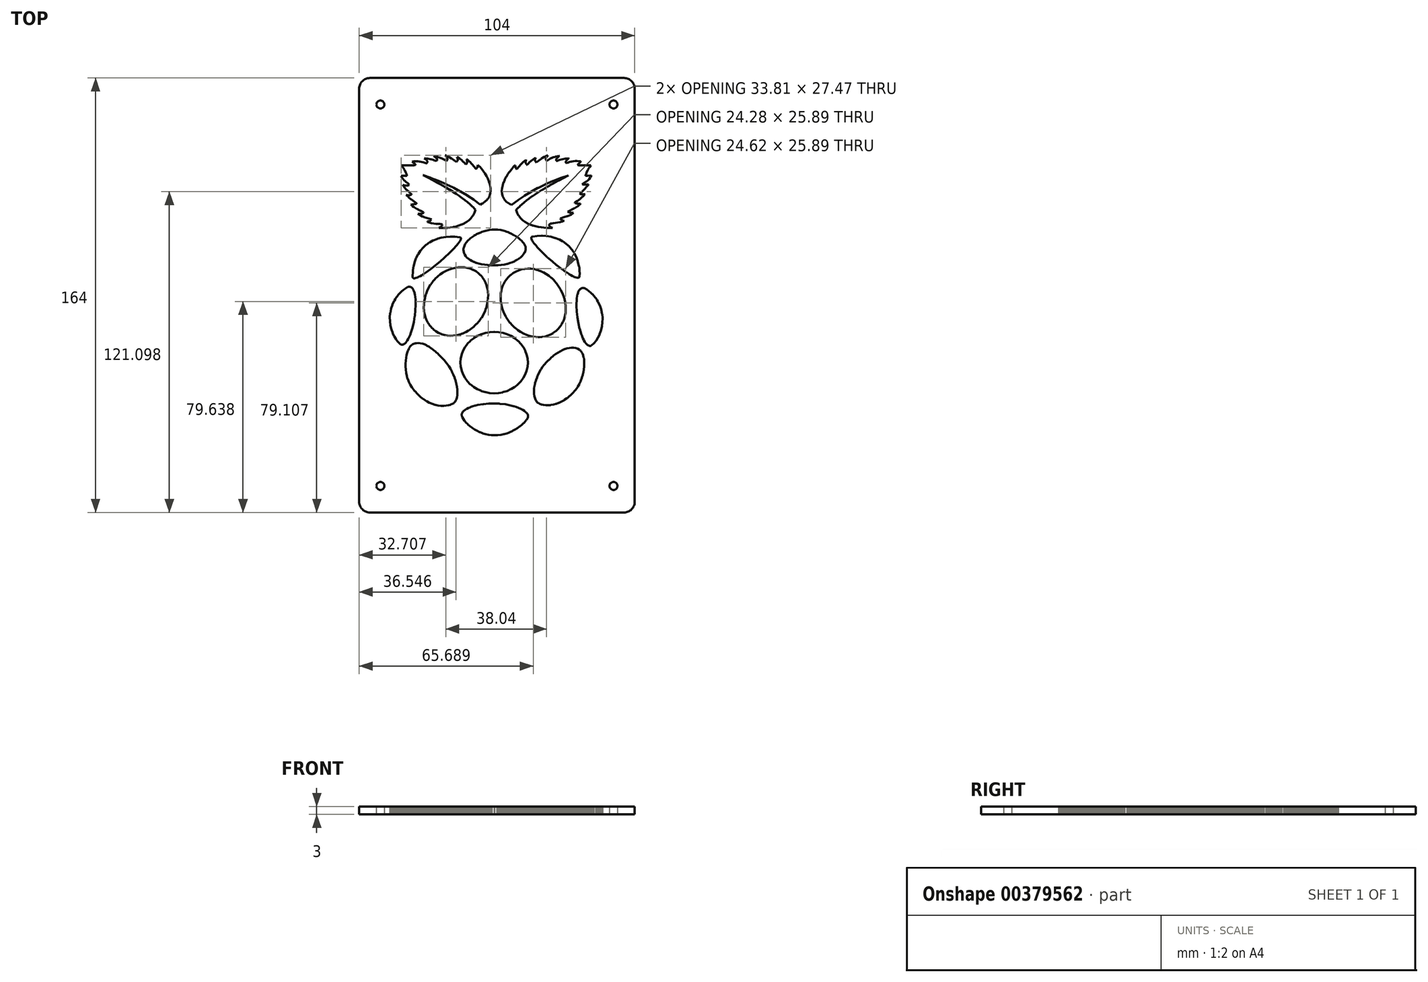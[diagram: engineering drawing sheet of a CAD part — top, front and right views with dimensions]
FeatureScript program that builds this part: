
annotation { "Feature Type Name" : "Feature", "Feature Type Description" : "" }
export const myFeature = defineFeature(function(context is Context, id is Id, definition is map)
    precondition{}
    {
        {
            var Q0;
            Q0=qCreatedBy(makeId("Top.planeOp"),FACE);
            var sketch = newSketch(context, id + "F0", { "sketchPlane" : qUnion([Q0])});
            skLineSegment(sketch, "E0.bottom", {"start": v(48, -82) * mm, "end": v(-48, -82) * mm});
            skLineSegment(sketch, "E0.top", {"start": v(48, 82) * mm, "end": v(-48, 82) * mm});
            skLineSegment(sketch, "E0.left", {"start": v(52, -78) * mm, "end": v(52, 78) * mm});
            skLineSegment(sketch, "E0.right", {"start": v(-52, -78) * mm, "end": v(-52, 78) * mm});
            skLineSegment(sketch, "E1", {"start": v(0, 97.18) * mm, "end": v(0, -103.74) * mm, "construction": true});
            skPoint(sketch, "E1.endSnap0", {"position": v(0, -82) * mm});
            skLineSegment(sketch, "E2", {"start": v(-56.62, 0) * mm, "end": v(57, 0) * mm, "construction": true});
            skPoint(sketch, "E3.visualSharp", {"position": v(-52, 82) * mm});
            skArc(sketch, "E3.filletArc", {"start": v(-48, 82) * mm, "mid": v(-50.83, 80.83) * mm, "end": v(-52, 78) * mm});
            skPoint(sketch, "E4.visualSharp", {"position": v(52, 82) * mm});
            skArc(sketch, "E4.filletArc", {"start": v(52, 78) * mm, "mid": v(50.83, 80.83) * mm, "end": v(48, 82) * mm});
            skPoint(sketch, "E5.visualSharp", {"position": v(52, -82) * mm});
            skArc(sketch, "E5.filletArc", {"start": v(48, -82) * mm, "mid": v(50.83, -80.83) * mm, "end": v(52, -78) * mm});
            skPoint(sketch, "E6.visualSharp", {"position": v(-52, -82) * mm});
            skArc(sketch, "E6.filletArc", {"start": v(-52, -78) * mm, "mid": v(-50.83, -80.83) * mm, "end": v(-48, -82) * mm});
            skLineSegment(sketch, "E7", {"start": v(-44, 86.75) * mm, "end": v(-44, -88.25) * mm, "construction": true});
            skLineSegment(sketch, "E8.MirrorCS", {"start": v(44, 86.75) * mm, "end": v(44, -88.25) * mm, "construction": true});
            skLineSegment(sketch, "E9", {"start": v(-54.83, 72) * mm, "end": v(56.5, 72) * mm, "construction": true});
            skLineSegment(sketch, "E10.MirrorCS", {"start": v(-54.83, -72) * mm, "end": v(56.5, -72) * mm, "construction": true});
            skCircle(sketch, "E11", {"center": v(-44, 72) * mm, "radius": 1.5 * mm});
            skCircle(sketch, "E12.MirrorC", {"center": v(44, 72) * mm, "radius": 1.5 * mm});
            skCircle(sketch, "E13.MirrorC", {"center": v(-44, -72) * mm, "radius": 1.5 * mm});
            skCircle(sketch, "E14.MirrorC", {"center": v(44, -72) * mm, "radius": 1.5 * mm});
            skLineSegment(sketch, "E15", {"start": v(7.16, 48.01) * mm, "end": v(7.15, 48.03) * mm});
            skLineSegment(sketch, "E16", {"start": v(7.15, 48.03) * mm, "end": v(7, 48.43) * mm});
            skLineSegment(sketch, "E17", {"start": v(7, 48.43) * mm, "end": v(6.99, 48.45) * mm});
            skLineSegment(sketch, "E18", {"start": v(6.99, 48.45) * mm, "end": v(6.83, 48.98) * mm});
            skLineSegment(sketch, "E19", {"start": v(6.83, 48.98) * mm, "end": v(6.83, 49) * mm});
            skLineSegment(sketch, "E20", {"start": v(6.83, 49) * mm, "end": v(6.18, 48.33) * mm});
            skLineSegment(sketch, "E21", {"start": v(6.18, 48.33) * mm, "end": v(6.15, 48.3) * mm});
            skLineSegment(sketch, "E22", {"start": v(6.15, 48.3) * mm, "end": v(5.5, 47.55) * mm});
            skLineSegment(sketch, "E23", {"start": v(5.5, 47.55) * mm, "end": v(5.45, 47.49) * mm});
            skLineSegment(sketch, "E24", {"start": v(5.45, 47.49) * mm, "end": v(4.8, 46.66) * mm});
            skLineSegment(sketch, "E25", {"start": v(4.8, 46.66) * mm, "end": v(4.76, 46.59) * mm});
            skLineSegment(sketch, "E26", {"start": v(4.76, 46.59) * mm, "end": v(4.14, 45.7) * mm});
            skLineSegment(sketch, "E27", {"start": v(4.14, 45.7) * mm, "end": v(3.56, 44.75) * mm});
            skLineSegment(sketch, "E28", {"start": v(3.56, 44.75) * mm, "end": v(3.52, 44.67) * mm});
            skLineSegment(sketch, "E29", {"start": v(3.52, 44.67) * mm, "end": v(3, 43.68) * mm});
            skLineSegment(sketch, "E30", {"start": v(3, 43.68) * mm, "end": v(2.96, 43.6) * mm});
            skLineSegment(sketch, "E31", {"start": v(2.96, 43.6) * mm, "end": v(2.53, 42.6) * mm});
            skLineSegment(sketch, "E32", {"start": v(2.53, 42.6) * mm, "end": v(2.5, 42.5) * mm});
            skLineSegment(sketch, "E33", {"start": v(2.5, 42.5) * mm, "end": v(2.16, 41.49) * mm});
            skLineSegment(sketch, "E34", {"start": v(2.16, 41.49) * mm, "end": v(2.15, 41.4) * mm});
            skLineSegment(sketch, "E35", {"start": v(2.15, 41.4) * mm, "end": v(1.93, 40.38) * mm});
            skLineSegment(sketch, "E36", {"start": v(1.93, 40.38) * mm, "end": v(1.92, 40.34) * mm});
            skLineSegment(sketch, "E37", {"start": v(1.92, 40.34) * mm, "end": v(1.84, 39.34) * mm});
            skLineSegment(sketch, "E38", {"start": v(1.84, 39.34) * mm, "end": v(1.84, 39.3) * mm});
            skLineSegment(sketch, "E39", {"start": v(1.84, 39.3) * mm, "end": v(1.92, 38.32) * mm});
            skLineSegment(sketch, "E40", {"start": v(1.92, 38.32) * mm, "end": v(1.92, 38.28) * mm});
            skLineSegment(sketch, "E41", {"start": v(1.92, 38.28) * mm, "end": v(2.03, 37.8) * mm});
            skLineSegment(sketch, "E42", {"start": v(2.03, 37.8) * mm, "end": v(2.04, 37.77) * mm});
            skLineSegment(sketch, "E43", {"start": v(2.04, 37.77) * mm, "end": v(2.18, 37.3) * mm});
            skLineSegment(sketch, "E44", {"start": v(2.18, 37.3) * mm, "end": v(2.2, 37.27) * mm});
            skLineSegment(sketch, "E45", {"start": v(2.2, 37.27) * mm, "end": v(2.4, 36.83) * mm});
            skLineSegment(sketch, "E46", {"start": v(2.4, 36.83) * mm, "end": v(2.65, 36.4) * mm});
            skLineSegment(sketch, "E47", {"start": v(2.65, 36.4) * mm, "end": v(2.67, 36.36) * mm});
            skLineSegment(sketch, "E48", {"start": v(2.67, 36.36) * mm, "end": v(2.97, 35.95) * mm});
            skLineSegment(sketch, "E49", {"start": v(2.97, 35.95) * mm, "end": v(3, 35.91) * mm});
            skLineSegment(sketch, "E50", {"start": v(3, 35.91) * mm, "end": v(3.35, 35.52) * mm});
            skLineSegment(sketch, "E51", {"start": v(3.35, 35.52) * mm, "end": v(3.4, 35.49) * mm});
            skLineSegment(sketch, "E52", {"start": v(3.4, 35.49) * mm, "end": v(3.8, 35.12) * mm});
            skLineSegment(sketch, "E53", {"start": v(3.8, 35.12) * mm, "end": v(4.28, 34.77) * mm});
            skLineSegment(sketch, "E54", {"start": v(4.28, 34.77) * mm, "end": v(4.32, 34.74) * mm});
            skLineSegment(sketch, "E55", {"start": v(4.32, 34.74) * mm, "end": v(4.86, 34.42) * mm});
            skLineSegment(sketch, "E56", {"start": v(4.86, 34.42) * mm, "end": v(5.46, 34.12) * mm});
            skLineSegment(sketch, "E57", {"start": v(5.46, 34.12) * mm, "end": v(5.5, 34.1) * mm});
            skLineSegment(sketch, "E58", {"start": v(5.5, 34.1) * mm, "end": v(5.52, 34.1) * mm});
            skLineSegment(sketch, "E59", {"start": v(5.52, 34.1) * mm, "end": v(5.64, 34.2) * mm});
            skLineSegment(sketch, "E60", {"start": v(5.64, 34.2) * mm, "end": v(7.85, 35.87) * mm});
            skLineSegment(sketch, "E61", {"start": v(7.85, 35.87) * mm, "end": v(7.98, 35.96) * mm});
            skLineSegment(sketch, "E62", {"start": v(7.98, 35.96) * mm, "end": v(10.28, 37.52) * mm});
            skLineSegment(sketch, "E63", {"start": v(10.28, 37.52) * mm, "end": v(10.41, 37.6) * mm});
            skLineSegment(sketch, "E64", {"start": v(10.41, 37.6) * mm, "end": v(12.8, 39.06) * mm});
            skLineSegment(sketch, "E65", {"start": v(12.8, 39.06) * mm, "end": v(12.94, 39.13) * mm});
            skLineSegment(sketch, "E66", {"start": v(12.94, 39.13) * mm, "end": v(15.42, 40.48) * mm});
            skLineSegment(sketch, "E67", {"start": v(15.42, 40.48) * mm, "end": v(15.6, 40.57) * mm});
            skLineSegment(sketch, "E68", {"start": v(15.6, 40.57) * mm, "end": v(18.16, 41.82) * mm});
            skLineSegment(sketch, "E69", {"start": v(18.16, 41.82) * mm, "end": v(18.34, 41.9) * mm});
            skLineSegment(sketch, "E70", {"start": v(18.34, 41.9) * mm, "end": v(21, 43.04) * mm});
            skLineSegment(sketch, "E71", {"start": v(21, 43.04) * mm, "end": v(21.18, 43.11) * mm});
            skLineSegment(sketch, "E72", {"start": v(21.18, 43.11) * mm, "end": v(23.91, 44.16) * mm});
            skLineSegment(sketch, "E73", {"start": v(23.91, 44.16) * mm, "end": v(26.73, 45.1) * mm});
            skLineSegment(sketch, "E74", {"start": v(26.73, 45.1) * mm, "end": v(26.83, 45.14) * mm});
            skLineSegment(sketch, "E75", {"start": v(26.83, 45.14) * mm, "end": v(26.92, 45.17) * mm});
            skLineSegment(sketch, "E76", {"start": v(26.92, 45.17) * mm, "end": v(25.1, 44.25) * mm});
            skLineSegment(sketch, "E77", {"start": v(25.1, 44.25) * mm, "end": v(25.02, 44.22) * mm});
            skLineSegment(sketch, "E78", {"start": v(25.02, 44.22) * mm, "end": v(23.35, 43.34) * mm});
            skLineSegment(sketch, "E79", {"start": v(23.35, 43.34) * mm, "end": v(23.23, 43.28) * mm});
            skLineSegment(sketch, "E80", {"start": v(23.23, 43.28) * mm, "end": v(21.64, 42.42) * mm});
            skLineSegment(sketch, "E81", {"start": v(21.64, 42.42) * mm, "end": v(21.53, 42.36) * mm});
            skLineSegment(sketch, "E82", {"start": v(21.53, 42.36) * mm, "end": v(20.02, 41.52) * mm});
            skLineSegment(sketch, "E83", {"start": v(20.02, 41.52) * mm, "end": v(19.92, 41.46) * mm});
            skLineSegment(sketch, "E84", {"start": v(19.92, 41.46) * mm, "end": v(18.5, 40.64) * mm});
            skLineSegment(sketch, "E85", {"start": v(18.5, 40.64) * mm, "end": v(18.4, 40.58) * mm});
            skLineSegment(sketch, "E86", {"start": v(18.4, 40.58) * mm, "end": v(17.07, 39.78) * mm});
            skLineSegment(sketch, "E87", {"start": v(17.07, 39.78) * mm, "end": v(16.98, 39.72) * mm});
            skLineSegment(sketch, "E88", {"start": v(16.98, 39.72) * mm, "end": v(15.72, 38.94) * mm});
            skLineSegment(sketch, "E89", {"start": v(15.72, 38.94) * mm, "end": v(14.54, 38.17) * mm});
            skLineSegment(sketch, "E90", {"start": v(14.54, 38.17) * mm, "end": v(14.46, 38.11) * mm});
            skLineSegment(sketch, "E91", {"start": v(14.46, 38.11) * mm, "end": v(13.36, 37.36) * mm});
            skLineSegment(sketch, "E92", {"start": v(13.36, 37.36) * mm, "end": v(13.28, 37.3) * mm});
            skLineSegment(sketch, "E93", {"start": v(13.28, 37.3) * mm, "end": v(12.26, 36.57) * mm});
            skLineSegment(sketch, "E94", {"start": v(12.26, 36.57) * mm, "end": v(12.16, 36.5) * mm});
            skLineSegment(sketch, "E95", {"start": v(12.16, 36.5) * mm, "end": v(11.2, 35.77) * mm});
            skLineSegment(sketch, "E96", {"start": v(11.2, 35.77) * mm, "end": v(10.33, 35.06) * mm});
            skLineSegment(sketch, "E97", {"start": v(10.33, 35.06) * mm, "end": v(10.24, 35) * mm});
            skLineSegment(sketch, "E98", {"start": v(10.24, 35) * mm, "end": v(9.43, 34.3) * mm});
            skLineSegment(sketch, "E99", {"start": v(9.43, 34.3) * mm, "end": v(8.69, 33.63) * mm});
            skLineSegment(sketch, "E100", {"start": v(8.69, 33.63) * mm, "end": v(8.61, 33.56) * mm});
            skLineSegment(sketch, "E101", {"start": v(8.61, 33.56) * mm, "end": v(7.94, 32.9) * mm});
            skLineSegment(sketch, "E102", {"start": v(7.94, 32.9) * mm, "end": v(7.33, 32.25) * mm});
            skLineSegment(sketch, "E103", {"start": v(7.33, 32.25) * mm, "end": v(7.28, 32.2) * mm});
            skLineSegment(sketch, "E104", {"start": v(7.28, 32.2) * mm, "end": v(7.26, 32.18) * mm});
            skLineSegment(sketch, "E105", {"start": v(7.26, 32.18) * mm, "end": v(7.28, 32.13) * mm});
            skLineSegment(sketch, "E106", {"start": v(7.28, 32.13) * mm, "end": v(7.66, 31.04) * mm});
            skLineSegment(sketch, "E107", {"start": v(7.66, 31.04) * mm, "end": v(7.68, 31) * mm});
            skLineSegment(sketch, "E108", {"start": v(7.68, 31) * mm, "end": v(8.2, 30.02) * mm});
            skLineSegment(sketch, "E109", {"start": v(8.2, 30.02) * mm, "end": v(8.23, 29.98) * mm});
            skLineSegment(sketch, "E110", {"start": v(8.23, 29.98) * mm, "end": v(8.87, 29.14) * mm});
            skLineSegment(sketch, "E111", {"start": v(8.87, 29.14) * mm, "end": v(8.9, 29.1) * mm});
            skLineSegment(sketch, "E112", {"start": v(8.9, 29.1) * mm, "end": v(8.94, 29.06) * mm});
            skLineSegment(sketch, "E113", {"start": v(8.94, 29.06) * mm, "end": v(9.68, 28.34) * mm});
            skLineSegment(sketch, "E114", {"start": v(9.68, 28.34) * mm, "end": v(9.73, 28.3) * mm});
            skLineSegment(sketch, "E115", {"start": v(9.73, 28.3) * mm, "end": v(10.56, 27.68) * mm});
            skLineSegment(sketch, "E116", {"start": v(10.56, 27.68) * mm, "end": v(10.61, 27.65) * mm});
            skLineSegment(sketch, "E117", {"start": v(10.61, 27.65) * mm, "end": v(11.5, 27.13) * mm});
            skLineSegment(sketch, "E118", {"start": v(11.5, 27.13) * mm, "end": v(11.56, 27.1) * mm});
            skLineSegment(sketch, "E119", {"start": v(11.56, 27.1) * mm, "end": v(12.51, 26.67) * mm});
            skLineSegment(sketch, "E120", {"start": v(12.51, 26.67) * mm, "end": v(12.57, 26.65) * mm});
            skLineSegment(sketch, "E121", {"start": v(12.57, 26.65) * mm, "end": v(13.55, 26.3) * mm});
            skLineSegment(sketch, "E122", {"start": v(13.55, 26.3) * mm, "end": v(13.61, 26.28) * mm});
            skLineSegment(sketch, "E123", {"start": v(13.61, 26.28) * mm, "end": v(14.6, 26) * mm});
            skLineSegment(sketch, "E124", {"start": v(14.6, 26) * mm, "end": v(14.67, 26) * mm});
            skLineSegment(sketch, "E125", {"start": v(14.67, 26) * mm, "end": v(15.67, 25.78) * mm});
            skLineSegment(sketch, "E126", {"start": v(15.67, 25.78) * mm, "end": v(15.73, 25.77) * mm});
            skLineSegment(sketch, "E127", {"start": v(15.73, 25.77) * mm, "end": v(16.7, 25.62) * mm});
            skLineSegment(sketch, "E128", {"start": v(16.7, 25.62) * mm, "end": v(16.8, 25.6) * mm});
            skLineSegment(sketch, "E129", {"start": v(16.8, 25.6) * mm, "end": v(17.74, 25.5) * mm});
            skLineSegment(sketch, "E130", {"start": v(17.74, 25.5) * mm, "end": v(18.63, 25.43) * mm});
            skLineSegment(sketch, "E131", {"start": v(18.63, 25.43) * mm, "end": v(18.69, 25.43) * mm});
            skLineSegment(sketch, "E132", {"start": v(18.69, 25.43) * mm, "end": v(19.5, 25.39) * mm});
            skLineSegment(sketch, "E133", {"start": v(19.5, 25.39) * mm, "end": v(19.56, 25.38) * mm});
            skLineSegment(sketch, "E134", {"start": v(19.56, 25.38) * mm, "end": v(20.3, 25.37) * mm});
            skLineSegment(sketch, "E135", {"start": v(20.3, 25.37) * mm, "end": v(20.34, 25.37) * mm});
            skLineSegment(sketch, "E136", {"start": v(20.34, 25.37) * mm, "end": v(20.98, 25.36) * mm});
            skLineSegment(sketch, "E137", {"start": v(20.98, 25.36) * mm, "end": v(21.02, 25.36) * mm});
            skLineSegment(sketch, "E138", {"start": v(21.02, 25.36) * mm, "end": v(21, 25.37) * mm});
            skLineSegment(sketch, "E139", {"start": v(21, 25.37) * mm, "end": v(20.55, 25.56) * mm});
            skLineSegment(sketch, "E140", {"start": v(20.55, 25.56) * mm, "end": v(20.53, 25.57) * mm});
            skLineSegment(sketch, "E141", {"start": v(20.53, 25.57) * mm, "end": v(20.32, 25.69) * mm});
            skLineSegment(sketch, "E142", {"start": v(20.32, 25.69) * mm, "end": v(20.3, 25.7) * mm});
            skLineSegment(sketch, "E143", {"start": v(20.3, 25.7) * mm, "end": v(20.12, 25.84) * mm});
            skLineSegment(sketch, "E144", {"start": v(20.12, 25.84) * mm, "end": v(20.11, 25.85) * mm});
            skLineSegment(sketch, "E145", {"start": v(20.11, 25.85) * mm, "end": v(19.96, 26) * mm});
            skLineSegment(sketch, "E146", {"start": v(19.96, 26) * mm, "end": v(19.95, 26.01) * mm});
            skLineSegment(sketch, "E147", {"start": v(19.95, 26.01) * mm, "end": v(19.88, 26.1) * mm});
            skLineSegment(sketch, "E148", {"start": v(19.88, 26.1) * mm, "end": v(19.88, 26.1) * mm});
            skLineSegment(sketch, "E149", {"start": v(19.88, 26.1) * mm, "end": v(19.82, 26.2) * mm});
            skLineSegment(sketch, "E150", {"start": v(19.82, 26.2) * mm, "end": v(19.82, 26.2) * mm});
            skLineSegment(sketch, "E151", {"start": v(19.82, 26.2) * mm, "end": v(19.77, 26.3) * mm});
            skLineSegment(sketch, "E152", {"start": v(19.77, 26.3) * mm, "end": v(19.77, 26.3) * mm});
            skLineSegment(sketch, "E153", {"start": v(19.77, 26.3) * mm, "end": v(19.74, 26.4) * mm});
            skLineSegment(sketch, "E154", {"start": v(19.74, 26.4) * mm, "end": v(19.74, 26.41) * mm});
            skLineSegment(sketch, "E155", {"start": v(19.74, 26.41) * mm, "end": v(19.72, 26.52) * mm});
            skLineSegment(sketch, "E156", {"start": v(19.72, 26.52) * mm, "end": v(19.72, 26.52) * mm});
            skLineSegment(sketch, "E157", {"start": v(19.72, 26.52) * mm, "end": v(19.7, 26.63) * mm});
            skLineSegment(sketch, "E158", {"start": v(19.7, 26.63) * mm, "end": v(19.7, 26.64) * mm});
            skLineSegment(sketch, "E159", {"start": v(19.7, 26.64) * mm, "end": v(19.71, 26.64) * mm});
            skLineSegment(sketch, "E160", {"start": v(19.71, 26.64) * mm, "end": v(19.78, 26.71) * mm});
            skLineSegment(sketch, "E161", {"start": v(19.78, 26.71) * mm, "end": v(19.78, 26.72) * mm});
            skLineSegment(sketch, "E162", {"start": v(19.78, 26.72) * mm, "end": v(19.86, 26.78) * mm});
            skLineSegment(sketch, "E163", {"start": v(19.86, 26.78) * mm, "end": v(19.86, 26.79) * mm});
            skLineSegment(sketch, "E164", {"start": v(19.86, 26.79) * mm, "end": v(19.95, 26.85) * mm});
            skLineSegment(sketch, "E165", {"start": v(19.95, 26.85) * mm, "end": v(19.95, 26.85) * mm});
            skLineSegment(sketch, "E166", {"start": v(19.95, 26.85) * mm, "end": v(20.06, 26.9) * mm});
            skLineSegment(sketch, "E167", {"start": v(20.06, 26.9) * mm, "end": v(20.07, 26.9) * mm});
            skLineSegment(sketch, "E168", {"start": v(20.07, 26.9) * mm, "end": v(20.3, 27) * mm});
            skLineSegment(sketch, "E169", {"start": v(20.3, 27) * mm, "end": v(20.31, 27) * mm});
            skLineSegment(sketch, "E170", {"start": v(20.31, 27) * mm, "end": v(20.58, 27.08) * mm});
            skLineSegment(sketch, "E171", {"start": v(20.58, 27.08) * mm, "end": v(20.62, 27.09) * mm});
            skLineSegment(sketch, "E172", {"start": v(20.62, 27.09) * mm, "end": v(21.26, 27.2) * mm});
            skLineSegment(sketch, "E173", {"start": v(21.26, 27.2) * mm, "end": v(21.34, 27.21) * mm});
            skLineSegment(sketch, "E174", {"start": v(21.34, 27.21) * mm, "end": v(22.07, 27.3) * mm});
            skLineSegment(sketch, "E175", {"start": v(22.07, 27.3) * mm, "end": v(23.68, 27.56) * mm});
            skLineSegment(sketch, "E176", {"start": v(23.68, 27.56) * mm, "end": v(23.76, 27.57) * mm});
            skLineSegment(sketch, "E177", {"start": v(23.76, 27.57) * mm, "end": v(23.81, 27.58) * mm});
            skLineSegment(sketch, "E178", {"start": v(23.81, 27.58) * mm, "end": v(24.6, 27.8) * mm});
            skLineSegment(sketch, "E179", {"start": v(24.6, 27.8) * mm, "end": v(24.63, 27.8) * mm});
            skLineSegment(sketch, "E180", {"start": v(24.63, 27.8) * mm, "end": v(25.36, 28.12) * mm});
            skLineSegment(sketch, "E181", {"start": v(25.36, 28.12) * mm, "end": v(25.39, 28.13) * mm});
            skLineSegment(sketch, "E182", {"start": v(25.39, 28.13) * mm, "end": v(25.38, 28.13) * mm});
            skLineSegment(sketch, "E183", {"start": v(25.38, 28.13) * mm, "end": v(25.36, 28.14) * mm});
            skLineSegment(sketch, "E184", {"start": v(25.36, 28.14) * mm, "end": v(24.85, 28.26) * mm});
            skLineSegment(sketch, "E185", {"start": v(24.85, 28.26) * mm, "end": v(24.83, 28.27) * mm});
            skLineSegment(sketch, "E186", {"start": v(24.83, 28.27) * mm, "end": v(24.64, 28.32) * mm});
            skLineSegment(sketch, "E187", {"start": v(24.64, 28.32) * mm, "end": v(24.63, 28.33) * mm});
            skLineSegment(sketch, "E188", {"start": v(24.63, 28.33) * mm, "end": v(24.47, 28.4) * mm});
            skLineSegment(sketch, "E189", {"start": v(24.47, 28.4) * mm, "end": v(24.45, 28.4) * mm});
            skLineSegment(sketch, "E190", {"start": v(24.45, 28.4) * mm, "end": v(24.3, 28.49) * mm});
            skLineSegment(sketch, "E191", {"start": v(24.3, 28.49) * mm, "end": v(24.3, 28.5) * mm});
            skLineSegment(sketch, "E192", {"start": v(24.3, 28.5) * mm, "end": v(24.16, 28.6) * mm});
            skLineSegment(sketch, "E193", {"start": v(24.16, 28.6) * mm, "end": v(24.15, 28.62) * mm});
            skLineSegment(sketch, "E194", {"start": v(24.15, 28.62) * mm, "end": v(24.01, 28.77) * mm});
            skLineSegment(sketch, "E195", {"start": v(24.01, 28.77) * mm, "end": v(23.87, 28.97) * mm});
            skLineSegment(sketch, "E196", {"start": v(23.87, 28.97) * mm, "end": v(23.86, 28.98) * mm});
            skLineSegment(sketch, "E197", {"start": v(23.86, 28.98) * mm, "end": v(23.86, 28.98) * mm});
            skLineSegment(sketch, "E198", {"start": v(23.86, 28.98) * mm, "end": v(23.93, 29) * mm});
            skLineSegment(sketch, "E199", {"start": v(23.93, 29) * mm, "end": v(25.3, 29.43) * mm});
            skLineSegment(sketch, "E200", {"start": v(25.3, 29.43) * mm, "end": v(25.35, 29.44) * mm});
            skLineSegment(sketch, "E201", {"start": v(25.35, 29.44) * mm, "end": v(26.65, 29.87) * mm});
            skLineSegment(sketch, "E202", {"start": v(26.65, 29.87) * mm, "end": v(26.71, 29.9) * mm});
            skLineSegment(sketch, "E203", {"start": v(26.71, 29.9) * mm, "end": v(27.3, 30.13) * mm});
            skLineSegment(sketch, "E204", {"start": v(27.3, 30.13) * mm, "end": v(27.37, 30.16) * mm});
            skLineSegment(sketch, "E205", {"start": v(27.37, 30.16) * mm, "end": v(27.91, 30.42) * mm});
            skLineSegment(sketch, "E206", {"start": v(27.91, 30.42) * mm, "end": v(28.4, 30.72) * mm});
            skLineSegment(sketch, "E207", {"start": v(28.4, 30.72) * mm, "end": v(28.43, 30.74) * mm});
            skLineSegment(sketch, "E208", {"start": v(28.43, 30.74) * mm, "end": v(28.86, 31.1) * mm});
            skLineSegment(sketch, "E209", {"start": v(28.86, 31.1) * mm, "end": v(28.88, 31.11) * mm});
            skLineSegment(sketch, "E210", {"start": v(28.88, 31.11) * mm, "end": v(28.86, 31.11) * mm});
            skLineSegment(sketch, "E211", {"start": v(28.86, 31.11) * mm, "end": v(27.9, 31.09) * mm});
            skLineSegment(sketch, "E212", {"start": v(27.9, 31.09) * mm, "end": v(27.9, 31.08) * mm});
            skLineSegment(sketch, "E213", {"start": v(27.9, 31.08) * mm, "end": v(27.87, 31.09) * mm});
            skLineSegment(sketch, "E214", {"start": v(27.87, 31.09) * mm, "end": v(27.86, 31.09) * mm});
            skLineSegment(sketch, "E215", {"start": v(27.86, 31.09) * mm, "end": v(27.6, 31.12) * mm});
            skLineSegment(sketch, "E216", {"start": v(27.6, 31.12) * mm, "end": v(27.6, 31.12) * mm});
            skLineSegment(sketch, "E217", {"start": v(27.6, 31.12) * mm, "end": v(27.32, 31.2) * mm});
            skLineSegment(sketch, "E218", {"start": v(27.32, 31.2) * mm, "end": v(27.3, 31.2) * mm});
            skLineSegment(sketch, "E219", {"start": v(27.3, 31.2) * mm, "end": v(27.02, 31.33) * mm});
            skLineSegment(sketch, "E220", {"start": v(27.02, 31.33) * mm, "end": v(27, 31.34) * mm});
            skLineSegment(sketch, "E221", {"start": v(27, 31.34) * mm, "end": v(26.7, 31.53) * mm});
            skLineSegment(sketch, "E222", {"start": v(26.7, 31.53) * mm, "end": v(26.7, 31.53) * mm});
            skLineSegment(sketch, "E223", {"start": v(26.7, 31.53) * mm, "end": v(26.76, 31.57) * mm});
            skLineSegment(sketch, "E224", {"start": v(26.76, 31.57) * mm, "end": v(29.18, 32.74) * mm});
            skLineSegment(sketch, "E225", {"start": v(29.18, 32.74) * mm, "end": v(29.21, 32.76) * mm});
            skLineSegment(sketch, "E226", {"start": v(29.21, 32.76) * mm, "end": v(29.27, 32.8) * mm});
            skLineSegment(sketch, "E227", {"start": v(29.27, 32.8) * mm, "end": v(30.39, 33.5) * mm});
            skLineSegment(sketch, "E228", {"start": v(30.39, 33.5) * mm, "end": v(30.44, 33.54) * mm});
            skLineSegment(sketch, "E229", {"start": v(30.44, 33.54) * mm, "end": v(30.47, 33.57) * mm});
            skLineSegment(sketch, "E230", {"start": v(30.47, 33.57) * mm, "end": v(30.99, 34) * mm});
            skLineSegment(sketch, "E231", {"start": v(30.99, 34) * mm, "end": v(31.47, 34.49) * mm});
            skLineSegment(sketch, "E232", {"start": v(31.47, 34.49) * mm, "end": v(31.5, 34.52) * mm});
            skLineSegment(sketch, "E233", {"start": v(31.5, 34.52) * mm, "end": v(30.87, 34.53) * mm});
            skLineSegment(sketch, "E234", {"start": v(30.87, 34.53) * mm, "end": v(30.85, 34.53) * mm});
            skLineSegment(sketch, "E235", {"start": v(30.85, 34.53) * mm, "end": v(30.84, 34.53) * mm});
            skLineSegment(sketch, "E236", {"start": v(30.84, 34.53) * mm, "end": v(30.27, 34.57) * mm});
            skLineSegment(sketch, "E237", {"start": v(30.27, 34.57) * mm, "end": v(30.24, 34.57) * mm});
            skLineSegment(sketch, "E238", {"start": v(30.24, 34.57) * mm, "end": v(29.99, 34.62) * mm});
            skLineSegment(sketch, "E239", {"start": v(29.99, 34.62) * mm, "end": v(29.96, 34.62) * mm});
            skLineSegment(sketch, "E240", {"start": v(29.96, 34.62) * mm, "end": v(29.73, 34.7) * mm});
            skLineSegment(sketch, "E241", {"start": v(29.73, 34.7) * mm, "end": v(29.72, 34.7) * mm});
            skLineSegment(sketch, "E242", {"start": v(29.72, 34.7) * mm, "end": v(29.61, 34.74) * mm});
            skLineSegment(sketch, "E243", {"start": v(29.61, 34.74) * mm, "end": v(29.6, 34.75) * mm});
            skLineSegment(sketch, "E244", {"start": v(29.6, 34.75) * mm, "end": v(29.5, 34.8) * mm});
            skLineSegment(sketch, "E245", {"start": v(29.5, 34.8) * mm, "end": v(29.4, 34.87) * mm});
            skLineSegment(sketch, "E246", {"start": v(29.4, 34.87) * mm, "end": v(29.32, 34.94) * mm});
            skLineSegment(sketch, "E247", {"start": v(29.32, 34.94) * mm, "end": v(29.32, 34.94) * mm});
            skLineSegment(sketch, "E248", {"start": v(29.32, 34.94) * mm, "end": v(29.38, 34.98) * mm});
            skLineSegment(sketch, "E249", {"start": v(29.38, 34.98) * mm, "end": v(30.42, 35.62) * mm});
            skLineSegment(sketch, "E250", {"start": v(30.42, 35.62) * mm, "end": v(31.39, 36.34) * mm});
            skLineSegment(sketch, "E251", {"start": v(31.39, 36.34) * mm, "end": v(31.45, 36.38) * mm});
            skLineSegment(sketch, "E252", {"start": v(31.45, 36.38) * mm, "end": v(32.33, 37.17) * mm});
            skLineSegment(sketch, "E253", {"start": v(32.33, 37.17) * mm, "end": v(32.39, 37.22) * mm});
            skLineSegment(sketch, "E254", {"start": v(32.39, 37.22) * mm, "end": v(33.2, 38.08) * mm});
            skLineSegment(sketch, "E255", {"start": v(33.2, 38.08) * mm, "end": v(33.25, 38.14) * mm});
            skLineSegment(sketch, "E256", {"start": v(33.25, 38.14) * mm, "end": v(32.8, 38.08) * mm});
            skLineSegment(sketch, "E257", {"start": v(32.8, 38.08) * mm, "end": v(32.8, 38.08) * mm});
            skLineSegment(sketch, "E258", {"start": v(32.8, 38.08) * mm, "end": v(32.78, 38.08) * mm});
            skLineSegment(sketch, "E259", {"start": v(32.78, 38.08) * mm, "end": v(32.42, 38.05) * mm});
            skLineSegment(sketch, "E260", {"start": v(32.42, 38.05) * mm, "end": v(32.4, 38.05) * mm});
            skLineSegment(sketch, "E261", {"start": v(32.4, 38.05) * mm, "end": v(32.1, 38.06) * mm});
            skLineSegment(sketch, "E262", {"start": v(32.1, 38.06) * mm, "end": v(31.87, 38.08) * mm});
            skLineSegment(sketch, "E263", {"start": v(31.87, 38.08) * mm, "end": v(31.85, 38.09) * mm});
            skLineSegment(sketch, "E264", {"start": v(31.85, 38.09) * mm, "end": v(31.66, 38.13) * mm});
            skLineSegment(sketch, "E265", {"start": v(31.66, 38.13) * mm, "end": v(31.65, 38.13) * mm});
            skLineSegment(sketch, "E266", {"start": v(31.65, 38.13) * mm, "end": v(31.65, 38.14) * mm});
            skLineSegment(sketch, "E267", {"start": v(31.65, 38.14) * mm, "end": v(31.5, 38.2) * mm});
            skLineSegment(sketch, "E268", {"start": v(31.5, 38.2) * mm, "end": v(31.5, 38.2) * mm});
            skLineSegment(sketch, "E269", {"start": v(31.5, 38.2) * mm, "end": v(31.37, 38.27) * mm});
            skLineSegment(sketch, "E270", {"start": v(31.37, 38.27) * mm, "end": v(31.29, 38.35) * mm});
            skLineSegment(sketch, "E271", {"start": v(31.29, 38.35) * mm, "end": v(31.28, 38.35) * mm});
            skLineSegment(sketch, "E272", {"start": v(31.28, 38.35) * mm, "end": v(31.28, 38.35) * mm});
            skLineSegment(sketch, "E273", {"start": v(31.28, 38.35) * mm, "end": v(31.32, 38.4) * mm});
            skLineSegment(sketch, "E274", {"start": v(31.32, 38.4) * mm, "end": v(32.15, 39.15) * mm});
            skLineSegment(sketch, "E275", {"start": v(32.15, 39.15) * mm, "end": v(32.18, 39.17) * mm});
            skLineSegment(sketch, "E276", {"start": v(32.18, 39.17) * mm, "end": v(33.05, 39.97) * mm});
            skLineSegment(sketch, "E277", {"start": v(33.05, 39.97) * mm, "end": v(33.1, 40.01) * mm});
            skLineSegment(sketch, "E278", {"start": v(33.1, 40.01) * mm, "end": v(33.88, 40.88) * mm});
            skLineSegment(sketch, "E279", {"start": v(33.88, 40.88) * mm, "end": v(33.93, 40.93) * mm});
            skLineSegment(sketch, "E280", {"start": v(33.93, 40.93) * mm, "end": v(34.25, 41.4) * mm});
            skLineSegment(sketch, "E281", {"start": v(34.25, 41.4) * mm, "end": v(34.28, 41.43) * mm});
            skLineSegment(sketch, "E282", {"start": v(34.28, 41.43) * mm, "end": v(34.54, 41.94) * mm});
            skLineSegment(sketch, "E283", {"start": v(34.54, 41.94) * mm, "end": v(34.56, 41.97) * mm});
            skLineSegment(sketch, "E284", {"start": v(34.56, 41.97) * mm, "end": v(33.93, 41.83) * mm});
            skLineSegment(sketch, "E285", {"start": v(33.93, 41.83) * mm, "end": v(33.9, 41.82) * mm});
            skLineSegment(sketch, "E286", {"start": v(33.9, 41.82) * mm, "end": v(33.9, 41.82) * mm});
            skLineSegment(sketch, "E287", {"start": v(33.9, 41.82) * mm, "end": v(33.3, 41.74) * mm});
            skLineSegment(sketch, "E288", {"start": v(33.3, 41.74) * mm, "end": v(33.28, 41.73) * mm});
            skLineSegment(sketch, "E289", {"start": v(33.28, 41.73) * mm, "end": v(33, 41.73) * mm});
            skLineSegment(sketch, "E290", {"start": v(33, 41.73) * mm, "end": v(32.97, 41.73) * mm});
            skLineSegment(sketch, "E291", {"start": v(32.97, 41.73) * mm, "end": v(32.7, 41.76) * mm});
            skLineSegment(sketch, "E292", {"start": v(32.7, 41.76) * mm, "end": v(32.69, 41.76) * mm});
            skLineSegment(sketch, "E293", {"start": v(32.69, 41.76) * mm, "end": v(32.56, 41.8) * mm});
            skLineSegment(sketch, "E294", {"start": v(32.56, 41.8) * mm, "end": v(32.54, 41.8) * mm});
            skLineSegment(sketch, "E295", {"start": v(32.54, 41.8) * mm, "end": v(32.42, 41.84) * mm});
            skLineSegment(sketch, "E296", {"start": v(32.42, 41.84) * mm, "end": v(32.4, 41.84) * mm});
            skLineSegment(sketch, "E297", {"start": v(32.4, 41.84) * mm, "end": v(32.29, 41.9) * mm});
            skLineSegment(sketch, "E298", {"start": v(32.29, 41.9) * mm, "end": v(32.17, 41.97) * mm});
            skLineSegment(sketch, "E299", {"start": v(32.17, 41.97) * mm, "end": v(32.16, 41.97) * mm});
            skLineSegment(sketch, "E300", {"start": v(32.16, 41.97) * mm, "end": v(32.16, 41.97) * mm});
            skLineSegment(sketch, "E301", {"start": v(32.16, 41.97) * mm, "end": v(32.51, 42.2) * mm});
            skLineSegment(sketch, "E302", {"start": v(32.51, 42.2) * mm, "end": v(32.52, 42.2) * mm});
            skLineSegment(sketch, "E303", {"start": v(32.52, 42.2) * mm, "end": v(32.53, 42.21) * mm});
            skLineSegment(sketch, "E304", {"start": v(32.53, 42.21) * mm, "end": v(32.94, 42.44) * mm});
            skLineSegment(sketch, "E305", {"start": v(32.94, 42.44) * mm, "end": v(32.97, 42.45) * mm});
            skLineSegment(sketch, "E306", {"start": v(32.97, 42.45) * mm, "end": v(33.86, 42.99) * mm});
            skLineSegment(sketch, "E307", {"start": v(33.86, 42.99) * mm, "end": v(33.9, 43.02) * mm});
            skLineSegment(sketch, "E308", {"start": v(33.9, 43.02) * mm, "end": v(34.37, 43.37) * mm});
            skLineSegment(sketch, "E309", {"start": v(34.37, 43.37) * mm, "end": v(34.39, 43.4) * mm});
            skLineSegment(sketch, "E310", {"start": v(34.39, 43.4) * mm, "end": v(34.41, 43.41) * mm});
            skLineSegment(sketch, "E311", {"start": v(34.41, 43.41) * mm, "end": v(34.85, 43.85) * mm});
            skLineSegment(sketch, "E312", {"start": v(34.85, 43.85) * mm, "end": v(34.87, 43.87) * mm});
            skLineSegment(sketch, "E313", {"start": v(34.87, 43.87) * mm, "end": v(35.27, 44.42) * mm});
            skLineSegment(sketch, "E314", {"start": v(35.27, 44.42) * mm, "end": v(35.28, 44.44) * mm});
            skLineSegment(sketch, "E315", {"start": v(35.28, 44.44) * mm, "end": v(35.3, 44.46) * mm});
            skLineSegment(sketch, "E316", {"start": v(35.3, 44.46) * mm, "end": v(35.64, 45.14) * mm});
            skLineSegment(sketch, "E317", {"start": v(35.64, 45.14) * mm, "end": v(35.65, 45.17) * mm});
            skLineSegment(sketch, "E318", {"start": v(35.65, 45.17) * mm, "end": v(35.61, 45.17) * mm});
            skLineSegment(sketch, "E319", {"start": v(35.61, 45.17) * mm, "end": v(34.36, 45.1) * mm});
            skLineSegment(sketch, "E320", {"start": v(34.36, 45.1) * mm, "end": v(34.34, 45.1) * mm});
            skLineSegment(sketch, "E321", {"start": v(34.34, 45.1) * mm, "end": v(34.3, 45.09) * mm});
            skLineSegment(sketch, "E322", {"start": v(34.3, 45.09) * mm, "end": v(33.8, 45.08) * mm});
            skLineSegment(sketch, "E323", {"start": v(33.8, 45.08) * mm, "end": v(33.78, 45.08) * mm});
            skLineSegment(sketch, "E324", {"start": v(33.78, 45.08) * mm, "end": v(33.68, 45.09) * mm});
            skLineSegment(sketch, "E325", {"start": v(33.68, 45.09) * mm, "end": v(33.67, 45.1) * mm});
            skLineSegment(sketch, "E326", {"start": v(33.67, 45.1) * mm, "end": v(33.6, 45.1) * mm});
            skLineSegment(sketch, "E327", {"start": v(33.6, 45.1) * mm, "end": v(33.59, 45.1) * mm});
            skLineSegment(sketch, "E328", {"start": v(33.59, 45.1) * mm, "end": v(33.55, 45.12) * mm});
            skLineSegment(sketch, "E329", {"start": v(33.55, 45.12) * mm, "end": v(33.52, 45.13) * mm});
            skLineSegment(sketch, "E330", {"start": v(33.52, 45.13) * mm, "end": v(33.5, 45.15) * mm});
            skLineSegment(sketch, "E331", {"start": v(33.5, 45.15) * mm, "end": v(33.47, 45.17) * mm});
            skLineSegment(sketch, "E332", {"start": v(33.47, 45.17) * mm, "end": v(33.47, 45.17) * mm});
            skLineSegment(sketch, "E333", {"start": v(33.47, 45.17) * mm, "end": v(33.48, 45.2) * mm});
            skLineSegment(sketch, "E334", {"start": v(33.48, 45.2) * mm, "end": v(33.65, 45.77) * mm});
            skLineSegment(sketch, "E335", {"start": v(33.65, 45.77) * mm, "end": v(33.85, 46.3) * mm});
            skLineSegment(sketch, "E336", {"start": v(33.85, 46.3) * mm, "end": v(33.88, 46.36) * mm});
            skLineSegment(sketch, "E337", {"start": v(33.88, 46.36) * mm, "end": v(34.35, 47.29) * mm});
            skLineSegment(sketch, "E338", {"start": v(34.35, 47.29) * mm, "end": v(34.37, 47.34) * mm});
            skLineSegment(sketch, "E339", {"start": v(34.37, 47.34) * mm, "end": v(34.88, 48.15) * mm});
            skLineSegment(sketch, "E340", {"start": v(34.88, 48.15) * mm, "end": v(34.91, 48.2) * mm});
            skLineSegment(sketch, "E341", {"start": v(34.91, 48.2) * mm, "end": v(35.42, 48.98) * mm});
            skLineSegment(sketch, "E342", {"start": v(35.42, 48.98) * mm, "end": v(35.43, 49) * mm});
            skLineSegment(sketch, "E343", {"start": v(35.43, 49) * mm, "end": v(34.63, 49) * mm});
            skLineSegment(sketch, "E344", {"start": v(34.63, 49) * mm, "end": v(33.82, 49) * mm});
            skLineSegment(sketch, "E345", {"start": v(33.82, 49) * mm, "end": v(33.75, 49) * mm});
            skLineSegment(sketch, "E346", {"start": v(33.75, 49) * mm, "end": v(32.17, 49.03) * mm});
            skLineSegment(sketch, "E347", {"start": v(32.17, 49.03) * mm, "end": v(32.1, 49.03) * mm});
            skLineSegment(sketch, "E348", {"start": v(32.1, 49.03) * mm, "end": v(32.07, 49.03) * mm});
            skLineSegment(sketch, "E349", {"start": v(32.07, 49.03) * mm, "end": v(31.4, 49.05) * mm});
            skLineSegment(sketch, "E350", {"start": v(31.4, 49.05) * mm, "end": v(31.37, 49.05) * mm});
            skLineSegment(sketch, "E351", {"start": v(31.37, 49.05) * mm, "end": v(30.85, 49.09) * mm});
            skLineSegment(sketch, "E352", {"start": v(30.85, 49.09) * mm, "end": v(30.83, 49.1) * mm});
            skLineSegment(sketch, "E353", {"start": v(30.83, 49.1) * mm, "end": v(30.64, 49.11) * mm});
            skLineSegment(sketch, "E354", {"start": v(30.64, 49.11) * mm, "end": v(30.62, 49.12) * mm});
            skLineSegment(sketch, "E355", {"start": v(30.62, 49.12) * mm, "end": v(30.49, 49.14) * mm});
            skLineSegment(sketch, "E356", {"start": v(30.49, 49.14) * mm, "end": v(30.44, 49.16) * mm});
            skLineSegment(sketch, "E357", {"start": v(30.44, 49.16) * mm, "end": v(30.43, 49.17) * mm});
            skLineSegment(sketch, "E358", {"start": v(30.43, 49.17) * mm, "end": v(30.42, 49.17) * mm});
            skLineSegment(sketch, "E359", {"start": v(30.42, 49.17) * mm, "end": v(30.42, 49.17) * mm});
            skLineSegment(sketch, "E360", {"start": v(30.42, 49.17) * mm, "end": v(30.41, 49.18) * mm});
            skLineSegment(sketch, "E361", {"start": v(30.41, 49.18) * mm, "end": v(30.41, 49.18) * mm});
            skLineSegment(sketch, "E362", {"start": v(30.41, 49.18) * mm, "end": v(30.4, 49.18) * mm});
            skLineSegment(sketch, "E363", {"start": v(30.4, 49.18) * mm, "end": v(30.4, 49.19) * mm});
            skLineSegment(sketch, "E364", {"start": v(30.4, 49.19) * mm, "end": v(30.4, 49.19) * mm});
            skLineSegment(sketch, "E365", {"start": v(30.4, 49.19) * mm, "end": v(30.4, 49.2) * mm});
            skLineSegment(sketch, "E366", {"start": v(30.4, 49.2) * mm, "end": v(30.4, 49.2) * mm});
            skLineSegment(sketch, "E367", {"start": v(30.4, 49.2) * mm, "end": v(30.4, 49.21) * mm});
            skLineSegment(sketch, "E368", {"start": v(30.4, 49.21) * mm, "end": v(31.68, 50.46) * mm});
            skLineSegment(sketch, "E369", {"start": v(31.68, 50.46) * mm, "end": v(31.72, 50.5) * mm});
            skLineSegment(sketch, "E370", {"start": v(31.72, 50.5) * mm, "end": v(31, 50.6) * mm});
            skLineSegment(sketch, "E371", {"start": v(31, 50.6) * mm, "end": v(30.97, 50.61) * mm});
            skLineSegment(sketch, "E372", {"start": v(30.97, 50.61) * mm, "end": v(30.26, 50.66) * mm});
            skLineSegment(sketch, "E373", {"start": v(30.26, 50.66) * mm, "end": v(30.21, 50.66) * mm});
            skLineSegment(sketch, "E374", {"start": v(30.21, 50.66) * mm, "end": v(29.5, 50.65) * mm});
            skLineSegment(sketch, "E375", {"start": v(29.5, 50.65) * mm, "end": v(29.46, 50.64) * mm});
            skLineSegment(sketch, "E376", {"start": v(29.46, 50.64) * mm, "end": v(28.77, 50.58) * mm});
            skLineSegment(sketch, "E377", {"start": v(28.77, 50.58) * mm, "end": v(28.73, 50.57) * mm});
            skLineSegment(sketch, "E378", {"start": v(28.73, 50.57) * mm, "end": v(28.07, 50.45) * mm});
            skLineSegment(sketch, "E379", {"start": v(28.07, 50.45) * mm, "end": v(28, 50.44) * mm});
            skLineSegment(sketch, "E380", {"start": v(28, 50.44) * mm, "end": v(27.38, 50.28) * mm});
            skLineSegment(sketch, "E381", {"start": v(27.38, 50.28) * mm, "end": v(26.82, 50.1) * mm});
            skLineSegment(sketch, "E382", {"start": v(26.82, 50.1) * mm, "end": v(26.79, 50.08) * mm});
            skLineSegment(sketch, "E383", {"start": v(26.79, 50.08) * mm, "end": v(26.29, 49.87) * mm});
            skLineSegment(sketch, "E384", {"start": v(26.29, 49.87) * mm, "end": v(26.26, 49.85) * mm});
            skLineSegment(sketch, "E385", {"start": v(26.26, 49.85) * mm, "end": v(26.26, 49.86) * mm});
            skLineSegment(sketch, "E386", {"start": v(26.26, 49.86) * mm, "end": v(26.16, 49.93) * mm});
            skLineSegment(sketch, "E387", {"start": v(26.16, 49.93) * mm, "end": v(26.11, 49.98) * mm});
            skLineSegment(sketch, "E388", {"start": v(26.11, 49.98) * mm, "end": v(26.1, 49.98) * mm});
            skLineSegment(sketch, "E389", {"start": v(26.1, 49.98) * mm, "end": v(26.07, 50.02) * mm});
            skLineSegment(sketch, "E390", {"start": v(26.07, 50.02) * mm, "end": v(26.05, 50.07) * mm});
            skLineSegment(sketch, "E391", {"start": v(26.05, 50.07) * mm, "end": v(26.05, 50.07) * mm});
            skLineSegment(sketch, "E392", {"start": v(26.05, 50.07) * mm, "end": v(26.03, 50.12) * mm});
            skLineSegment(sketch, "E393", {"start": v(26.03, 50.12) * mm, "end": v(26.02, 50.12) * mm});
            skLineSegment(sketch, "E394", {"start": v(26.02, 50.12) * mm, "end": v(26, 50.16) * mm});
            skLineSegment(sketch, "E395", {"start": v(26, 50.16) * mm, "end": v(26, 50.17) * mm});
            skLineSegment(sketch, "E396", {"start": v(26, 50.17) * mm, "end": v(26, 50.21) * mm});
            skLineSegment(sketch, "E397", {"start": v(26, 50.21) * mm, "end": v(26, 50.26) * mm});
            skLineSegment(sketch, "E398", {"start": v(26, 50.26) * mm, "end": v(26, 50.27) * mm});
            skLineSegment(sketch, "E399", {"start": v(26, 50.27) * mm, "end": v(26, 50.31) * mm});
            skLineSegment(sketch, "E400", {"start": v(26, 50.31) * mm, "end": v(26, 50.32) * mm});
            skLineSegment(sketch, "E401", {"start": v(26, 50.32) * mm, "end": v(26, 50.37) * mm});
            skLineSegment(sketch, "E402", {"start": v(26, 50.37) * mm, "end": v(26, 50.37) * mm});
            skLineSegment(sketch, "E403", {"start": v(26, 50.37) * mm, "end": v(26.02, 50.42) * mm});
            skLineSegment(sketch, "E404", {"start": v(26.02, 50.42) * mm, "end": v(26.02, 50.43) * mm});
            skLineSegment(sketch, "E405", {"start": v(26.02, 50.43) * mm, "end": v(26.06, 50.53) * mm});
            skLineSegment(sketch, "E406", {"start": v(26.06, 50.53) * mm, "end": v(26.07, 50.54) * mm});
            skLineSegment(sketch, "E407", {"start": v(26.07, 50.54) * mm, "end": v(26.13, 50.65) * mm});
            skLineSegment(sketch, "E408", {"start": v(26.13, 50.65) * mm, "end": v(26.3, 50.89) * mm});
            skLineSegment(sketch, "E409", {"start": v(26.3, 50.89) * mm, "end": v(26.3, 50.9) * mm});
            skLineSegment(sketch, "E410", {"start": v(26.3, 50.9) * mm, "end": v(26.53, 51.16) * mm});
            skLineSegment(sketch, "E411", {"start": v(26.53, 51.16) * mm, "end": v(26.54, 51.17) * mm});
            skLineSegment(sketch, "E412", {"start": v(26.54, 51.17) * mm, "end": v(26.55, 51.18) * mm});
            skLineSegment(sketch, "E413", {"start": v(26.55, 51.18) * mm, "end": v(27.11, 51.75) * mm});
            skLineSegment(sketch, "E414", {"start": v(27.11, 51.75) * mm, "end": v(27.14, 51.77) * mm});
            skLineSegment(sketch, "E415", {"start": v(27.14, 51.77) * mm, "end": v(27.07, 51.76) * mm});
            skLineSegment(sketch, "E416", {"start": v(27.07, 51.76) * mm, "end": v(25.88, 51.58) * mm});
            skLineSegment(sketch, "E417", {"start": v(25.88, 51.58) * mm, "end": v(25.81, 51.56) * mm});
            skLineSegment(sketch, "E418", {"start": v(25.81, 51.56) * mm, "end": v(24.7, 51.32) * mm});
            skLineSegment(sketch, "E419", {"start": v(24.7, 51.32) * mm, "end": v(24.64, 51.3) * mm});
            skLineSegment(sketch, "E420", {"start": v(24.64, 51.3) * mm, "end": v(23.6, 51.03) * mm});
            skLineSegment(sketch, "E421", {"start": v(23.6, 51.03) * mm, "end": v(23.57, 51.02) * mm});
            skLineSegment(sketch, "E422", {"start": v(23.57, 51.02) * mm, "end": v(22.6, 50.72) * mm});
            skLineSegment(sketch, "E423", {"start": v(22.6, 50.72) * mm, "end": v(22.55, 50.7) * mm});
            skLineSegment(sketch, "E424", {"start": v(22.55, 50.7) * mm, "end": v(22.5, 50.76) * mm});
            skLineSegment(sketch, "E425", {"start": v(22.5, 50.76) * mm, "end": v(22.5, 50.77) * mm});
            skLineSegment(sketch, "E426", {"start": v(22.5, 50.77) * mm, "end": v(22.45, 50.82) * mm});
            skLineSegment(sketch, "E427", {"start": v(22.45, 50.82) * mm, "end": v(22.44, 50.83) * mm});
            skLineSegment(sketch, "E428", {"start": v(22.44, 50.83) * mm, "end": v(22.41, 50.88) * mm});
            skLineSegment(sketch, "E429", {"start": v(22.41, 50.88) * mm, "end": v(22.4, 50.89) * mm});
            skLineSegment(sketch, "E430", {"start": v(22.4, 50.89) * mm, "end": v(22.38, 50.94) * mm});
            skLineSegment(sketch, "E431", {"start": v(22.38, 50.94) * mm, "end": v(22.38, 50.95) * mm});
            skLineSegment(sketch, "E432", {"start": v(22.38, 50.95) * mm, "end": v(22.36, 51) * mm});
            skLineSegment(sketch, "E433", {"start": v(22.36, 51) * mm, "end": v(22.36, 51) * mm});
            skLineSegment(sketch, "E434", {"start": v(22.36, 51) * mm, "end": v(22.35, 51.07) * mm});
            skLineSegment(sketch, "E435", {"start": v(22.35, 51.07) * mm, "end": v(22.35, 51.12) * mm});
            skLineSegment(sketch, "E436", {"start": v(22.35, 51.12) * mm, "end": v(22.35, 51.13) * mm});
            skLineSegment(sketch, "E437", {"start": v(22.35, 51.13) * mm, "end": v(22.35, 51.18) * mm});
            skLineSegment(sketch, "E438", {"start": v(22.35, 51.18) * mm, "end": v(22.35, 51.19) * mm});
            skLineSegment(sketch, "E439", {"start": v(22.35, 51.19) * mm, "end": v(22.36, 51.25) * mm});
            skLineSegment(sketch, "E440", {"start": v(22.36, 51.25) * mm, "end": v(22.38, 51.3) * mm});
            skLineSegment(sketch, "E441", {"start": v(22.38, 51.3) * mm, "end": v(22.38, 51.3) * mm});
            skLineSegment(sketch, "E442", {"start": v(22.38, 51.3) * mm, "end": v(22.43, 51.42) * mm});
            skLineSegment(sketch, "E443", {"start": v(22.43, 51.42) * mm, "end": v(22.44, 51.43) * mm});
            skLineSegment(sketch, "E444", {"start": v(22.44, 51.43) * mm, "end": v(22.5, 51.54) * mm});
            skLineSegment(sketch, "E445", {"start": v(22.5, 51.54) * mm, "end": v(22.51, 51.55) * mm});
            skLineSegment(sketch, "E446", {"start": v(22.51, 51.55) * mm, "end": v(22.6, 51.66) * mm});
            skLineSegment(sketch, "E447", {"start": v(22.6, 51.66) * mm, "end": v(22.62, 51.68) * mm});
            skLineSegment(sketch, "E448", {"start": v(22.62, 51.68) * mm, "end": v(23.6, 52.58) * mm});
            skLineSegment(sketch, "E449", {"start": v(23.6, 52.58) * mm, "end": v(23.64, 52.62) * mm});
            skLineSegment(sketch, "E450", {"start": v(23.64, 52.62) * mm, "end": v(22.75, 52.46) * mm});
            skLineSegment(sketch, "E451", {"start": v(22.75, 52.46) * mm, "end": v(22.72, 52.45) * mm});
            skLineSegment(sketch, "E452", {"start": v(22.72, 52.45) * mm, "end": v(21.98, 52.27) * mm});
            skLineSegment(sketch, "E453", {"start": v(21.98, 52.27) * mm, "end": v(21.93, 52.26) * mm});
            skLineSegment(sketch, "E454", {"start": v(21.93, 52.26) * mm, "end": v(21.3, 52.06) * mm});
            skLineSegment(sketch, "E455", {"start": v(21.3, 52.06) * mm, "end": v(21.25, 52.05) * mm});
            skLineSegment(sketch, "E456", {"start": v(21.25, 52.05) * mm, "end": v(20.7, 51.83) * mm});
            skLineSegment(sketch, "E457", {"start": v(20.7, 51.83) * mm, "end": v(20.66, 51.82) * mm});
            skLineSegment(sketch, "E458", {"start": v(20.66, 51.82) * mm, "end": v(20.17, 51.59) * mm});
            skLineSegment(sketch, "E459", {"start": v(20.17, 51.59) * mm, "end": v(20.14, 51.57) * mm});
            skLineSegment(sketch, "E460", {"start": v(20.14, 51.57) * mm, "end": v(19.7, 51.32) * mm});
            skLineSegment(sketch, "E461", {"start": v(19.7, 51.32) * mm, "end": v(19.68, 51.3) * mm});
            skLineSegment(sketch, "E462", {"start": v(19.68, 51.3) * mm, "end": v(18.89, 50.74) * mm});
            skLineSegment(sketch, "E463", {"start": v(18.89, 50.74) * mm, "end": v(18.86, 50.72) * mm});
            skLineSegment(sketch, "E464", {"start": v(18.86, 50.72) * mm, "end": v(18.84, 50.7) * mm});
            skLineSegment(sketch, "E465", {"start": v(18.84, 50.7) * mm, "end": v(18.7, 50.86) * mm});
            skLineSegment(sketch, "E466", {"start": v(18.7, 50.86) * mm, "end": v(18.7, 50.86) * mm});
            skLineSegment(sketch, "E467", {"start": v(18.7, 50.86) * mm, "end": v(18.6, 51) * mm});
            skLineSegment(sketch, "E468", {"start": v(18.6, 51) * mm, "end": v(18.59, 51.02) * mm});
            skLineSegment(sketch, "E469", {"start": v(18.59, 51.02) * mm, "end": v(18.52, 51.16) * mm});
            skLineSegment(sketch, "E470", {"start": v(18.52, 51.16) * mm, "end": v(18.52, 51.17) * mm});
            skLineSegment(sketch, "E471", {"start": v(18.52, 51.17) * mm, "end": v(18.5, 51.23) * mm});
            skLineSegment(sketch, "E472", {"start": v(18.5, 51.23) * mm, "end": v(18.5, 51.24) * mm});
            skLineSegment(sketch, "E473", {"start": v(18.5, 51.24) * mm, "end": v(18.48, 51.3) * mm});
            skLineSegment(sketch, "E474", {"start": v(18.48, 51.3) * mm, "end": v(18.48, 51.31) * mm});
            skLineSegment(sketch, "E475", {"start": v(18.48, 51.31) * mm, "end": v(18.47, 51.38) * mm});
            skLineSegment(sketch, "E476", {"start": v(18.47, 51.38) * mm, "end": v(18.46, 51.45) * mm});
            skLineSegment(sketch, "E477", {"start": v(18.46, 51.45) * mm, "end": v(18.46, 51.45) * mm});
            skLineSegment(sketch, "E478", {"start": v(18.46, 51.45) * mm, "end": v(18.48, 51.58) * mm});
            skLineSegment(sketch, "E479", {"start": v(18.48, 51.58) * mm, "end": v(18.48, 51.59) * mm});
            skLineSegment(sketch, "E480", {"start": v(18.48, 51.59) * mm, "end": v(18.48, 51.59) * mm});
            skLineSegment(sketch, "E481", {"start": v(18.48, 51.59) * mm, "end": v(18.51, 51.72) * mm});
            skLineSegment(sketch, "E482", {"start": v(18.51, 51.72) * mm, "end": v(18.51, 51.72) * mm});
            skLineSegment(sketch, "E483", {"start": v(18.51, 51.72) * mm, "end": v(18.56, 51.85) * mm});
            skLineSegment(sketch, "E484", {"start": v(18.56, 51.85) * mm, "end": v(18.57, 51.86) * mm});
            skLineSegment(sketch, "E485", {"start": v(18.57, 51.86) * mm, "end": v(18.7, 52.1) * mm});
            skLineSegment(sketch, "E486", {"start": v(18.7, 52.1) * mm, "end": v(18.71, 52.1) * mm});
            skLineSegment(sketch, "E487", {"start": v(18.71, 52.1) * mm, "end": v(18.89, 52.34) * mm});
            skLineSegment(sketch, "E488", {"start": v(18.89, 52.34) * mm, "end": v(18.9, 52.35) * mm});
            skLineSegment(sketch, "E489", {"start": v(18.9, 52.35) * mm, "end": v(18.9, 52.35) * mm});
            skLineSegment(sketch, "E490", {"start": v(18.9, 52.35) * mm, "end": v(19.26, 52.82) * mm});
            skLineSegment(sketch, "E491", {"start": v(19.26, 52.82) * mm, "end": v(19.28, 52.84) * mm});
            skLineSegment(sketch, "E492", {"start": v(19.28, 52.84) * mm, "end": v(18.53, 52.53) * mm});
            skLineSegment(sketch, "E493", {"start": v(18.53, 52.53) * mm, "end": v(18.5, 52.51) * mm});
            skLineSegment(sketch, "E494", {"start": v(18.5, 52.51) * mm, "end": v(17.85, 52.2) * mm});
            skLineSegment(sketch, "E495", {"start": v(17.85, 52.2) * mm, "end": v(17.81, 52.19) * mm});
            skLineSegment(sketch, "E496", {"start": v(17.81, 52.19) * mm, "end": v(17.25, 51.88) * mm});
            skLineSegment(sketch, "E497", {"start": v(17.25, 51.88) * mm, "end": v(17.21, 51.86) * mm});
            skLineSegment(sketch, "E498", {"start": v(17.21, 51.86) * mm, "end": v(16.7, 51.55) * mm});
            skLineSegment(sketch, "E499", {"start": v(16.7, 51.55) * mm, "end": v(16.64, 51.5) * mm});
            skLineSegment(sketch, "E500", {"start": v(16.64, 51.5) * mm, "end": v(15.76, 50.84) * mm});
            skLineSegment(sketch, "E501", {"start": v(15.76, 50.84) * mm, "end": v(15.74, 50.83) * mm});
            skLineSegment(sketch, "E502", {"start": v(15.74, 50.83) * mm, "end": v(14.96, 50.11) * mm});
            skLineSegment(sketch, "E503", {"start": v(14.96, 50.11) * mm, "end": v(14.93, 50.1) * mm});
            skLineSegment(sketch, "E504", {"start": v(14.93, 50.1) * mm, "end": v(14.9, 50.07) * mm});
            skLineSegment(sketch, "E505", {"start": v(14.9, 50.07) * mm, "end": v(14.9, 50.08) * mm});
            skLineSegment(sketch, "E506", {"start": v(14.9, 50.08) * mm, "end": v(14.6, 50.4) * mm});
            skLineSegment(sketch, "E507", {"start": v(14.6, 50.4) * mm, "end": v(14.6, 50.4) * mm});
            skLineSegment(sketch, "E508", {"start": v(14.6, 50.4) * mm, "end": v(14.48, 50.58) * mm});
            skLineSegment(sketch, "E509", {"start": v(14.48, 50.58) * mm, "end": v(14.47, 50.58) * mm});
            skLineSegment(sketch, "E510", {"start": v(14.47, 50.58) * mm, "end": v(14.43, 50.68) * mm});
            skLineSegment(sketch, "E511", {"start": v(14.43, 50.68) * mm, "end": v(14.42, 50.69) * mm});
            skLineSegment(sketch, "E512", {"start": v(14.42, 50.69) * mm, "end": v(14.39, 50.79) * mm});
            skLineSegment(sketch, "E513", {"start": v(14.39, 50.79) * mm, "end": v(14.37, 50.9) * mm});
            skLineSegment(sketch, "E514", {"start": v(14.37, 50.9) * mm, "end": v(14.36, 50.9) * mm});
            skLineSegment(sketch, "E515", {"start": v(14.36, 50.9) * mm, "end": v(14.36, 51.02) * mm});
            skLineSegment(sketch, "E516", {"start": v(14.36, 51.02) * mm, "end": v(14.36, 51.03) * mm});
            skLineSegment(sketch, "E517", {"start": v(14.36, 51.03) * mm, "end": v(14.36, 51.15) * mm});
            skLineSegment(sketch, "E518", {"start": v(14.36, 51.15) * mm, "end": v(14.36, 51.16) * mm});
            skLineSegment(sketch, "E519", {"start": v(14.36, 51.16) * mm, "end": v(14.39, 51.3) * mm});
            skLineSegment(sketch, "E520", {"start": v(14.39, 51.3) * mm, "end": v(14.43, 51.44) * mm});
            skLineSegment(sketch, "E521", {"start": v(14.43, 51.44) * mm, "end": v(14.43, 51.45) * mm});
            skLineSegment(sketch, "E522", {"start": v(14.43, 51.45) * mm, "end": v(14.49, 51.6) * mm});
            skLineSegment(sketch, "E523", {"start": v(14.49, 51.6) * mm, "end": v(14.5, 51.62) * mm});
            skLineSegment(sketch, "E524", {"start": v(14.5, 51.62) * mm, "end": v(14.68, 51.97) * mm});
            skLineSegment(sketch, "E525", {"start": v(14.68, 51.97) * mm, "end": v(14.69, 51.98) * mm});
            skLineSegment(sketch, "E526", {"start": v(14.69, 51.98) * mm, "end": v(13.78, 51.36) * mm});
            skLineSegment(sketch, "E527", {"start": v(13.78, 51.36) * mm, "end": v(13.74, 51.34) * mm});
            skLineSegment(sketch, "E528", {"start": v(13.74, 51.34) * mm, "end": v(12.93, 50.71) * mm});
            skLineSegment(sketch, "E529", {"start": v(12.93, 50.71) * mm, "end": v(12.87, 50.67) * mm});
            skLineSegment(sketch, "E530", {"start": v(12.87, 50.67) * mm, "end": v(12.14, 50) * mm});
            skLineSegment(sketch, "E531", {"start": v(12.14, 50) * mm, "end": v(12.1, 49.97) * mm});
            skLineSegment(sketch, "E532", {"start": v(12.1, 49.97) * mm, "end": v(11.45, 49.25) * mm});
            skLineSegment(sketch, "E533", {"start": v(11.45, 49.25) * mm, "end": v(11.41, 49.22) * mm});
            skLineSegment(sketch, "E534", {"start": v(11.41, 49.22) * mm, "end": v(11.27, 49.33) * mm});
            skLineSegment(sketch, "E535", {"start": v(11.27, 49.33) * mm, "end": v(11.26, 49.34) * mm});
            skLineSegment(sketch, "E536", {"start": v(11.26, 49.34) * mm, "end": v(11.15, 49.45) * mm});
            skLineSegment(sketch, "E537", {"start": v(11.15, 49.45) * mm, "end": v(11.14, 49.46) * mm});
            skLineSegment(sketch, "E538", {"start": v(11.14, 49.46) * mm, "end": v(11.05, 49.57) * mm});
            skLineSegment(sketch, "E539", {"start": v(11.05, 49.57) * mm, "end": v(11.05, 49.57) * mm});
            skLineSegment(sketch, "E540", {"start": v(11.05, 49.57) * mm, "end": v(11.05, 49.58) * mm});
            skLineSegment(sketch, "E541", {"start": v(11.05, 49.58) * mm, "end": v(10.98, 49.7) * mm});
            skLineSegment(sketch, "E542", {"start": v(10.98, 49.7) * mm, "end": v(10.98, 49.7) * mm});
            skLineSegment(sketch, "E543", {"start": v(10.98, 49.7) * mm, "end": v(10.93, 49.81) * mm});
            skLineSegment(sketch, "E544", {"start": v(10.93, 49.81) * mm, "end": v(10.92, 49.82) * mm});
            skLineSegment(sketch, "E545", {"start": v(10.92, 49.82) * mm, "end": v(10.9, 49.93) * mm});
            skLineSegment(sketch, "E546", {"start": v(10.9, 49.93) * mm, "end": v(10.9, 49.94) * mm});
            skLineSegment(sketch, "E547", {"start": v(10.9, 49.94) * mm, "end": v(10.87, 50.05) * mm});
            skLineSegment(sketch, "E548", {"start": v(10.87, 50.05) * mm, "end": v(10.87, 50.06) * mm});
            skLineSegment(sketch, "E549", {"start": v(10.87, 50.06) * mm, "end": v(10.87, 50.17) * mm});
            skLineSegment(sketch, "E550", {"start": v(10.87, 50.17) * mm, "end": v(10.87, 50.19) * mm});
            skLineSegment(sketch, "E551", {"start": v(10.87, 50.19) * mm, "end": v(10.97, 51.09) * mm});
            skLineSegment(sketch, "E552", {"start": v(10.97, 51.09) * mm, "end": v(10.98, 51.13) * mm});
            skLineSegment(sketch, "E553", {"start": v(10.98, 51.13) * mm, "end": v(10.95, 51.12) * mm});
            skLineSegment(sketch, "E554", {"start": v(10.95, 51.12) * mm, "end": v(9.98, 50.33) * mm});
            skLineSegment(sketch, "E555", {"start": v(9.98, 50.33) * mm, "end": v(9.92, 50.28) * mm});
            skLineSegment(sketch, "E556", {"start": v(9.92, 50.28) * mm, "end": v(9.1, 49.44) * mm});
            skLineSegment(sketch, "E557", {"start": v(9.1, 49.44) * mm, "end": v(9.06, 49.4) * mm});
            skLineSegment(sketch, "E558", {"start": v(9.06, 49.4) * mm, "end": v(7.57, 47.62) * mm});
            skLineSegment(sketch, "E559", {"start": v(7.57, 47.62) * mm, "end": v(7.48, 47.51) * mm});
            skLineSegment(sketch, "E560", {"start": v(7.48, 47.51) * mm, "end": v(7.48, 47.52) * mm});
            skLineSegment(sketch, "E561", {"start": v(7.48, 47.52) * mm, "end": v(7.4, 47.6) * mm});
            skLineSegment(sketch, "E562", {"start": v(7.4, 47.6) * mm, "end": v(7.4, 47.6) * mm});
            skLineSegment(sketch, "E563", {"start": v(7.4, 47.6) * mm, "end": v(7.32, 47.71) * mm});
            skLineSegment(sketch, "E564", {"start": v(7.32, 47.71) * mm, "end": v(7.31, 47.73) * mm});
            skLineSegment(sketch, "E565", {"start": v(7.31, 47.73) * mm, "end": v(7.16, 48.01) * mm});
            skLineSegment(sketch, "E566", {"start": v(8, -17.24) * mm, "end": v(7.96, -17.2) * mm});
            skLineSegment(sketch, "E567", {"start": v(7.96, -17.2) * mm, "end": v(6.75, -16.24) * mm});
            skLineSegment(sketch, "E568", {"start": v(6.75, -16.24) * mm, "end": v(6.7, -16.2) * mm});
            skLineSegment(sketch, "E569", {"start": v(6.7, -16.2) * mm, "end": v(5.36, -15.39) * mm});
            skLineSegment(sketch, "E570", {"start": v(5.36, -15.39) * mm, "end": v(5.32, -15.36) * mm});
            skLineSegment(sketch, "E571", {"start": v(5.32, -15.36) * mm, "end": v(3.87, -14.71) * mm});
            skLineSegment(sketch, "E572", {"start": v(3.87, -14.71) * mm, "end": v(3.83, -14.7) * mm});
            skLineSegment(sketch, "E573", {"start": v(3.83, -14.7) * mm, "end": v(2.3, -14.22) * mm});
            skLineSegment(sketch, "E574", {"start": v(2.3, -14.22) * mm, "end": v(2.25, -14.2) * mm});
            skLineSegment(sketch, "E575", {"start": v(2.25, -14.2) * mm, "end": v(0.67, -13.92) * mm});
            skLineSegment(sketch, "E576", {"start": v(0.67, -13.92) * mm, "end": v(0.62, -13.9) * mm});
            skLineSegment(sketch, "E577", {"start": v(0.62, -13.9) * mm, "end": v(-1, -13.81) * mm});
            skLineSegment(sketch, "E578", {"start": v(-1, -13.81) * mm, "end": v(-1.04, -13.8) * mm});
            skLineSegment(sketch, "E579", {"start": v(-1.04, -13.8) * mm, "end": v(-2.65, -13.9) * mm});
            skLineSegment(sketch, "E580", {"start": v(-2.65, -13.9) * mm, "end": v(-2.7, -13.9) * mm});
            skLineSegment(sketch, "E581", {"start": v(-2.7, -13.9) * mm, "end": v(-4.29, -14.2) * mm});
            skLineSegment(sketch, "E582", {"start": v(-4.29, -14.2) * mm, "end": v(-4.33, -14.2) * mm});
            skLineSegment(sketch, "E583", {"start": v(-4.33, -14.2) * mm, "end": v(-5.87, -14.68) * mm});
            skLineSegment(sketch, "E584", {"start": v(-5.87, -14.68) * mm, "end": v(-5.91, -14.7) * mm});
            skLineSegment(sketch, "E585", {"start": v(-5.91, -14.7) * mm, "end": v(-7.36, -15.34) * mm});
            skLineSegment(sketch, "E586", {"start": v(-7.36, -15.34) * mm, "end": v(-7.4, -15.36) * mm});
            skLineSegment(sketch, "E587", {"start": v(-7.4, -15.36) * mm, "end": v(-8.75, -16.18) * mm});
            skLineSegment(sketch, "E588", {"start": v(-8.75, -16.18) * mm, "end": v(-8.79, -16.2) * mm});
            skLineSegment(sketch, "E589", {"start": v(-8.79, -16.2) * mm, "end": v(-10, -17.18) * mm});
            skLineSegment(sketch, "E590", {"start": v(-10, -17.18) * mm, "end": v(-10.04, -17.2) * mm});
            skLineSegment(sketch, "E591", {"start": v(-10.04, -17.2) * mm, "end": v(-11.1, -18.32) * mm});
            skLineSegment(sketch, "E592", {"start": v(-11.1, -18.32) * mm, "end": v(-11.14, -18.35) * mm});
            skLineSegment(sketch, "E593", {"start": v(-11.14, -18.35) * mm, "end": v(-12.04, -19.58) * mm});
            skLineSegment(sketch, "E594", {"start": v(-12.04, -19.58) * mm, "end": v(-12.06, -19.61) * mm});
            skLineSegment(sketch, "E595", {"start": v(-12.06, -19.61) * mm, "end": v(-12.78, -20.93) * mm});
            skLineSegment(sketch, "E596", {"start": v(-12.78, -20.93) * mm, "end": v(-12.8, -20.97) * mm});
            skLineSegment(sketch, "E597", {"start": v(-12.8, -20.97) * mm, "end": v(-13.32, -22.37) * mm});
            skLineSegment(sketch, "E598", {"start": v(-13.32, -22.37) * mm, "end": v(-13.34, -22.4) * mm});
            skLineSegment(sketch, "E599", {"start": v(-13.34, -22.4) * mm, "end": v(-13.65, -23.86) * mm});
            skLineSegment(sketch, "E600", {"start": v(-13.65, -23.86) * mm, "end": v(-13.66, -23.9) * mm});
            skLineSegment(sketch, "E601", {"start": v(-13.66, -23.9) * mm, "end": v(-13.77, -25.37) * mm});
            skLineSegment(sketch, "E602", {"start": v(-13.77, -25.37) * mm, "end": v(-13.77, -25.41) * mm});
            skLineSegment(sketch, "E603", {"start": v(-13.77, -25.41) * mm, "end": v(-13.66, -26.88) * mm});
            skLineSegment(sketch, "E604", {"start": v(-13.66, -26.88) * mm, "end": v(-13.66, -26.93) * mm});
            skLineSegment(sketch, "E605", {"start": v(-13.66, -26.93) * mm, "end": v(-13.35, -28.38) * mm});
            skLineSegment(sketch, "E606", {"start": v(-13.35, -28.38) * mm, "end": v(-13.34, -28.42) * mm});
            skLineSegment(sketch, "E607", {"start": v(-13.34, -28.42) * mm, "end": v(-12.82, -29.81) * mm});
            skLineSegment(sketch, "E608", {"start": v(-12.82, -29.81) * mm, "end": v(-12.8, -29.86) * mm});
            skLineSegment(sketch, "E609", {"start": v(-12.8, -29.86) * mm, "end": v(-12.09, -31.18) * mm});
            skLineSegment(sketch, "E610", {"start": v(-12.09, -31.18) * mm, "end": v(-12.06, -31.22) * mm});
            skLineSegment(sketch, "E611", {"start": v(-12.06, -31.22) * mm, "end": v(-11.17, -32.44) * mm});
            skLineSegment(sketch, "E612", {"start": v(-11.17, -32.44) * mm, "end": v(-11.14, -32.48) * mm});
            skLineSegment(sketch, "E613", {"start": v(-11.14, -32.48) * mm, "end": v(-10.07, -33.59) * mm});
            skLineSegment(sketch, "E614", {"start": v(-10.07, -33.59) * mm, "end": v(-10.04, -33.62) * mm});
            skLineSegment(sketch, "E615", {"start": v(-10.04, -33.62) * mm, "end": v(-8.83, -34.6) * mm});
            skLineSegment(sketch, "E616", {"start": v(-8.83, -34.6) * mm, "end": v(-8.79, -34.62) * mm});
            skLineSegment(sketch, "E617", {"start": v(-8.79, -34.62) * mm, "end": v(-7.44, -35.44) * mm});
            skLineSegment(sketch, "E618", {"start": v(-7.44, -35.44) * mm, "end": v(-7.4, -35.47) * mm});
            skLineSegment(sketch, "E619", {"start": v(-7.4, -35.47) * mm, "end": v(-5.95, -36.12) * mm});
            skLineSegment(sketch, "E620", {"start": v(-5.95, -36.12) * mm, "end": v(-5.91, -36.14) * mm});
            skLineSegment(sketch, "E621", {"start": v(-5.91, -36.14) * mm, "end": v(-4.38, -36.61) * mm});
            skLineSegment(sketch, "E622", {"start": v(-4.38, -36.61) * mm, "end": v(-4.33, -36.62) * mm});
            skLineSegment(sketch, "E623", {"start": v(-4.33, -36.62) * mm, "end": v(-2.75, -36.91) * mm});
            skLineSegment(sketch, "E624", {"start": v(-2.75, -36.91) * mm, "end": v(-2.7, -36.92) * mm});
            skLineSegment(sketch, "E625", {"start": v(-2.7, -36.92) * mm, "end": v(-1.09, -37.02) * mm});
            skLineSegment(sketch, "E626", {"start": v(-1.09, -37.02) * mm, "end": v(-1.04, -37.02) * mm});
            skLineSegment(sketch, "E627", {"start": v(-1.04, -37.02) * mm, "end": v(0.57, -36.92) * mm});
            skLineSegment(sketch, "E628", {"start": v(0.57, -36.92) * mm, "end": v(0.62, -36.92) * mm});
            skLineSegment(sketch, "E629", {"start": v(0.62, -36.92) * mm, "end": v(2.2, -36.63) * mm});
            skLineSegment(sketch, "E630", {"start": v(2.2, -36.63) * mm, "end": v(2.25, -36.62) * mm});
            skLineSegment(sketch, "E631", {"start": v(2.25, -36.62) * mm, "end": v(3.78, -36.15) * mm});
            skLineSegment(sketch, "E632", {"start": v(3.78, -36.15) * mm, "end": v(3.83, -36.14) * mm});
            skLineSegment(sketch, "E633", {"start": v(3.83, -36.14) * mm, "end": v(5.28, -35.48) * mm});
            skLineSegment(sketch, "E634", {"start": v(5.28, -35.48) * mm, "end": v(5.32, -35.47) * mm});
            skLineSegment(sketch, "E635", {"start": v(5.32, -35.47) * mm, "end": v(6.67, -34.65) * mm});
            skLineSegment(sketch, "E636", {"start": v(6.67, -34.65) * mm, "end": v(6.7, -34.62) * mm});
            skLineSegment(sketch, "E637", {"start": v(6.7, -34.62) * mm, "end": v(7.92, -33.65) * mm});
            skLineSegment(sketch, "E638", {"start": v(7.92, -33.65) * mm, "end": v(7.96, -33.62) * mm});
            skLineSegment(sketch, "E639", {"start": v(7.96, -33.62) * mm, "end": v(9.03, -32.51) * mm});
            skLineSegment(sketch, "E640", {"start": v(9.03, -32.51) * mm, "end": v(9.06, -32.48) * mm});
            skLineSegment(sketch, "E641", {"start": v(9.06, -32.48) * mm, "end": v(9.96, -31.25) * mm});
            skLineSegment(sketch, "E642", {"start": v(9.96, -31.25) * mm, "end": v(9.98, -31.22) * mm});
            skLineSegment(sketch, "E643", {"start": v(9.98, -31.22) * mm, "end": v(10.7, -29.9) * mm});
            skLineSegment(sketch, "E644", {"start": v(10.7, -29.9) * mm, "end": v(10.72, -29.86) * mm});
            skLineSegment(sketch, "E645", {"start": v(10.72, -29.86) * mm, "end": v(11.24, -28.46) * mm});
            skLineSegment(sketch, "E646", {"start": v(11.24, -28.46) * mm, "end": v(11.26, -28.42) * mm});
            skLineSegment(sketch, "E647", {"start": v(11.26, -28.42) * mm, "end": v(11.57, -26.97) * mm});
            skLineSegment(sketch, "E648", {"start": v(11.57, -26.97) * mm, "end": v(11.58, -26.93) * mm});
            skLineSegment(sketch, "E649", {"start": v(11.58, -26.93) * mm, "end": v(11.69, -25.46) * mm});
            skLineSegment(sketch, "E650", {"start": v(11.69, -25.46) * mm, "end": v(11.69, -25.41) * mm});
            skLineSegment(sketch, "E651", {"start": v(11.69, -25.41) * mm, "end": v(11.58, -23.94) * mm});
            skLineSegment(sketch, "E652", {"start": v(11.58, -23.94) * mm, "end": v(11.58, -23.9) * mm});
            skLineSegment(sketch, "E653", {"start": v(11.58, -23.9) * mm, "end": v(11.26, -22.45) * mm});
            skLineSegment(sketch, "E654", {"start": v(11.26, -22.45) * mm, "end": v(11.26, -22.4) * mm});
            skLineSegment(sketch, "E655", {"start": v(11.26, -22.4) * mm, "end": v(10.74, -21.02) * mm});
            skLineSegment(sketch, "E656", {"start": v(10.74, -21.02) * mm, "end": v(10.72, -20.97) * mm});
            skLineSegment(sketch, "E657", {"start": v(10.72, -20.97) * mm, "end": v(10, -19.65) * mm});
            skLineSegment(sketch, "E658", {"start": v(10, -19.65) * mm, "end": v(9.98, -19.61) * mm});
            skLineSegment(sketch, "E659", {"start": v(9.98, -19.61) * mm, "end": v(9.08, -18.39) * mm});
            skLineSegment(sketch, "E660", {"start": v(9.08, -18.39) * mm, "end": v(9.06, -18.35) * mm});
            skLineSegment(sketch, "E661", {"start": v(9.06, -18.35) * mm, "end": v(8, -17.24) * mm});
            skLineSegment(sketch, "E662", {"start": v(25.81, -2.84) * mm, "end": v(25.56, -1.65) * mm});
            skLineSegment(sketch, "E663", {"start": v(25.56, -1.65) * mm, "end": v(25.54, -1.58) * mm});
            skLineSegment(sketch, "E664", {"start": v(25.54, -1.58) * mm, "end": v(25.18, -0.39) * mm});
            skLineSegment(sketch, "E665", {"start": v(25.18, -0.39) * mm, "end": v(25.16, -0.32) * mm});
            skLineSegment(sketch, "E666", {"start": v(25.16, -0.32) * mm, "end": v(24.69, 0.86) * mm});
            skLineSegment(sketch, "E667", {"start": v(24.69, 0.86) * mm, "end": v(24.66, 0.93) * mm});
            skLineSegment(sketch, "E668", {"start": v(24.66, 0.93) * mm, "end": v(24.07, 2.09) * mm});
            skLineSegment(sketch, "E669", {"start": v(24.07, 2.09) * mm, "end": v(24.03, 2.16) * mm});
            skLineSegment(sketch, "E670", {"start": v(24.03, 2.16) * mm, "end": v(23.33, 3.29) * mm});
            skLineSegment(sketch, "E671", {"start": v(23.33, 3.29) * mm, "end": v(23.29, 3.36) * mm});
            skLineSegment(sketch, "E672", {"start": v(23.29, 3.36) * mm, "end": v(22.5, 4.46) * mm});
            skLineSegment(sketch, "E673", {"start": v(22.5, 4.46) * mm, "end": v(22.48, 4.5) * mm});
            skLineSegment(sketch, "E674", {"start": v(22.48, 4.5) * mm, "end": v(21.65, 5.48) * mm});
            skLineSegment(sketch, "E675", {"start": v(21.65, 5.48) * mm, "end": v(21.6, 5.55) * mm});
            skLineSegment(sketch, "E676", {"start": v(21.6, 5.55) * mm, "end": v(20.7, 6.44) * mm});
            skLineSegment(sketch, "E677", {"start": v(20.7, 6.44) * mm, "end": v(20.64, 6.5) * mm});
            skLineSegment(sketch, "E678", {"start": v(20.64, 6.5) * mm, "end": v(19.7, 7.28) * mm});
            skLineSegment(sketch, "E679", {"start": v(19.7, 7.28) * mm, "end": v(19.62, 7.34) * mm});
            skLineSegment(sketch, "E680", {"start": v(19.62, 7.34) * mm, "end": v(18.63, 8.02) * mm});
            skLineSegment(sketch, "E681", {"start": v(18.63, 8.02) * mm, "end": v(18.56, 8.07) * mm});
            skLineSegment(sketch, "E682", {"start": v(18.56, 8.07) * mm, "end": v(17.52, 8.65) * mm});
            skLineSegment(sketch, "E683", {"start": v(17.52, 8.65) * mm, "end": v(17.45, 8.69) * mm});
            skLineSegment(sketch, "E684", {"start": v(17.45, 8.69) * mm, "end": v(16.38, 9.17) * mm});
            skLineSegment(sketch, "E685", {"start": v(16.38, 9.17) * mm, "end": v(16.3, 9.2) * mm});
            skLineSegment(sketch, "E686", {"start": v(16.3, 9.2) * mm, "end": v(15.22, 9.57) * mm});
            skLineSegment(sketch, "E687", {"start": v(15.22, 9.57) * mm, "end": v(15.14, 9.59) * mm});
            skLineSegment(sketch, "E688", {"start": v(15.14, 9.59) * mm, "end": v(14.04, 9.85) * mm});
            skLineSegment(sketch, "E689", {"start": v(14.04, 9.85) * mm, "end": v(13.98, 9.86) * mm});
            skLineSegment(sketch, "E690", {"start": v(13.98, 9.86) * mm, "end": v(12.87, 10.01) * mm});
            skLineSegment(sketch, "E691", {"start": v(12.87, 10.01) * mm, "end": v(12.8, 10.01) * mm});
            skLineSegment(sketch, "E692", {"start": v(12.8, 10.01) * mm, "end": v(11.7, 10.05) * mm});
            skLineSegment(sketch, "E693", {"start": v(11.7, 10.05) * mm, "end": v(11.64, 10.05) * mm});
            skLineSegment(sketch, "E694", {"start": v(11.64, 10.05) * mm, "end": v(10.54, 9.97) * mm});
            skLineSegment(sketch, "E695", {"start": v(10.54, 9.97) * mm, "end": v(10.48, 9.96) * mm});
            skLineSegment(sketch, "E696", {"start": v(10.48, 9.96) * mm, "end": v(9.4, 9.76) * mm});
            skLineSegment(sketch, "E697", {"start": v(9.4, 9.76) * mm, "end": v(9.34, 9.75) * mm});
            skLineSegment(sketch, "E698", {"start": v(9.34, 9.75) * mm, "end": v(8.29, 9.42) * mm});
            skLineSegment(sketch, "E699", {"start": v(8.29, 9.42) * mm, "end": v(8.23, 9.4) * mm});
            skLineSegment(sketch, "E700", {"start": v(8.23, 9.4) * mm, "end": v(7.2, 8.96) * mm});
            skLineSegment(sketch, "E701", {"start": v(7.2, 8.96) * mm, "end": v(7.15, 8.93) * mm});
            skLineSegment(sketch, "E702", {"start": v(7.15, 8.93) * mm, "end": v(6.17, 8.36) * mm});
            skLineSegment(sketch, "E703", {"start": v(6.17, 8.36) * mm, "end": v(6.12, 8.33) * mm});
            skLineSegment(sketch, "E704", {"start": v(6.12, 8.33) * mm, "end": v(5.18, 7.66) * mm});
            skLineSegment(sketch, "E705", {"start": v(5.18, 7.66) * mm, "end": v(5.16, 7.64) * mm});
            skLineSegment(sketch, "E706", {"start": v(5.16, 7.64) * mm, "end": v(4.35, 6.9) * mm});
            skLineSegment(sketch, "E707", {"start": v(4.35, 6.9) * mm, "end": v(4.3, 6.85) * mm});
            skLineSegment(sketch, "E708", {"start": v(4.3, 6.85) * mm, "end": v(3.6, 6.03) * mm});
            skLineSegment(sketch, "E709", {"start": v(3.6, 6.03) * mm, "end": v(3.55, 5.98) * mm});
            skLineSegment(sketch, "E710", {"start": v(3.55, 5.98) * mm, "end": v(2.95, 5.09) * mm});
            skLineSegment(sketch, "E711", {"start": v(2.95, 5.09) * mm, "end": v(2.9, 5.03) * mm});
            skLineSegment(sketch, "E712", {"start": v(2.9, 5.03) * mm, "end": v(2.4, 4.07) * mm});
            skLineSegment(sketch, "E713", {"start": v(2.4, 4.07) * mm, "end": v(2.38, 4) * mm});
            skLineSegment(sketch, "E714", {"start": v(2.38, 4) * mm, "end": v(1.98, 2.99) * mm});
            skLineSegment(sketch, "E715", {"start": v(1.98, 2.99) * mm, "end": v(1.96, 2.92) * mm});
            skLineSegment(sketch, "E716", {"start": v(1.96, 2.92) * mm, "end": v(1.67, 1.85) * mm});
            skLineSegment(sketch, "E717", {"start": v(1.67, 1.85) * mm, "end": v(1.65, 1.78) * mm});
            skLineSegment(sketch, "E718", {"start": v(1.65, 1.78) * mm, "end": v(1.47, 0.68) * mm});
            skLineSegment(sketch, "E719", {"start": v(1.47, 0.68) * mm, "end": v(1.46, 0.6) * mm});
            skLineSegment(sketch, "E720", {"start": v(1.46, 0.6) * mm, "end": v(1.38, -0.54) * mm});
            skLineSegment(sketch, "E721", {"start": v(1.38, -0.54) * mm, "end": v(1.38, -0.6) * mm});
            skLineSegment(sketch, "E722", {"start": v(1.38, -0.6) * mm, "end": v(1.41, -1.77) * mm});
            skLineSegment(sketch, "E723", {"start": v(1.41, -1.77) * mm, "end": v(1.42, -1.84) * mm});
            skLineSegment(sketch, "E724", {"start": v(1.42, -1.84) * mm, "end": v(1.56, -3.02) * mm});
            skLineSegment(sketch, "E725", {"start": v(1.56, -3.02) * mm, "end": v(1.57, -3.1) * mm});
            skLineSegment(sketch, "E726", {"start": v(1.57, -3.1) * mm, "end": v(1.82, -4.28) * mm});
            skLineSegment(sketch, "E727", {"start": v(1.82, -4.28) * mm, "end": v(1.83, -4.35) * mm});
            skLineSegment(sketch, "E728", {"start": v(1.83, -4.35) * mm, "end": v(2.2, -5.54) * mm});
            skLineSegment(sketch, "E729", {"start": v(2.2, -5.54) * mm, "end": v(2.22, -5.61) * mm});
            skLineSegment(sketch, "E730", {"start": v(2.22, -5.61) * mm, "end": v(2.7, -6.79) * mm});
            skLineSegment(sketch, "E731", {"start": v(2.7, -6.79) * mm, "end": v(2.72, -6.86) * mm});
            skLineSegment(sketch, "E732", {"start": v(2.72, -6.86) * mm, "end": v(3.3, -8.02) * mm});
            skLineSegment(sketch, "E733", {"start": v(3.3, -8.02) * mm, "end": v(3.34, -8.09) * mm});
            skLineSegment(sketch, "E734", {"start": v(3.34, -8.09) * mm, "end": v(4.05, -9.22) * mm});
            skLineSegment(sketch, "E735", {"start": v(4.05, -9.22) * mm, "end": v(4.09, -9.29) * mm});
            skLineSegment(sketch, "E736", {"start": v(4.09, -9.29) * mm, "end": v(4.9, -10.35) * mm});
            skLineSegment(sketch, "E737", {"start": v(4.9, -10.35) * mm, "end": v(4.94, -10.4) * mm});
            skLineSegment(sketch, "E738", {"start": v(4.94, -10.4) * mm, "end": v(5.8, -11.34) * mm});
            skLineSegment(sketch, "E739", {"start": v(5.8, -11.34) * mm, "end": v(5.86, -11.4) * mm});
            skLineSegment(sketch, "E740", {"start": v(5.86, -11.4) * mm, "end": v(6.78, -12.27) * mm});
            skLineSegment(sketch, "E741", {"start": v(6.78, -12.27) * mm, "end": v(6.85, -12.33) * mm});
            skLineSegment(sketch, "E742", {"start": v(6.85, -12.33) * mm, "end": v(7.82, -13.1) * mm});
            skLineSegment(sketch, "E743", {"start": v(7.82, -13.1) * mm, "end": v(7.9, -13.14) * mm});
            skLineSegment(sketch, "E744", {"start": v(7.9, -13.14) * mm, "end": v(8.9, -13.81) * mm});
            skLineSegment(sketch, "E745", {"start": v(8.9, -13.81) * mm, "end": v(8.98, -13.86) * mm});
            skLineSegment(sketch, "E746", {"start": v(8.98, -13.86) * mm, "end": v(10.02, -14.43) * mm});
            skLineSegment(sketch, "E747", {"start": v(10.02, -14.43) * mm, "end": v(10.1, -14.46) * mm});
            skLineSegment(sketch, "E748", {"start": v(10.1, -14.46) * mm, "end": v(11.17, -14.94) * mm});
            skLineSegment(sketch, "E749", {"start": v(11.17, -14.94) * mm, "end": v(12.26, -15.3) * mm});
            skLineSegment(sketch, "E750", {"start": v(12.26, -15.3) * mm, "end": v(12.34, -15.34) * mm});
            skLineSegment(sketch, "E751", {"start": v(12.34, -15.34) * mm, "end": v(13.44, -15.6) * mm});
            skLineSegment(sketch, "E752", {"start": v(13.44, -15.6) * mm, "end": v(13.52, -15.62) * mm});
            skLineSegment(sketch, "E753", {"start": v(13.52, -15.62) * mm, "end": v(14.62, -15.78) * mm});
            skLineSegment(sketch, "E754", {"start": v(14.62, -15.78) * mm, "end": v(14.68, -15.79) * mm});
            skLineSegment(sketch, "E755", {"start": v(14.68, -15.79) * mm, "end": v(15.78, -15.84) * mm});
            skLineSegment(sketch, "E756", {"start": v(15.78, -15.84) * mm, "end": v(15.83, -15.84) * mm});
            skLineSegment(sketch, "E757", {"start": v(15.83, -15.84) * mm, "end": v(15.89, -15.84) * mm});
            skLineSegment(sketch, "E758", {"start": v(15.89, -15.84) * mm, "end": v(16.97, -15.77) * mm});
            skLineSegment(sketch, "E759", {"start": v(16.97, -15.77) * mm, "end": v(17.03, -15.76) * mm});
            skLineSegment(sketch, "E760", {"start": v(17.03, -15.76) * mm, "end": v(18.09, -15.59) * mm});
            skLineSegment(sketch, "E761", {"start": v(18.09, -15.59) * mm, "end": v(18.14, -15.57) * mm});
            skLineSegment(sketch, "E762", {"start": v(18.14, -15.57) * mm, "end": v(19.17, -15.28) * mm});
            skLineSegment(sketch, "E763", {"start": v(19.17, -15.28) * mm, "end": v(19.22, -15.26) * mm});
            skLineSegment(sketch, "E764", {"start": v(19.22, -15.26) * mm, "end": v(20.21, -14.85) * mm});
            skLineSegment(sketch, "E765", {"start": v(20.21, -14.85) * mm, "end": v(20.26, -14.82) * mm});
            skLineSegment(sketch, "E766", {"start": v(20.26, -14.82) * mm, "end": v(21.2, -14.29) * mm});
            skLineSegment(sketch, "E767", {"start": v(21.2, -14.29) * mm, "end": v(21.26, -14.26) * mm});
            skLineSegment(sketch, "E768", {"start": v(21.26, -14.26) * mm, "end": v(22.2, -13.6) * mm});
            skLineSegment(sketch, "E769", {"start": v(22.2, -13.6) * mm, "end": v(22.22, -13.57) * mm});
            skLineSegment(sketch, "E770", {"start": v(22.22, -13.57) * mm, "end": v(23.03, -12.83) * mm});
            skLineSegment(sketch, "E771", {"start": v(23.03, -12.83) * mm, "end": v(23.08, -12.79) * mm});
            skLineSegment(sketch, "E772", {"start": v(23.08, -12.79) * mm, "end": v(23.79, -11.97) * mm});
            skLineSegment(sketch, "E773", {"start": v(23.79, -11.97) * mm, "end": v(23.83, -11.91) * mm});
            skLineSegment(sketch, "E774", {"start": v(23.83, -11.91) * mm, "end": v(24.43, -11.02) * mm});
            skLineSegment(sketch, "E775", {"start": v(24.43, -11.02) * mm, "end": v(24.47, -10.96) * mm});
            skLineSegment(sketch, "E776", {"start": v(24.47, -10.96) * mm, "end": v(24.97, -10) * mm});
            skLineSegment(sketch, "E777", {"start": v(24.97, -10) * mm, "end": v(25, -9.94) * mm});
            skLineSegment(sketch, "E778", {"start": v(25, -9.94) * mm, "end": v(25.4, -8.92) * mm});
            skLineSegment(sketch, "E779", {"start": v(25.4, -8.92) * mm, "end": v(25.42, -8.85) * mm});
            skLineSegment(sketch, "E780", {"start": v(25.42, -8.85) * mm, "end": v(25.7, -7.78) * mm});
            skLineSegment(sketch, "E781", {"start": v(25.7, -7.78) * mm, "end": v(25.73, -7.71) * mm});
            skLineSegment(sketch, "E782", {"start": v(25.73, -7.71) * mm, "end": v(25.9, -6.6) * mm});
            skLineSegment(sketch, "E783", {"start": v(25.9, -6.6) * mm, "end": v(25.92, -6.53) * mm});
            skLineSegment(sketch, "E784", {"start": v(25.92, -6.53) * mm, "end": v(26, -5.4) * mm});
            skLineSegment(sketch, "E785", {"start": v(26, -5.4) * mm, "end": v(26, -5.32) * mm});
            skLineSegment(sketch, "E786", {"start": v(26, -5.32) * mm, "end": v(25.97, -4.16) * mm});
            skLineSegment(sketch, "E787", {"start": v(25.97, -4.16) * mm, "end": v(25.96, -4.09) * mm});
            skLineSegment(sketch, "E788", {"start": v(25.96, -4.09) * mm, "end": v(25.82, -2.9) * mm});
            skLineSegment(sketch, "E789", {"start": v(25.82, -2.9) * mm, "end": v(25.81, -2.84) * mm});
            skLineSegment(sketch, "E790", {"start": v(-22.89, 51.69) * mm, "end": v(-23.87, 52.6) * mm});
            skLineSegment(sketch, "E791", {"start": v(-23.87, 52.6) * mm, "end": v(-23.9, 52.62) * mm});
            skLineSegment(sketch, "E792", {"start": v(-23.9, 52.62) * mm, "end": v(-23.86, 52.61) * mm});
            skLineSegment(sketch, "E793", {"start": v(-23.86, 52.61) * mm, "end": v(-23, 52.38) * mm});
            skLineSegment(sketch, "E794", {"start": v(-23, 52.38) * mm, "end": v(-22.96, 52.37) * mm});
            skLineSegment(sketch, "E795", {"start": v(-22.96, 52.37) * mm, "end": v(-22.21, 52.15) * mm});
            skLineSegment(sketch, "E796", {"start": v(-22.21, 52.15) * mm, "end": v(-22.15, 52.13) * mm});
            skLineSegment(sketch, "E797", {"start": v(-22.15, 52.13) * mm, "end": v(-21.5, 51.9) * mm});
            skLineSegment(sketch, "E798", {"start": v(-21.5, 51.9) * mm, "end": v(-21.46, 51.88) * mm});
            skLineSegment(sketch, "E799", {"start": v(-21.46, 51.88) * mm, "end": v(-20.9, 51.65) * mm});
            skLineSegment(sketch, "E800", {"start": v(-20.9, 51.65) * mm, "end": v(-20.86, 51.64) * mm});
            skLineSegment(sketch, "E801", {"start": v(-20.86, 51.64) * mm, "end": v(-19.93, 51.18) * mm});
            skLineSegment(sketch, "E802", {"start": v(-19.93, 51.18) * mm, "end": v(-19.89, 51.16) * mm});
            skLineSegment(sketch, "E803", {"start": v(-19.89, 51.16) * mm, "end": v(-19.06, 50.69) * mm});
            skLineSegment(sketch, "E804", {"start": v(-19.06, 50.69) * mm, "end": v(-19.05, 50.7) * mm});
            skLineSegment(sketch, "E805", {"start": v(-19.05, 50.7) * mm, "end": v(-18.92, 50.85) * mm});
            skLineSegment(sketch, "E806", {"start": v(-18.92, 50.85) * mm, "end": v(-18.82, 51) * mm});
            skLineSegment(sketch, "E807", {"start": v(-18.82, 51) * mm, "end": v(-18.81, 51) * mm});
            skLineSegment(sketch, "E808", {"start": v(-18.81, 51) * mm, "end": v(-18.8, 51) * mm});
            skLineSegment(sketch, "E809", {"start": v(-18.8, 51) * mm, "end": v(-18.74, 51.15) * mm});
            skLineSegment(sketch, "E810", {"start": v(-18.74, 51.15) * mm, "end": v(-18.74, 51.15) * mm});
            skLineSegment(sketch, "E811", {"start": v(-18.74, 51.15) * mm, "end": v(-18.72, 51.22) * mm});
            skLineSegment(sketch, "E812", {"start": v(-18.72, 51.22) * mm, "end": v(-18.72, 51.23) * mm});
            skLineSegment(sketch, "E813", {"start": v(-18.72, 51.23) * mm, "end": v(-18.7, 51.3) * mm});
            skLineSegment(sketch, "E814", {"start": v(-18.7, 51.3) * mm, "end": v(-18.7, 51.3) * mm});
            skLineSegment(sketch, "E815", {"start": v(-18.7, 51.3) * mm, "end": v(-18.7, 51.37) * mm});
            skLineSegment(sketch, "E816", {"start": v(-18.7, 51.37) * mm, "end": v(-18.7, 51.37) * mm});
            skLineSegment(sketch, "E817", {"start": v(-18.7, 51.37) * mm, "end": v(-18.69, 51.44) * mm});
            skLineSegment(sketch, "E818", {"start": v(-18.69, 51.44) * mm, "end": v(-18.69, 51.44) * mm});
            skLineSegment(sketch, "E819", {"start": v(-18.69, 51.44) * mm, "end": v(-18.7, 51.57) * mm});
            skLineSegment(sketch, "E820", {"start": v(-18.7, 51.57) * mm, "end": v(-18.7, 51.58) * mm});
            skLineSegment(sketch, "E821", {"start": v(-18.7, 51.58) * mm, "end": v(-18.73, 51.7) * mm});
            skLineSegment(sketch, "E822", {"start": v(-18.73, 51.7) * mm, "end": v(-18.79, 51.84) * mm});
            skLineSegment(sketch, "E823", {"start": v(-18.79, 51.84) * mm, "end": v(-18.8, 51.85) * mm});
            skLineSegment(sketch, "E824", {"start": v(-18.8, 51.85) * mm, "end": v(-18.93, 52.1) * mm});
            skLineSegment(sketch, "E825", {"start": v(-18.93, 52.1) * mm, "end": v(-18.94, 52.1) * mm});
            skLineSegment(sketch, "E826", {"start": v(-18.94, 52.1) * mm, "end": v(-19.12, 52.34) * mm});
            skLineSegment(sketch, "E827", {"start": v(-19.12, 52.34) * mm, "end": v(-19.13, 52.35) * mm});
            skLineSegment(sketch, "E828", {"start": v(-19.13, 52.35) * mm, "end": v(-19.49, 52.81) * mm});
            skLineSegment(sketch, "E829", {"start": v(-19.49, 52.81) * mm, "end": v(-19.5, 52.83) * mm});
            skLineSegment(sketch, "E830", {"start": v(-19.5, 52.83) * mm, "end": v(-19.48, 52.83) * mm});
            skLineSegment(sketch, "E831", {"start": v(-19.48, 52.83) * mm, "end": v(-19.46, 52.82) * mm});
            skLineSegment(sketch, "E832", {"start": v(-19.46, 52.82) * mm, "end": v(-18.8, 52.57) * mm});
            skLineSegment(sketch, "E833", {"start": v(-18.8, 52.57) * mm, "end": v(-18.2, 52.3) * mm});
            skLineSegment(sketch, "E834", {"start": v(-18.2, 52.3) * mm, "end": v(-18.16, 52.28) * mm});
            skLineSegment(sketch, "E835", {"start": v(-18.16, 52.28) * mm, "end": v(-18.11, 52.25) * mm});
            skLineSegment(sketch, "E836", {"start": v(-18.11, 52.25) * mm, "end": v(-17.1, 51.63) * mm});
            skLineSegment(sketch, "E837", {"start": v(-17.1, 51.63) * mm, "end": v(-17.05, 51.6) * mm});
            skLineSegment(sketch, "E838", {"start": v(-17.05, 51.6) * mm, "end": v(-16.18, 50.95) * mm});
            skLineSegment(sketch, "E839", {"start": v(-16.18, 50.95) * mm, "end": v(-16.15, 50.93) * mm});
            skLineSegment(sketch, "E840", {"start": v(-16.15, 50.93) * mm, "end": v(-15.37, 50.3) * mm});
            skLineSegment(sketch, "E841", {"start": v(-15.37, 50.3) * mm, "end": v(-15.33, 50.26) * mm});
            skLineSegment(sketch, "E842", {"start": v(-15.33, 50.26) * mm, "end": v(-15.32, 50.27) * mm});
            skLineSegment(sketch, "E843", {"start": v(-15.32, 50.27) * mm, "end": v(-15.02, 50.59) * mm});
            skLineSegment(sketch, "E844", {"start": v(-15.02, 50.59) * mm, "end": v(-15.01, 50.6) * mm});
            skLineSegment(sketch, "E845", {"start": v(-15.01, 50.6) * mm, "end": v(-14.9, 50.77) * mm});
            skLineSegment(sketch, "E846", {"start": v(-14.9, 50.77) * mm, "end": v(-14.89, 50.78) * mm});
            skLineSegment(sketch, "E847", {"start": v(-14.89, 50.78) * mm, "end": v(-14.84, 50.88) * mm});
            skLineSegment(sketch, "E848", {"start": v(-14.84, 50.88) * mm, "end": v(-14.84, 50.88) * mm});
            skLineSegment(sketch, "E849", {"start": v(-14.84, 50.88) * mm, "end": v(-14.8, 50.98) * mm});
            skLineSegment(sketch, "E850", {"start": v(-14.8, 50.98) * mm, "end": v(-14.78, 51.1) * mm});
            skLineSegment(sketch, "E851", {"start": v(-14.78, 51.1) * mm, "end": v(-14.78, 51.1) * mm});
            skLineSegment(sketch, "E852", {"start": v(-14.78, 51.1) * mm, "end": v(-14.77, 51.22) * mm});
            skLineSegment(sketch, "E853", {"start": v(-14.77, 51.22) * mm, "end": v(-14.77, 51.23) * mm});
            skLineSegment(sketch, "E854", {"start": v(-14.77, 51.23) * mm, "end": v(-14.78, 51.35) * mm});
            skLineSegment(sketch, "E855", {"start": v(-14.78, 51.35) * mm, "end": v(-14.78, 51.36) * mm});
            skLineSegment(sketch, "E856", {"start": v(-14.78, 51.36) * mm, "end": v(-14.8, 51.5) * mm});
            skLineSegment(sketch, "E857", {"start": v(-14.8, 51.5) * mm, "end": v(-14.84, 51.64) * mm});
            skLineSegment(sketch, "E858", {"start": v(-14.84, 51.64) * mm, "end": v(-14.85, 51.65) * mm});
            skLineSegment(sketch, "E859", {"start": v(-14.85, 51.65) * mm, "end": v(-14.9, 51.81) * mm});
            skLineSegment(sketch, "E860", {"start": v(-14.9, 51.81) * mm, "end": v(-14.91, 51.83) * mm});
            skLineSegment(sketch, "E861", {"start": v(-14.91, 51.83) * mm, "end": v(-15.1, 52.18) * mm});
            skLineSegment(sketch, "E862", {"start": v(-15.1, 52.18) * mm, "end": v(-15.1, 52.2) * mm});
            skLineSegment(sketch, "E863", {"start": v(-15.1, 52.2) * mm, "end": v(-15.05, 52.15) * mm});
            skLineSegment(sketch, "E864", {"start": v(-15.05, 52.15) * mm, "end": v(-14.07, 51.55) * mm});
            skLineSegment(sketch, "E865", {"start": v(-14.07, 51.55) * mm, "end": v(-14.02, 51.5) * mm});
            skLineSegment(sketch, "E866", {"start": v(-14.02, 51.5) * mm, "end": v(-13.21, 50.88) * mm});
            skLineSegment(sketch, "E867", {"start": v(-13.21, 50.88) * mm, "end": v(-13.17, 50.84) * mm});
            skLineSegment(sketch, "E868", {"start": v(-13.17, 50.84) * mm, "end": v(-12.48, 50.17) * mm});
            skLineSegment(sketch, "E869", {"start": v(-12.48, 50.17) * mm, "end": v(-12.46, 50.15) * mm});
            skLineSegment(sketch, "E870", {"start": v(-12.46, 50.15) * mm, "end": v(-11.81, 49.4) * mm});
            skLineSegment(sketch, "E871", {"start": v(-11.81, 49.4) * mm, "end": v(-11.8, 49.4) * mm});
            skLineSegment(sketch, "E872", {"start": v(-11.8, 49.4) * mm, "end": v(-11.8, 49.41) * mm});
            skLineSegment(sketch, "E873", {"start": v(-11.8, 49.41) * mm, "end": v(-11.66, 49.5) * mm});
            skLineSegment(sketch, "E874", {"start": v(-11.66, 49.5) * mm, "end": v(-11.55, 49.58) * mm});
            skLineSegment(sketch, "E875", {"start": v(-11.55, 49.58) * mm, "end": v(-11.54, 49.59) * mm});
            skLineSegment(sketch, "E876", {"start": v(-11.54, 49.59) * mm, "end": v(-11.54, 49.59) * mm});
            skLineSegment(sketch, "E877", {"start": v(-11.54, 49.59) * mm, "end": v(-11.45, 49.69) * mm});
            skLineSegment(sketch, "E878", {"start": v(-11.45, 49.69) * mm, "end": v(-11.45, 49.69) * mm});
            skLineSegment(sketch, "E879", {"start": v(-11.45, 49.69) * mm, "end": v(-11.44, 49.7) * mm});
            skLineSegment(sketch, "E880", {"start": v(-11.44, 49.7) * mm, "end": v(-11.38, 49.8) * mm});
            skLineSegment(sketch, "E881", {"start": v(-11.38, 49.8) * mm, "end": v(-11.37, 49.8) * mm});
            skLineSegment(sketch, "E882", {"start": v(-11.37, 49.8) * mm, "end": v(-11.32, 49.9) * mm});
            skLineSegment(sketch, "E883", {"start": v(-11.32, 49.9) * mm, "end": v(-11.32, 49.91) * mm});
            skLineSegment(sketch, "E884", {"start": v(-11.32, 49.91) * mm, "end": v(-11.32, 49.92) * mm});
            skLineSegment(sketch, "E885", {"start": v(-11.32, 49.92) * mm, "end": v(-11.29, 50.03) * mm});
            skLineSegment(sketch, "E886", {"start": v(-11.29, 50.03) * mm, "end": v(-11.29, 50.04) * mm});
            skLineSegment(sketch, "E887", {"start": v(-11.29, 50.04) * mm, "end": v(-11.27, 50.16) * mm});
            skLineSegment(sketch, "E888", {"start": v(-11.27, 50.16) * mm, "end": v(-11.27, 50.16) * mm});
            skLineSegment(sketch, "E889", {"start": v(-11.27, 50.16) * mm, "end": v(-11.26, 50.28) * mm});
            skLineSegment(sketch, "E890", {"start": v(-11.26, 50.28) * mm, "end": v(-11.26, 50.3) * mm});
            skLineSegment(sketch, "E891", {"start": v(-11.26, 50.3) * mm, "end": v(-11.26, 50.3) * mm});
            skLineSegment(sketch, "E892", {"start": v(-11.26, 50.3) * mm, "end": v(-11.27, 50.33) * mm});
            skLineSegment(sketch, "E893", {"start": v(-11.27, 50.33) * mm, "end": v(-11.37, 51.3) * mm});
            skLineSegment(sketch, "E894", {"start": v(-11.37, 51.3) * mm, "end": v(-11.37, 51.33) * mm});
            skLineSegment(sketch, "E895", {"start": v(-11.37, 51.33) * mm, "end": v(-11.33, 51.3) * mm});
            skLineSegment(sketch, "E896", {"start": v(-11.33, 51.3) * mm, "end": v(-10.34, 50.42) * mm});
            skLineSegment(sketch, "E897", {"start": v(-10.34, 50.42) * mm, "end": v(-10.3, 50.38) * mm});
            skLineSegment(sketch, "E898", {"start": v(-10.3, 50.38) * mm, "end": v(-9.47, 49.54) * mm});
            skLineSegment(sketch, "E899", {"start": v(-9.47, 49.54) * mm, "end": v(-9.41, 49.47) * mm});
            skLineSegment(sketch, "E900", {"start": v(-9.41, 49.47) * mm, "end": v(-7.92, 47.76) * mm});
            skLineSegment(sketch, "E901", {"start": v(-7.92, 47.76) * mm, "end": v(-7.86, 47.7) * mm});
            skLineSegment(sketch, "E902", {"start": v(-7.86, 47.7) * mm, "end": v(-7.86, 47.7) * mm});
            skLineSegment(sketch, "E903", {"start": v(-7.86, 47.7) * mm, "end": v(-7.85, 47.7) * mm});
            skLineSegment(sketch, "E904", {"start": v(-7.85, 47.7) * mm, "end": v(-7.84, 47.7) * mm});
            skLineSegment(sketch, "E905", {"start": v(-7.84, 47.7) * mm, "end": v(-7.82, 47.7) * mm});
            skLineSegment(sketch, "E906", {"start": v(-7.82, 47.7) * mm, "end": v(-7.8, 47.7) * mm});
            skLineSegment(sketch, "E907", {"start": v(-7.8, 47.7) * mm, "end": v(-7.78, 47.72) * mm});
            skLineSegment(sketch, "E908", {"start": v(-7.78, 47.72) * mm, "end": v(-7.78, 47.72) * mm});
            skLineSegment(sketch, "E909", {"start": v(-7.78, 47.72) * mm, "end": v(-7.76, 47.74) * mm});
            skLineSegment(sketch, "E910", {"start": v(-7.76, 47.74) * mm, "end": v(-7.74, 47.75) * mm});
            skLineSegment(sketch, "E911", {"start": v(-7.74, 47.75) * mm, "end": v(-7.73, 47.76) * mm});
            skLineSegment(sketch, "E912", {"start": v(-7.73, 47.76) * mm, "end": v(-7.7, 47.8) * mm});
            skLineSegment(sketch, "E913", {"start": v(-7.7, 47.8) * mm, "end": v(-7.7, 47.8) * mm});
            skLineSegment(sketch, "E914", {"start": v(-7.7, 47.8) * mm, "end": v(-7.61, 47.94) * mm});
            skLineSegment(sketch, "E915", {"start": v(-7.61, 47.94) * mm, "end": v(-7.6, 47.95) * mm});
            skLineSegment(sketch, "E916", {"start": v(-7.6, 47.95) * mm, "end": v(-7.53, 48.12) * mm});
            skLineSegment(sketch, "E917", {"start": v(-7.53, 48.12) * mm, "end": v(-7.52, 48.14) * mm});
            skLineSegment(sketch, "E918", {"start": v(-7.52, 48.14) * mm, "end": v(-7.37, 48.58) * mm});
            skLineSegment(sketch, "E919", {"start": v(-7.37, 48.58) * mm, "end": v(-7.37, 48.6) * mm});
            skLineSegment(sketch, "E920", {"start": v(-7.37, 48.6) * mm, "end": v(-7.36, 48.61) * mm});
            skLineSegment(sketch, "E921", {"start": v(-7.36, 48.61) * mm, "end": v(-7.2, 49.2) * mm});
            skLineSegment(sketch, "E922", {"start": v(-7.2, 49.2) * mm, "end": v(-7.17, 49.16) * mm});
            skLineSegment(sketch, "E923", {"start": v(-7.17, 49.16) * mm, "end": v(-6.53, 48.53) * mm});
            skLineSegment(sketch, "E924", {"start": v(-6.53, 48.53) * mm, "end": v(-6.5, 48.5) * mm});
            skLineSegment(sketch, "E925", {"start": v(-6.5, 48.5) * mm, "end": v(-5.85, 47.77) * mm});
            skLineSegment(sketch, "E926", {"start": v(-5.85, 47.77) * mm, "end": v(-5.82, 47.73) * mm});
            skLineSegment(sketch, "E927", {"start": v(-5.82, 47.73) * mm, "end": v(-5.18, 46.92) * mm});
            skLineSegment(sketch, "E928", {"start": v(-5.18, 46.92) * mm, "end": v(-5.15, 46.87) * mm});
            skLineSegment(sketch, "E929", {"start": v(-5.15, 46.87) * mm, "end": v(-4.54, 46) * mm});
            skLineSegment(sketch, "E930", {"start": v(-4.54, 46) * mm, "end": v(-4.5, 45.94) * mm});
            skLineSegment(sketch, "E931", {"start": v(-4.5, 45.94) * mm, "end": v(-3.95, 45) * mm});
            skLineSegment(sketch, "E932", {"start": v(-3.95, 45) * mm, "end": v(-3.92, 44.95) * mm});
            skLineSegment(sketch, "E933", {"start": v(-3.92, 44.95) * mm, "end": v(-3.42, 43.97) * mm});
            skLineSegment(sketch, "E934", {"start": v(-3.42, 43.97) * mm, "end": v(-3.4, 43.9) * mm});
            skLineSegment(sketch, "E935", {"start": v(-3.4, 43.9) * mm, "end": v(-2.98, 42.9) * mm});
            skLineSegment(sketch, "E936", {"start": v(-2.98, 42.9) * mm, "end": v(-2.96, 42.84) * mm});
            skLineSegment(sketch, "E937", {"start": v(-2.96, 42.84) * mm, "end": v(-2.65, 41.81) * mm});
            skLineSegment(sketch, "E938", {"start": v(-2.65, 41.81) * mm, "end": v(-2.64, 41.74) * mm});
            skLineSegment(sketch, "E939", {"start": v(-2.64, 41.74) * mm, "end": v(-2.45, 40.71) * mm});
            skLineSegment(sketch, "E940", {"start": v(-2.45, 40.71) * mm, "end": v(-2.44, 40.65) * mm});
            skLineSegment(sketch, "E941", {"start": v(-2.44, 40.65) * mm, "end": v(-2.4, 39.63) * mm});
            skLineSegment(sketch, "E942", {"start": v(-2.4, 39.63) * mm, "end": v(-2.4, 39.56) * mm});
            skLineSegment(sketch, "E943", {"start": v(-2.4, 39.56) * mm, "end": v(-2.5, 38.57) * mm});
            skLineSegment(sketch, "E944", {"start": v(-2.5, 38.57) * mm, "end": v(-2.5, 38.53) * mm});
            skLineSegment(sketch, "E945", {"start": v(-2.5, 38.53) * mm, "end": v(-2.63, 38.05) * mm});
            skLineSegment(sketch, "E946", {"start": v(-2.63, 38.05) * mm, "end": v(-2.64, 38.02) * mm});
            skLineSegment(sketch, "E947", {"start": v(-2.64, 38.02) * mm, "end": v(-2.8, 37.55) * mm});
            skLineSegment(sketch, "E948", {"start": v(-2.8, 37.55) * mm, "end": v(-2.82, 37.52) * mm});
            skLineSegment(sketch, "E949", {"start": v(-2.82, 37.52) * mm, "end": v(-3.03, 37.06) * mm});
            skLineSegment(sketch, "E950", {"start": v(-3.03, 37.06) * mm, "end": v(-3.05, 37.03) * mm});
            skLineSegment(sketch, "E951", {"start": v(-3.05, 37.03) * mm, "end": v(-3.32, 36.59) * mm});
            skLineSegment(sketch, "E952", {"start": v(-3.32, 36.59) * mm, "end": v(-3.34, 36.56) * mm});
            skLineSegment(sketch, "E953", {"start": v(-3.34, 36.56) * mm, "end": v(-3.66, 36.13) * mm});
            skLineSegment(sketch, "E954", {"start": v(-3.66, 36.13) * mm, "end": v(-3.68, 36.1) * mm});
            skLineSegment(sketch, "E955", {"start": v(-3.68, 36.1) * mm, "end": v(-4.06, 35.7) * mm});
            skLineSegment(sketch, "E956", {"start": v(-4.06, 35.7) * mm, "end": v(-4.09, 35.67) * mm});
            skLineSegment(sketch, "E957", {"start": v(-4.09, 35.67) * mm, "end": v(-4.52, 35.28) * mm});
            skLineSegment(sketch, "E958", {"start": v(-4.52, 35.28) * mm, "end": v(-4.56, 35.26) * mm});
            skLineSegment(sketch, "E959", {"start": v(-4.56, 35.26) * mm, "end": v(-5.05, 34.9) * mm});
            skLineSegment(sketch, "E960", {"start": v(-5.05, 34.9) * mm, "end": v(-5.1, 34.87) * mm});
            skLineSegment(sketch, "E961", {"start": v(-5.1, 34.87) * mm, "end": v(-5.65, 34.53) * mm});
            skLineSegment(sketch, "E962", {"start": v(-5.65, 34.53) * mm, "end": v(-5.67, 34.52) * mm});
            skLineSegment(sketch, "E963", {"start": v(-5.67, 34.52) * mm, "end": v(-6.32, 34.19) * mm});
            skLineSegment(sketch, "E964", {"start": v(-6.32, 34.19) * mm, "end": v(-6.43, 34.28) * mm});
            skLineSegment(sketch, "E965", {"start": v(-6.43, 34.28) * mm, "end": v(-8.66, 35.95) * mm});
            skLineSegment(sketch, "E966", {"start": v(-8.66, 35.95) * mm, "end": v(-8.78, 36.04) * mm});
            skLineSegment(sketch, "E967", {"start": v(-8.78, 36.04) * mm, "end": v(-11.1, 37.6) * mm});
            skLineSegment(sketch, "E968", {"start": v(-11.1, 37.6) * mm, "end": v(-11.22, 37.67) * mm});
            skLineSegment(sketch, "E969", {"start": v(-11.22, 37.67) * mm, "end": v(-13.63, 39.1) * mm});
            skLineSegment(sketch, "E970", {"start": v(-13.63, 39.1) * mm, "end": v(-13.75, 39.18) * mm});
            skLineSegment(sketch, "E971", {"start": v(-13.75, 39.18) * mm, "end": v(-16.25, 40.52) * mm});
            skLineSegment(sketch, "E972", {"start": v(-16.25, 40.52) * mm, "end": v(-16.43, 40.6) * mm});
            skLineSegment(sketch, "E973", {"start": v(-16.43, 40.6) * mm, "end": v(-19.01, 41.85) * mm});
            skLineSegment(sketch, "E974", {"start": v(-19.01, 41.85) * mm, "end": v(-19.2, 41.93) * mm});
            skLineSegment(sketch, "E975", {"start": v(-19.2, 41.93) * mm, "end": v(-21.87, 43.09) * mm});
            skLineSegment(sketch, "E976", {"start": v(-21.87, 43.09) * mm, "end": v(-22.06, 43.16) * mm});
            skLineSegment(sketch, "E977", {"start": v(-22.06, 43.16) * mm, "end": v(-24.82, 44.24) * mm});
            skLineSegment(sketch, "E978", {"start": v(-24.82, 44.24) * mm, "end": v(-24.93, 44.28) * mm});
            skLineSegment(sketch, "E979", {"start": v(-24.93, 44.28) * mm, "end": v(-27.85, 45.33) * mm});
            skLineSegment(sketch, "E980", {"start": v(-27.85, 45.33) * mm, "end": v(-27.8, 45.3) * mm});
            skLineSegment(sketch, "E981", {"start": v(-27.8, 45.3) * mm, "end": v(-27.7, 45.26) * mm});
            skLineSegment(sketch, "E982", {"start": v(-27.7, 45.26) * mm, "end": v(-25.93, 44.36) * mm});
            skLineSegment(sketch, "E983", {"start": v(-25.93, 44.36) * mm, "end": v(-24.25, 43.48) * mm});
            skLineSegment(sketch, "E984", {"start": v(-24.25, 43.48) * mm, "end": v(-24.12, 43.41) * mm});
            skLineSegment(sketch, "E985", {"start": v(-24.12, 43.41) * mm, "end": v(-22.52, 42.55) * mm});
            skLineSegment(sketch, "E986", {"start": v(-22.52, 42.55) * mm, "end": v(-22.4, 42.49) * mm});
            skLineSegment(sketch, "E987", {"start": v(-22.4, 42.49) * mm, "end": v(-20.89, 41.64) * mm});
            skLineSegment(sketch, "E988", {"start": v(-20.89, 41.64) * mm, "end": v(-20.77, 41.58) * mm});
            skLineSegment(sketch, "E989", {"start": v(-20.77, 41.58) * mm, "end": v(-19.35, 40.75) * mm});
            skLineSegment(sketch, "E990", {"start": v(-19.35, 40.75) * mm, "end": v(-18, 39.94) * mm});
            skLineSegment(sketch, "E991", {"start": v(-18, 39.94) * mm, "end": v(-17.9, 39.88) * mm});
            skLineSegment(sketch, "E992", {"start": v(-17.9, 39.88) * mm, "end": v(-16.64, 39.1) * mm});
            skLineSegment(sketch, "E993", {"start": v(-16.64, 39.1) * mm, "end": v(-16.54, 39.03) * mm});
            skLineSegment(sketch, "E994", {"start": v(-16.54, 39.03) * mm, "end": v(-15.36, 38.25) * mm});
            skLineSegment(sketch, "E995", {"start": v(-15.36, 38.25) * mm, "end": v(-15.27, 38.2) * mm});
            skLineSegment(sketch, "E996", {"start": v(-15.27, 38.2) * mm, "end": v(-14.17, 37.44) * mm});
            skLineSegment(sketch, "E997", {"start": v(-14.17, 37.44) * mm, "end": v(-14.08, 37.38) * mm});
            skLineSegment(sketch, "E998", {"start": v(-14.08, 37.38) * mm, "end": v(-13.05, 36.64) * mm});
            skLineSegment(sketch, "E999", {"start": v(-13.05, 36.64) * mm, "end": v(-12.1, 35.91) * mm});
            skLineSegment(sketch, "E1000", {"start": v(-12.1, 35.91) * mm, "end": v(-12.01, 35.85) * mm});
            skLineSegment(sketch, "E1001", {"start": v(-12.01, 35.85) * mm, "end": v(-11.13, 35.14) * mm});
            skLineSegment(sketch, "E1002", {"start": v(-11.13, 35.14) * mm, "end": v(-11.05, 35.07) * mm});
            skLineSegment(sketch, "E1003", {"start": v(-11.05, 35.07) * mm, "end": v(-10.24, 34.38) * mm});
            skLineSegment(sketch, "E1004", {"start": v(-10.24, 34.38) * mm, "end": v(-9.5, 33.7) * mm});
            skLineSegment(sketch, "E1005", {"start": v(-9.5, 33.7) * mm, "end": v(-9.42, 33.64) * mm});
            skLineSegment(sketch, "E1006", {"start": v(-9.42, 33.64) * mm, "end": v(-8.75, 32.97) * mm});
            skLineSegment(sketch, "E1007", {"start": v(-8.75, 32.97) * mm, "end": v(-8.7, 32.93) * mm});
            skLineSegment(sketch, "E1008", {"start": v(-8.7, 32.93) * mm, "end": v(-8.07, 32.26) * mm});
            skLineSegment(sketch, "E1009", {"start": v(-8.07, 32.26) * mm, "end": v(-8.09, 32.21) * mm});
            skLineSegment(sketch, "E1010", {"start": v(-8.09, 32.21) * mm, "end": v(-8.47, 31.1) * mm});
            skLineSegment(sketch, "E1011", {"start": v(-8.47, 31.1) * mm, "end": v(-8.5, 31.06) * mm});
            skLineSegment(sketch, "E1012", {"start": v(-8.5, 31.06) * mm, "end": v(-9.02, 30.09) * mm});
            skLineSegment(sketch, "E1013", {"start": v(-9.02, 30.09) * mm, "end": v(-9.04, 30.05) * mm});
            skLineSegment(sketch, "E1014", {"start": v(-9.04, 30.05) * mm, "end": v(-9.07, 30.01) * mm});
            skLineSegment(sketch, "E1015", {"start": v(-9.07, 30.01) * mm, "end": v(-9.71, 29.16) * mm});
            skLineSegment(sketch, "E1016", {"start": v(-9.71, 29.16) * mm, "end": v(-9.74, 29.12) * mm});
            skLineSegment(sketch, "E1017", {"start": v(-9.74, 29.12) * mm, "end": v(-10.49, 28.38) * mm});
            skLineSegment(sketch, "E1018", {"start": v(-10.49, 28.38) * mm, "end": v(-10.52, 28.35) * mm});
            skLineSegment(sketch, "E1019", {"start": v(-10.52, 28.35) * mm, "end": v(-10.55, 28.33) * mm});
            skLineSegment(sketch, "E1020", {"start": v(-10.55, 28.33) * mm, "end": v(-11.39, 27.7) * mm});
            skLineSegment(sketch, "E1021", {"start": v(-11.39, 27.7) * mm, "end": v(-11.42, 27.67) * mm});
            skLineSegment(sketch, "E1022", {"start": v(-11.42, 27.67) * mm, "end": v(-12.33, 27.13) * mm});
            skLineSegment(sketch, "E1023", {"start": v(-12.33, 27.13) * mm, "end": v(-12.4, 27.1) * mm});
            skLineSegment(sketch, "E1024", {"start": v(-12.4, 27.1) * mm, "end": v(-13.36, 26.65) * mm});
            skLineSegment(sketch, "E1025", {"start": v(-13.36, 26.65) * mm, "end": v(-13.44, 26.62) * mm});
            skLineSegment(sketch, "E1026", {"start": v(-13.44, 26.62) * mm, "end": v(-14.42, 26.26) * mm});
            skLineSegment(sketch, "E1027", {"start": v(-14.42, 26.26) * mm, "end": v(-15.43, 25.97) * mm});
            skLineSegment(sketch, "E1028", {"start": v(-15.43, 25.97) * mm, "end": v(-15.51, 25.95) * mm});
            skLineSegment(sketch, "E1029", {"start": v(-15.51, 25.95) * mm, "end": v(-16.51, 25.73) * mm});
            skLineSegment(sketch, "E1030", {"start": v(-16.51, 25.73) * mm, "end": v(-16.6, 25.72) * mm});
            skLineSegment(sketch, "E1031", {"start": v(-16.6, 25.72) * mm, "end": v(-17.58, 25.56) * mm});
            skLineSegment(sketch, "E1032", {"start": v(-17.58, 25.56) * mm, "end": v(-17.66, 25.55) * mm});
            skLineSegment(sketch, "E1033", {"start": v(-17.66, 25.55) * mm, "end": v(-18.61, 25.45) * mm});
            skLineSegment(sketch, "E1034", {"start": v(-18.61, 25.45) * mm, "end": v(-19.51, 25.39) * mm});
            skLineSegment(sketch, "E1035", {"start": v(-19.51, 25.39) * mm, "end": v(-19.59, 25.38) * mm});
            skLineSegment(sketch, "E1036", {"start": v(-19.59, 25.38) * mm, "end": v(-20.42, 25.36) * mm});
            skLineSegment(sketch, "E1037", {"start": v(-20.42, 25.36) * mm, "end": v(-20.48, 25.36) * mm});
            skLineSegment(sketch, "E1038", {"start": v(-20.48, 25.36) * mm, "end": v(-21.22, 25.37) * mm});
            skLineSegment(sketch, "E1039", {"start": v(-21.22, 25.37) * mm, "end": v(-21.26, 25.37) * mm});
            skLineSegment(sketch, "E1040", {"start": v(-21.26, 25.37) * mm, "end": v(-21.92, 25.4) * mm});
            skLineSegment(sketch, "E1041", {"start": v(-21.92, 25.4) * mm, "end": v(-21.9, 25.4) * mm});
            skLineSegment(sketch, "E1042", {"start": v(-21.9, 25.4) * mm, "end": v(-21.89, 25.42) * mm});
            skLineSegment(sketch, "E1043", {"start": v(-21.89, 25.42) * mm, "end": v(-21.46, 25.7) * mm});
            skLineSegment(sketch, "E1044", {"start": v(-21.46, 25.7) * mm, "end": v(-21.45, 25.7) * mm});
            skLineSegment(sketch, "E1045", {"start": v(-21.45, 25.7) * mm, "end": v(-21.1, 25.96) * mm});
            skLineSegment(sketch, "E1046", {"start": v(-21.1, 25.96) * mm, "end": v(-21.08, 25.97) * mm});
            skLineSegment(sketch, "E1047", {"start": v(-21.08, 25.97) * mm, "end": v(-20.94, 26.1) * mm});
            skLineSegment(sketch, "E1048", {"start": v(-20.94, 26.1) * mm, "end": v(-20.93, 26.11) * mm});
            skLineSegment(sketch, "E1049", {"start": v(-20.93, 26.11) * mm, "end": v(-20.8, 26.27) * mm});
            skLineSegment(sketch, "E1050", {"start": v(-20.8, 26.27) * mm, "end": v(-20.8, 26.28) * mm});
            skLineSegment(sketch, "E1051", {"start": v(-20.8, 26.28) * mm, "end": v(-20.8, 26.28) * mm});
            skLineSegment(sketch, "E1052", {"start": v(-20.8, 26.28) * mm, "end": v(-20.7, 26.46) * mm});
            skLineSegment(sketch, "E1053", {"start": v(-20.7, 26.46) * mm, "end": v(-20.69, 26.47) * mm});
            skLineSegment(sketch, "E1054", {"start": v(-20.69, 26.47) * mm, "end": v(-20.6, 26.68) * mm});
            skLineSegment(sketch, "E1055", {"start": v(-20.6, 26.68) * mm, "end": v(-20.6, 26.69) * mm});
            skLineSegment(sketch, "E1056", {"start": v(-20.6, 26.69) * mm, "end": v(-20.6, 26.7) * mm});
            skLineSegment(sketch, "E1057", {"start": v(-20.6, 26.7) * mm, "end": v(-20.78, 26.76) * mm});
            skLineSegment(sketch, "E1058", {"start": v(-20.78, 26.76) * mm, "end": v(-20.8, 26.76) * mm});
            skLineSegment(sketch, "E1059", {"start": v(-20.8, 26.76) * mm, "end": v(-21.01, 26.81) * mm});
            skLineSegment(sketch, "E1060", {"start": v(-21.01, 26.81) * mm, "end": v(-21.04, 26.82) * mm});
            skLineSegment(sketch, "E1061", {"start": v(-21.04, 26.82) * mm, "end": v(-21.58, 26.88) * mm});
            skLineSegment(sketch, "E1062", {"start": v(-21.58, 26.88) * mm, "end": v(-21.61, 26.89) * mm});
            skLineSegment(sketch, "E1063", {"start": v(-21.61, 26.89) * mm, "end": v(-22.26, 26.93) * mm});
            skLineSegment(sketch, "E1064", {"start": v(-22.26, 26.93) * mm, "end": v(-22.3, 26.93) * mm});
            skLineSegment(sketch, "E1065", {"start": v(-22.3, 26.93) * mm, "end": v(-23.02, 26.98) * mm});
            skLineSegment(sketch, "E1066", {"start": v(-23.02, 26.98) * mm, "end": v(-23.1, 26.99) * mm});
            skLineSegment(sketch, "E1067", {"start": v(-23.1, 26.99) * mm, "end": v(-23.88, 27.06) * mm});
            skLineSegment(sketch, "E1068", {"start": v(-23.88, 27.06) * mm, "end": v(-24.67, 27.2) * mm});
            skLineSegment(sketch, "E1069", {"start": v(-24.67, 27.2) * mm, "end": v(-24.72, 27.2) * mm});
            skLineSegment(sketch, "E1070", {"start": v(-24.72, 27.2) * mm, "end": v(-25.5, 27.41) * mm});
            skLineSegment(sketch, "E1071", {"start": v(-25.5, 27.41) * mm, "end": v(-25.54, 27.43) * mm});
            skLineSegment(sketch, "E1072", {"start": v(-25.54, 27.43) * mm, "end": v(-26.27, 27.74) * mm});
            skLineSegment(sketch, "E1073", {"start": v(-26.27, 27.74) * mm, "end": v(-26.3, 27.76) * mm});
            skLineSegment(sketch, "E1074", {"start": v(-26.3, 27.76) * mm, "end": v(-26.29, 27.76) * mm});
            skLineSegment(sketch, "E1075", {"start": v(-26.29, 27.76) * mm, "end": v(-25.77, 27.89) * mm});
            skLineSegment(sketch, "E1076", {"start": v(-25.77, 27.89) * mm, "end": v(-25.75, 27.9) * mm});
            skLineSegment(sketch, "E1077", {"start": v(-25.75, 27.9) * mm, "end": v(-25.56, 27.95) * mm});
            skLineSegment(sketch, "E1078", {"start": v(-25.56, 27.95) * mm, "end": v(-25.54, 27.96) * mm});
            skLineSegment(sketch, "E1079", {"start": v(-25.54, 27.96) * mm, "end": v(-25.38, 28.03) * mm});
            skLineSegment(sketch, "E1080", {"start": v(-25.38, 28.03) * mm, "end": v(-25.37, 28.03) * mm});
            skLineSegment(sketch, "E1081", {"start": v(-25.37, 28.03) * mm, "end": v(-25.22, 28.12) * mm});
            skLineSegment(sketch, "E1082", {"start": v(-25.22, 28.12) * mm, "end": v(-25.22, 28.12) * mm});
            skLineSegment(sketch, "E1083", {"start": v(-25.22, 28.12) * mm, "end": v(-25.08, 28.23) * mm});
            skLineSegment(sketch, "E1084", {"start": v(-25.08, 28.23) * mm, "end": v(-25.07, 28.25) * mm});
            skLineSegment(sketch, "E1085", {"start": v(-25.07, 28.25) * mm, "end": v(-24.93, 28.4) * mm});
            skLineSegment(sketch, "E1086", {"start": v(-24.93, 28.4) * mm, "end": v(-24.92, 28.4) * mm});
            skLineSegment(sketch, "E1087", {"start": v(-24.92, 28.4) * mm, "end": v(-24.77, 28.61) * mm});
            skLineSegment(sketch, "E1088", {"start": v(-24.77, 28.61) * mm, "end": v(-24.9, 28.65) * mm});
            skLineSegment(sketch, "E1089", {"start": v(-24.9, 28.65) * mm, "end": v(-27.5, 29.51) * mm});
            skLineSegment(sketch, "E1090", {"start": v(-27.5, 29.51) * mm, "end": v(-27.6, 29.55) * mm});
            skLineSegment(sketch, "E1091", {"start": v(-27.6, 29.55) * mm, "end": v(-28.22, 29.78) * mm});
            skLineSegment(sketch, "E1092", {"start": v(-28.22, 29.78) * mm, "end": v(-28.8, 30.05) * mm});
            skLineSegment(sketch, "E1093", {"start": v(-28.8, 30.05) * mm, "end": v(-28.85, 30.08) * mm});
            skLineSegment(sketch, "E1094", {"start": v(-28.85, 30.08) * mm, "end": v(-29.36, 30.38) * mm});
            skLineSegment(sketch, "E1095", {"start": v(-29.36, 30.38) * mm, "end": v(-29.38, 30.4) * mm});
            skLineSegment(sketch, "E1096", {"start": v(-29.38, 30.4) * mm, "end": v(-29.81, 30.75) * mm});
            skLineSegment(sketch, "E1097", {"start": v(-29.81, 30.75) * mm, "end": v(-29.82, 30.76) * mm});
            skLineSegment(sketch, "E1098", {"start": v(-29.82, 30.76) * mm, "end": v(-29.77, 30.76) * mm});
            skLineSegment(sketch, "E1099", {"start": v(-29.77, 30.76) * mm, "end": v(-28.81, 30.73) * mm});
            skLineSegment(sketch, "E1100", {"start": v(-28.81, 30.73) * mm, "end": v(-28.8, 30.73) * mm});
            skLineSegment(sketch, "E1101", {"start": v(-28.8, 30.73) * mm, "end": v(-28.54, 30.77) * mm});
            skLineSegment(sketch, "E1102", {"start": v(-28.54, 30.77) * mm, "end": v(-28.53, 30.77) * mm});
            skLineSegment(sketch, "E1103", {"start": v(-28.53, 30.77) * mm, "end": v(-28.26, 30.85) * mm});
            skLineSegment(sketch, "E1104", {"start": v(-28.26, 30.85) * mm, "end": v(-28.24, 30.85) * mm});
            skLineSegment(sketch, "E1105", {"start": v(-28.24, 30.85) * mm, "end": v(-27.96, 30.98) * mm});
            skLineSegment(sketch, "E1106", {"start": v(-27.96, 30.98) * mm, "end": v(-27.94, 30.99) * mm});
            skLineSegment(sketch, "E1107", {"start": v(-27.94, 30.99) * mm, "end": v(-27.64, 31.18) * mm});
            skLineSegment(sketch, "E1108", {"start": v(-27.64, 31.18) * mm, "end": v(-27.63, 31.2) * mm});
            skLineSegment(sketch, "E1109", {"start": v(-27.63, 31.2) * mm, "end": v(-27.69, 31.22) * mm});
            skLineSegment(sketch, "E1110", {"start": v(-27.69, 31.22) * mm, "end": v(-28.83, 31.83) * mm});
            skLineSegment(sketch, "E1111", {"start": v(-28.83, 31.83) * mm, "end": v(-28.9, 31.86) * mm});
            skLineSegment(sketch, "E1112", {"start": v(-28.9, 31.86) * mm, "end": v(-30.1, 32.51) * mm});
            skLineSegment(sketch, "E1113", {"start": v(-30.1, 32.51) * mm, "end": v(-30.18, 32.56) * mm});
            skLineSegment(sketch, "E1114", {"start": v(-30.18, 32.56) * mm, "end": v(-31.34, 33.28) * mm});
            skLineSegment(sketch, "E1115", {"start": v(-31.34, 33.28) * mm, "end": v(-31.4, 33.32) * mm});
            skLineSegment(sketch, "E1116", {"start": v(-31.4, 33.32) * mm, "end": v(-31.94, 33.72) * mm});
            skLineSegment(sketch, "E1117", {"start": v(-31.94, 33.72) * mm, "end": v(-31.95, 33.74) * mm});
            skLineSegment(sketch, "E1118", {"start": v(-31.95, 33.74) * mm, "end": v(-32.46, 34.19) * mm});
            skLineSegment(sketch, "E1119", {"start": v(-32.46, 34.19) * mm, "end": v(-32.42, 34.2) * mm});
            skLineSegment(sketch, "E1120", {"start": v(-32.42, 34.2) * mm, "end": v(-31.15, 34.4) * mm});
            skLineSegment(sketch, "E1121", {"start": v(-31.15, 34.4) * mm, "end": v(-31.12, 34.4) * mm});
            skLineSegment(sketch, "E1122", {"start": v(-31.12, 34.4) * mm, "end": v(-31.1, 34.4) * mm});
            skLineSegment(sketch, "E1123", {"start": v(-31.1, 34.4) * mm, "end": v(-30.59, 34.49) * mm});
            skLineSegment(sketch, "E1124", {"start": v(-30.59, 34.49) * mm, "end": v(-30.57, 34.5) * mm});
            skLineSegment(sketch, "E1125", {"start": v(-30.57, 34.5) * mm, "end": v(-30.4, 34.54) * mm});
            skLineSegment(sketch, "E1126", {"start": v(-30.4, 34.54) * mm, "end": v(-30.39, 34.55) * mm});
            skLineSegment(sketch, "E1127", {"start": v(-30.39, 34.55) * mm, "end": v(-30.32, 34.58) * mm});
            skLineSegment(sketch, "E1128", {"start": v(-30.32, 34.58) * mm, "end": v(-30.3, 34.6) * mm});
            skLineSegment(sketch, "E1129", {"start": v(-30.3, 34.6) * mm, "end": v(-30.29, 34.6) * mm});
            skLineSegment(sketch, "E1130", {"start": v(-30.29, 34.6) * mm, "end": v(-30.27, 34.62) * mm});
            skLineSegment(sketch, "E1131", {"start": v(-30.27, 34.62) * mm, "end": v(-30.3, 34.64) * mm});
            skLineSegment(sketch, "E1132", {"start": v(-30.3, 34.64) * mm, "end": v(-30.34, 34.67) * mm});
            skLineSegment(sketch, "E1133", {"start": v(-30.34, 34.67) * mm, "end": v(-31.38, 35.42) * mm});
            skLineSegment(sketch, "E1134", {"start": v(-31.38, 35.42) * mm, "end": v(-32.35, 36.18) * mm});
            skLineSegment(sketch, "E1135", {"start": v(-32.35, 36.18) * mm, "end": v(-32.42, 36.23) * mm});
            skLineSegment(sketch, "E1136", {"start": v(-32.42, 36.23) * mm, "end": v(-33.3, 36.99) * mm});
            skLineSegment(sketch, "E1137", {"start": v(-33.3, 36.99) * mm, "end": v(-33.36, 37.03) * mm});
            skLineSegment(sketch, "E1138", {"start": v(-33.36, 37.03) * mm, "end": v(-34.17, 37.79) * mm});
            skLineSegment(sketch, "E1139", {"start": v(-34.17, 37.79) * mm, "end": v(-34.22, 37.83) * mm});
            skLineSegment(sketch, "E1140", {"start": v(-34.22, 37.83) * mm, "end": v(-34.2, 37.83) * mm});
            skLineSegment(sketch, "E1141", {"start": v(-34.2, 37.83) * mm, "end": v(-34.18, 37.83) * mm});
            skLineSegment(sketch, "E1142", {"start": v(-34.18, 37.83) * mm, "end": v(-33.48, 37.74) * mm});
            skLineSegment(sketch, "E1143", {"start": v(-33.48, 37.74) * mm, "end": v(-33.19, 37.75) * mm});
            skLineSegment(sketch, "E1144", {"start": v(-33.19, 37.75) * mm, "end": v(-33.17, 37.75) * mm});
            skLineSegment(sketch, "E1145", {"start": v(-33.17, 37.75) * mm, "end": v(-32.92, 37.77) * mm});
            skLineSegment(sketch, "E1146", {"start": v(-32.92, 37.77) * mm, "end": v(-32.9, 37.78) * mm});
            skLineSegment(sketch, "E1147", {"start": v(-32.9, 37.78) * mm, "end": v(-32.69, 37.82) * mm});
            skLineSegment(sketch, "E1148", {"start": v(-32.69, 37.82) * mm, "end": v(-32.68, 37.83) * mm});
            skLineSegment(sketch, "E1149", {"start": v(-32.68, 37.83) * mm, "end": v(-32.5, 37.89) * mm});
            skLineSegment(sketch, "E1150", {"start": v(-32.5, 37.89) * mm, "end": v(-32.49, 37.9) * mm});
            skLineSegment(sketch, "E1151", {"start": v(-32.49, 37.9) * mm, "end": v(-32.35, 37.96) * mm});
            skLineSegment(sketch, "E1152", {"start": v(-32.35, 37.96) * mm, "end": v(-32.34, 37.96) * mm});
            skLineSegment(sketch, "E1153", {"start": v(-32.34, 37.96) * mm, "end": v(-32.3, 38) * mm});
            skLineSegment(sketch, "E1154", {"start": v(-32.3, 38) * mm, "end": v(-32.29, 38) * mm});
            skLineSegment(sketch, "E1155", {"start": v(-32.29, 38) * mm, "end": v(-32.25, 38.04) * mm});
            skLineSegment(sketch, "E1156", {"start": v(-32.25, 38.04) * mm, "end": v(-32.24, 38.04) * mm});
            skLineSegment(sketch, "E1157", {"start": v(-32.24, 38.04) * mm, "end": v(-32.28, 38.08) * mm});
            skLineSegment(sketch, "E1158", {"start": v(-32.28, 38.08) * mm, "end": v(-33.11, 38.93) * mm});
            skLineSegment(sketch, "E1159", {"start": v(-33.11, 38.93) * mm, "end": v(-33.15, 38.97) * mm});
            skLineSegment(sketch, "E1160", {"start": v(-33.15, 38.97) * mm, "end": v(-34.03, 39.76) * mm});
            skLineSegment(sketch, "E1161", {"start": v(-34.03, 39.76) * mm, "end": v(-34.09, 39.82) * mm});
            skLineSegment(sketch, "E1162", {"start": v(-34.09, 39.82) * mm, "end": v(-34.88, 40.65) * mm});
            skLineSegment(sketch, "E1163", {"start": v(-34.88, 40.65) * mm, "end": v(-34.91, 40.7) * mm});
            skLineSegment(sketch, "E1164", {"start": v(-34.91, 40.7) * mm, "end": v(-35.25, 41.15) * mm});
            skLineSegment(sketch, "E1165", {"start": v(-35.25, 41.15) * mm, "end": v(-35.26, 41.17) * mm});
            skLineSegment(sketch, "E1166", {"start": v(-35.26, 41.17) * mm, "end": v(-35.54, 41.69) * mm});
            skLineSegment(sketch, "E1167", {"start": v(-35.54, 41.69) * mm, "end": v(-35.53, 41.68) * mm});
            skLineSegment(sketch, "E1168", {"start": v(-35.53, 41.68) * mm, "end": v(-35.52, 41.68) * mm});
            skLineSegment(sketch, "E1169", {"start": v(-35.52, 41.68) * mm, "end": v(-35.2, 41.55) * mm});
            skLineSegment(sketch, "E1170", {"start": v(-35.2, 41.55) * mm, "end": v(-34.9, 41.45) * mm});
            skLineSegment(sketch, "E1171", {"start": v(-34.9, 41.45) * mm, "end": v(-34.88, 41.45) * mm});
            skLineSegment(sketch, "E1172", {"start": v(-34.88, 41.45) * mm, "end": v(-34.57, 41.39) * mm});
            skLineSegment(sketch, "E1173", {"start": v(-34.57, 41.39) * mm, "end": v(-34.56, 41.39) * mm});
            skLineSegment(sketch, "E1174", {"start": v(-34.56, 41.39) * mm, "end": v(-34.26, 41.37) * mm});
            skLineSegment(sketch, "E1175", {"start": v(-34.26, 41.37) * mm, "end": v(-34.24, 41.37) * mm});
            skLineSegment(sketch, "E1176", {"start": v(-34.24, 41.37) * mm, "end": v(-33.95, 41.39) * mm});
            skLineSegment(sketch, "E1177", {"start": v(-33.95, 41.39) * mm, "end": v(-33.94, 41.39) * mm});
            skLineSegment(sketch, "E1178", {"start": v(-33.94, 41.39) * mm, "end": v(-33.66, 41.44) * mm});
            skLineSegment(sketch, "E1179", {"start": v(-33.66, 41.44) * mm, "end": v(-33.65, 41.45) * mm});
            skLineSegment(sketch, "E1180", {"start": v(-33.65, 41.45) * mm, "end": v(-33.4, 41.54) * mm});
            skLineSegment(sketch, "E1181", {"start": v(-33.4, 41.54) * mm, "end": v(-33.38, 41.55) * mm});
            skLineSegment(sketch, "E1182", {"start": v(-33.38, 41.55) * mm, "end": v(-33.14, 41.68) * mm});
            skLineSegment(sketch, "E1183", {"start": v(-33.14, 41.68) * mm, "end": v(-33.12, 41.69) * mm});
            skLineSegment(sketch, "E1184", {"start": v(-33.12, 41.69) * mm, "end": v(-33.13, 41.7) * mm});
            skLineSegment(sketch, "E1185", {"start": v(-33.13, 41.7) * mm, "end": v(-33.22, 41.85) * mm});
            skLineSegment(sketch, "E1186", {"start": v(-33.22, 41.85) * mm, "end": v(-33.34, 41.99) * mm});
            skLineSegment(sketch, "E1187", {"start": v(-33.34, 41.99) * mm, "end": v(-33.35, 42) * mm});
            skLineSegment(sketch, "E1188", {"start": v(-33.35, 42) * mm, "end": v(-33.65, 42.27) * mm});
            skLineSegment(sketch, "E1189", {"start": v(-33.65, 42.27) * mm, "end": v(-33.67, 42.29) * mm});
            skLineSegment(sketch, "E1190", {"start": v(-33.67, 42.29) * mm, "end": v(-34.04, 42.57) * mm});
            skLineSegment(sketch, "E1191", {"start": v(-34.04, 42.57) * mm, "end": v(-34.07, 42.6) * mm});
            skLineSegment(sketch, "E1192", {"start": v(-34.07, 42.6) * mm, "end": v(-34.49, 42.92) * mm});
            skLineSegment(sketch, "E1193", {"start": v(-34.49, 42.92) * mm, "end": v(-34.92, 43.29) * mm});
            skLineSegment(sketch, "E1194", {"start": v(-34.92, 43.29) * mm, "end": v(-34.96, 43.33) * mm});
            skLineSegment(sketch, "E1195", {"start": v(-34.96, 43.33) * mm, "end": v(-35.39, 43.78) * mm});
            skLineSegment(sketch, "E1196", {"start": v(-35.39, 43.78) * mm, "end": v(-35.42, 43.81) * mm});
            skLineSegment(sketch, "E1197", {"start": v(-35.42, 43.81) * mm, "end": v(-35.82, 44.37) * mm});
            skLineSegment(sketch, "E1198", {"start": v(-35.82, 44.37) * mm, "end": v(-35.83, 44.4) * mm});
            skLineSegment(sketch, "E1199", {"start": v(-35.83, 44.4) * mm, "end": v(-36.18, 45.08) * mm});
            skLineSegment(sketch, "E1200", {"start": v(-36.18, 45.08) * mm, "end": v(-36.2, 45.12) * mm});
            skLineSegment(sketch, "E1201", {"start": v(-36.2, 45.12) * mm, "end": v(-36.15, 45.12) * mm});
            skLineSegment(sketch, "E1202", {"start": v(-36.15, 45.12) * mm, "end": v(-34.88, 45.04) * mm});
            skLineSegment(sketch, "E1203", {"start": v(-34.88, 45.04) * mm, "end": v(-34.85, 45.04) * mm});
            skLineSegment(sketch, "E1204", {"start": v(-34.85, 45.04) * mm, "end": v(-34.83, 45.04) * mm});
            skLineSegment(sketch, "E1205", {"start": v(-34.83, 45.04) * mm, "end": v(-34.32, 45.03) * mm});
            skLineSegment(sketch, "E1206", {"start": v(-34.32, 45.03) * mm, "end": v(-34.3, 45.03) * mm});
            skLineSegment(sketch, "E1207", {"start": v(-34.3, 45.03) * mm, "end": v(-34.2, 45.04) * mm});
            skLineSegment(sketch, "E1208", {"start": v(-34.2, 45.04) * mm, "end": v(-34.2, 45.04) * mm});
            skLineSegment(sketch, "E1209", {"start": v(-34.2, 45.04) * mm, "end": v(-34.12, 45.06) * mm});
            skLineSegment(sketch, "E1210", {"start": v(-34.12, 45.06) * mm, "end": v(-34.12, 45.06) * mm});
            skLineSegment(sketch, "E1211", {"start": v(-34.12, 45.06) * mm, "end": v(-34.08, 45.07) * mm});
            skLineSegment(sketch, "E1212", {"start": v(-34.08, 45.07) * mm, "end": v(-34.05, 45.08) * mm});
            skLineSegment(sketch, "E1213", {"start": v(-34.05, 45.08) * mm, "end": v(-34.02, 45.1) * mm});
            skLineSegment(sketch, "E1214", {"start": v(-34.02, 45.1) * mm, "end": v(-34.02, 45.1) * mm});
            skLineSegment(sketch, "E1215", {"start": v(-34.02, 45.1) * mm, "end": v(-34, 45.12) * mm});
            skLineSegment(sketch, "E1216", {"start": v(-34, 45.12) * mm, "end": v(-34, 45.14) * mm});
            skLineSegment(sketch, "E1217", {"start": v(-34, 45.14) * mm, "end": v(-34, 45.16) * mm});
            skLineSegment(sketch, "E1218", {"start": v(-34, 45.16) * mm, "end": v(-34.18, 45.74) * mm});
            skLineSegment(sketch, "E1219", {"start": v(-34.18, 45.74) * mm, "end": v(-34.39, 46.26) * mm});
            skLineSegment(sketch, "E1220", {"start": v(-34.39, 46.26) * mm, "end": v(-34.4, 46.3) * mm});
            skLineSegment(sketch, "E1221", {"start": v(-34.4, 46.3) * mm, "end": v(-34.88, 47.24) * mm});
            skLineSegment(sketch, "E1222", {"start": v(-34.88, 47.24) * mm, "end": v(-34.9, 47.28) * mm});
            skLineSegment(sketch, "E1223", {"start": v(-34.9, 47.28) * mm, "end": v(-34.93, 47.32) * mm});
            skLineSegment(sketch, "E1224", {"start": v(-34.93, 47.32) * mm, "end": v(-35.44, 48.15) * mm});
            skLineSegment(sketch, "E1225", {"start": v(-35.44, 48.15) * mm, "end": v(-35.46, 48.17) * mm});
            skLineSegment(sketch, "E1226", {"start": v(-35.46, 48.17) * mm, "end": v(-35.95, 48.94) * mm});
            skLineSegment(sketch, "E1227", {"start": v(-35.95, 48.94) * mm, "end": v(-35.98, 48.98) * mm});
            skLineSegment(sketch, "E1228", {"start": v(-35.98, 48.98) * mm, "end": v(-35.92, 48.98) * mm});
            skLineSegment(sketch, "E1229", {"start": v(-35.92, 48.98) * mm, "end": v(-35.18, 48.98) * mm});
            skLineSegment(sketch, "E1230", {"start": v(-35.18, 48.98) * mm, "end": v(-34.38, 48.98) * mm});
            skLineSegment(sketch, "E1231", {"start": v(-34.38, 48.98) * mm, "end": v(-34.32, 48.98) * mm});
            skLineSegment(sketch, "E1232", {"start": v(-34.32, 48.98) * mm, "end": v(-32.75, 49) * mm});
            skLineSegment(sketch, "E1233", {"start": v(-32.75, 49) * mm, "end": v(-32.68, 49) * mm});
            skLineSegment(sketch, "E1234", {"start": v(-32.68, 49) * mm, "end": v(-32, 49.03) * mm});
            skLineSegment(sketch, "E1235", {"start": v(-32, 49.03) * mm, "end": v(-31.93, 49.03) * mm});
            skLineSegment(sketch, "E1236", {"start": v(-31.93, 49.03) * mm, "end": v(-31.36, 49.07) * mm});
            skLineSegment(sketch, "E1237", {"start": v(-31.36, 49.07) * mm, "end": v(-31.34, 49.07) * mm});
            skLineSegment(sketch, "E1238", {"start": v(-31.34, 49.07) * mm, "end": v(-31.32, 49.07) * mm});
            skLineSegment(sketch, "E1239", {"start": v(-31.32, 49.07) * mm, "end": v(-30.92, 49.12) * mm});
            skLineSegment(sketch, "E1240", {"start": v(-30.92, 49.12) * mm, "end": v(-30.9, 49.12) * mm});
            skLineSegment(sketch, "E1241", {"start": v(-30.9, 49.12) * mm, "end": v(-30.78, 49.15) * mm});
            skLineSegment(sketch, "E1242", {"start": v(-30.78, 49.15) * mm, "end": v(-30.74, 49.17) * mm});
            skLineSegment(sketch, "E1243", {"start": v(-30.74, 49.17) * mm, "end": v(-30.72, 49.18) * mm});
            skLineSegment(sketch, "E1244", {"start": v(-30.72, 49.18) * mm, "end": v(-30.7, 49.19) * mm});
            skLineSegment(sketch, "E1245", {"start": v(-30.7, 49.19) * mm, "end": v(-30.7, 49.2) * mm});
            skLineSegment(sketch, "E1246", {"start": v(-30.7, 49.2) * mm, "end": v(-30.74, 49.23) * mm});
            skLineSegment(sketch, "E1247", {"start": v(-30.74, 49.23) * mm, "end": v(-32.02, 50.48) * mm});
            skLineSegment(sketch, "E1248", {"start": v(-32.02, 50.48) * mm, "end": v(-31.98, 50.48) * mm});
            skLineSegment(sketch, "E1249", {"start": v(-31.98, 50.48) * mm, "end": v(-31.28, 50.59) * mm});
            skLineSegment(sketch, "E1250", {"start": v(-31.28, 50.59) * mm, "end": v(-31.24, 50.6) * mm});
            skLineSegment(sketch, "E1251", {"start": v(-31.24, 50.6) * mm, "end": v(-30.55, 50.62) * mm});
            skLineSegment(sketch, "E1252", {"start": v(-30.55, 50.62) * mm, "end": v(-29.87, 50.58) * mm});
            skLineSegment(sketch, "E1253", {"start": v(-29.87, 50.58) * mm, "end": v(-29.8, 50.57) * mm});
            skLineSegment(sketch, "E1254", {"start": v(-29.8, 50.57) * mm, "end": v(-29.13, 50.48) * mm});
            skLineSegment(sketch, "E1255", {"start": v(-29.13, 50.48) * mm, "end": v(-29.06, 50.47) * mm});
            skLineSegment(sketch, "E1256", {"start": v(-29.06, 50.47) * mm, "end": v(-27.79, 50.18) * mm});
            skLineSegment(sketch, "E1257", {"start": v(-27.79, 50.18) * mm, "end": v(-27.75, 50.17) * mm});
            skLineSegment(sketch, "E1258", {"start": v(-27.75, 50.17) * mm, "end": v(-26.6, 49.85) * mm});
            skLineSegment(sketch, "E1259", {"start": v(-26.6, 49.85) * mm, "end": v(-26.53, 49.83) * mm});
            skLineSegment(sketch, "E1260", {"start": v(-26.53, 49.83) * mm, "end": v(-26.53, 49.84) * mm});
            skLineSegment(sketch, "E1261", {"start": v(-26.53, 49.84) * mm, "end": v(-26.43, 49.95) * mm});
            skLineSegment(sketch, "E1262", {"start": v(-26.43, 49.95) * mm, "end": v(-26.42, 49.96) * mm});
            skLineSegment(sketch, "E1263", {"start": v(-26.42, 49.96) * mm, "end": v(-26.35, 50.07) * mm});
            skLineSegment(sketch, "E1264", {"start": v(-26.35, 50.07) * mm, "end": v(-26.34, 50.08) * mm});
            skLineSegment(sketch, "E1265", {"start": v(-26.34, 50.08) * mm, "end": v(-26.32, 50.13) * mm});
            skLineSegment(sketch, "E1266", {"start": v(-26.32, 50.13) * mm, "end": v(-26.32, 50.14) * mm});
            skLineSegment(sketch, "E1267", {"start": v(-26.32, 50.14) * mm, "end": v(-26.3, 50.2) * mm});
            skLineSegment(sketch, "E1268", {"start": v(-26.3, 50.2) * mm, "end": v(-26.28, 50.25) * mm});
            skLineSegment(sketch, "E1269", {"start": v(-26.28, 50.25) * mm, "end": v(-26.28, 50.26) * mm});
            skLineSegment(sketch, "E1270", {"start": v(-26.28, 50.26) * mm, "end": v(-26.27, 50.31) * mm});
            skLineSegment(sketch, "E1271", {"start": v(-26.27, 50.31) * mm, "end": v(-26.27, 50.32) * mm});
            skLineSegment(sketch, "E1272", {"start": v(-26.27, 50.32) * mm, "end": v(-26.27, 50.38) * mm});
            skLineSegment(sketch, "E1273", {"start": v(-26.27, 50.38) * mm, "end": v(-26.27, 50.43) * mm});
            skLineSegment(sketch, "E1274", {"start": v(-26.27, 50.43) * mm, "end": v(-26.27, 50.44) * mm});
            skLineSegment(sketch, "E1275", {"start": v(-26.27, 50.44) * mm, "end": v(-26.28, 50.5) * mm});
            skLineSegment(sketch, "E1276", {"start": v(-26.28, 50.5) * mm, "end": v(-26.28, 50.5) * mm});
            skLineSegment(sketch, "E1277", {"start": v(-26.28, 50.5) * mm, "end": v(-26.29, 50.55) * mm});
            skLineSegment(sketch, "E1278", {"start": v(-26.29, 50.55) * mm, "end": v(-26.3, 50.56) * mm});
            skLineSegment(sketch, "E1279", {"start": v(-26.3, 50.56) * mm, "end": v(-26.33, 50.67) * mm});
            skLineSegment(sketch, "E1280", {"start": v(-26.33, 50.67) * mm, "end": v(-26.33, 50.68) * mm});
            skLineSegment(sketch, "E1281", {"start": v(-26.33, 50.68) * mm, "end": v(-26.4, 50.8) * mm});
            skLineSegment(sketch, "E1282", {"start": v(-26.4, 50.8) * mm, "end": v(-26.4, 50.8) * mm});
            skLineSegment(sketch, "E1283", {"start": v(-26.4, 50.8) * mm, "end": v(-26.47, 50.91) * mm});
            skLineSegment(sketch, "E1284", {"start": v(-26.47, 50.91) * mm, "end": v(-26.48, 50.92) * mm});
            skLineSegment(sketch, "E1285", {"start": v(-26.48, 50.92) * mm, "end": v(-26.57, 51.04) * mm});
            skLineSegment(sketch, "E1286", {"start": v(-26.57, 51.04) * mm, "end": v(-26.58, 51.04) * mm});
            skLineSegment(sketch, "E1287", {"start": v(-26.58, 51.04) * mm, "end": v(-26.8, 51.27) * mm});
            skLineSegment(sketch, "E1288", {"start": v(-26.8, 51.27) * mm, "end": v(-26.8, 51.28) * mm});
            skLineSegment(sketch, "E1289", {"start": v(-26.8, 51.28) * mm, "end": v(-26.82, 51.29) * mm});
            skLineSegment(sketch, "E1290", {"start": v(-26.82, 51.29) * mm, "end": v(-27.38, 51.74) * mm});
            skLineSegment(sketch, "E1291", {"start": v(-27.38, 51.74) * mm, "end": v(-27.4, 51.76) * mm});
            skLineSegment(sketch, "E1292", {"start": v(-27.4, 51.76) * mm, "end": v(-27.35, 51.75) * mm});
            skLineSegment(sketch, "E1293", {"start": v(-27.35, 51.75) * mm, "end": v(-26.15, 51.57) * mm});
            skLineSegment(sketch, "E1294", {"start": v(-26.15, 51.57) * mm, "end": v(-26.1, 51.56) * mm});
            skLineSegment(sketch, "E1295", {"start": v(-26.1, 51.56) * mm, "end": v(-24.97, 51.31) * mm});
            skLineSegment(sketch, "E1296", {"start": v(-24.97, 51.31) * mm, "end": v(-24.89, 51.3) * mm});
            skLineSegment(sketch, "E1297", {"start": v(-24.89, 51.3) * mm, "end": v(-23.84, 51.01) * mm});
            skLineSegment(sketch, "E1298", {"start": v(-23.84, 51.01) * mm, "end": v(-23.8, 51) * mm});
            skLineSegment(sketch, "E1299", {"start": v(-23.8, 51) * mm, "end": v(-22.8, 50.69) * mm});
            skLineSegment(sketch, "E1300", {"start": v(-22.8, 50.69) * mm, "end": v(-22.8, 50.7) * mm});
            skLineSegment(sketch, "E1301", {"start": v(-22.8, 50.7) * mm, "end": v(-22.74, 50.75) * mm});
            skLineSegment(sketch, "E1302", {"start": v(-22.74, 50.75) * mm, "end": v(-22.74, 50.75) * mm});
            skLineSegment(sketch, "E1303", {"start": v(-22.74, 50.75) * mm, "end": v(-22.7, 50.8) * mm});
            skLineSegment(sketch, "E1304", {"start": v(-22.7, 50.8) * mm, "end": v(-22.7, 50.81) * mm});
            skLineSegment(sketch, "E1305", {"start": v(-22.7, 50.81) * mm, "end": v(-22.66, 50.87) * mm});
            skLineSegment(sketch, "E1306", {"start": v(-22.66, 50.87) * mm, "end": v(-22.65, 50.87) * mm});
            skLineSegment(sketch, "E1307", {"start": v(-22.65, 50.87) * mm, "end": v(-22.63, 50.93) * mm});
            skLineSegment(sketch, "E1308", {"start": v(-22.63, 50.93) * mm, "end": v(-22.63, 50.93) * mm});
            skLineSegment(sketch, "E1309", {"start": v(-22.63, 50.93) * mm, "end": v(-22.6, 51) * mm});
            skLineSegment(sketch, "E1310", {"start": v(-22.6, 51) * mm, "end": v(-22.6, 51) * mm});
            skLineSegment(sketch, "E1311", {"start": v(-22.6, 51) * mm, "end": v(-22.6, 51.05) * mm});
            skLineSegment(sketch, "E1312", {"start": v(-22.6, 51.05) * mm, "end": v(-22.6, 51.05) * mm});
            skLineSegment(sketch, "E1313", {"start": v(-22.6, 51.05) * mm, "end": v(-22.6, 51.1) * mm});
            skLineSegment(sketch, "E1314", {"start": v(-22.6, 51.1) * mm, "end": v(-22.6, 51.11) * mm});
            skLineSegment(sketch, "E1315", {"start": v(-22.6, 51.11) * mm, "end": v(-22.6, 51.17) * mm});
            skLineSegment(sketch, "E1316", {"start": v(-22.6, 51.17) * mm, "end": v(-22.6, 51.18) * mm});
            skLineSegment(sketch, "E1317", {"start": v(-22.6, 51.18) * mm, "end": v(-22.6, 51.23) * mm});
            skLineSegment(sketch, "E1318", {"start": v(-22.6, 51.23) * mm, "end": v(-22.63, 51.3) * mm});
            skLineSegment(sketch, "E1319", {"start": v(-22.63, 51.3) * mm, "end": v(-22.63, 51.3) * mm});
            skLineSegment(sketch, "E1320", {"start": v(-22.63, 51.3) * mm, "end": v(-22.68, 51.41) * mm});
            skLineSegment(sketch, "E1321", {"start": v(-22.68, 51.41) * mm, "end": v(-22.68, 51.42) * mm});
            skLineSegment(sketch, "E1322", {"start": v(-22.68, 51.42) * mm, "end": v(-22.75, 51.53) * mm});
            skLineSegment(sketch, "E1323", {"start": v(-22.75, 51.53) * mm, "end": v(-22.76, 51.54) * mm});
            skLineSegment(sketch, "E1324", {"start": v(-22.76, 51.54) * mm, "end": v(-22.85, 51.65) * mm});
            skLineSegment(sketch, "E1325", {"start": v(-22.85, 51.65) * mm, "end": v(-22.86, 51.66) * mm});
            skLineSegment(sketch, "E1326", {"start": v(-22.86, 51.66) * mm, "end": v(-22.87, 51.67) * mm});
            skLineSegment(sketch, "E1327", {"start": v(-22.87, 51.67) * mm, "end": v(-22.89, 51.69) * mm});
            skLineSegment(sketch, "E1328", {"start": v(14.65, -39.6) * mm, "end": v(14.64, -39.56) * mm});
            skLineSegment(sketch, "E1329", {"start": v(14.64, -39.56) * mm, "end": v(14.34, -38.9) * mm});
            skLineSegment(sketch, "E1330", {"start": v(14.34, -38.9) * mm, "end": v(14.33, -38.86) * mm});
            skLineSegment(sketch, "E1331", {"start": v(14.33, -38.86) * mm, "end": v(14.13, -38.1) * mm});
            skLineSegment(sketch, "E1332", {"start": v(14.13, -38.1) * mm, "end": v(14.12, -38.07) * mm});
            skLineSegment(sketch, "E1333", {"start": v(14.12, -38.07) * mm, "end": v(14, -37.24) * mm});
            skLineSegment(sketch, "E1334", {"start": v(14, -37.24) * mm, "end": v(14, -37.17) * mm});
            skLineSegment(sketch, "E1335", {"start": v(14, -37.17) * mm, "end": v(13.98, -36.28) * mm});
            skLineSegment(sketch, "E1336", {"start": v(13.98, -36.28) * mm, "end": v(13.99, -36.2) * mm});
            skLineSegment(sketch, "E1337", {"start": v(13.99, -36.2) * mm, "end": v(14.05, -35.26) * mm});
            skLineSegment(sketch, "E1338", {"start": v(14.05, -35.26) * mm, "end": v(14.19, -34.29) * mm});
            skLineSegment(sketch, "E1339", {"start": v(14.19, -34.29) * mm, "end": v(14.2, -34.21) * mm});
            skLineSegment(sketch, "E1340", {"start": v(14.2, -34.21) * mm, "end": v(14.42, -33.21) * mm});
            skLineSegment(sketch, "E1341", {"start": v(14.42, -33.21) * mm, "end": v(14.44, -33.13) * mm});
            skLineSegment(sketch, "E1342", {"start": v(14.44, -33.13) * mm, "end": v(14.72, -32.13) * mm});
            skLineSegment(sketch, "E1343", {"start": v(14.72, -32.13) * mm, "end": v(14.75, -32.05) * mm});
            skLineSegment(sketch, "E1344", {"start": v(14.75, -32.05) * mm, "end": v(15.1, -31.04) * mm});
            skLineSegment(sketch, "E1345", {"start": v(15.1, -31.04) * mm, "end": v(15.14, -30.96) * mm});
            skLineSegment(sketch, "E1346", {"start": v(15.14, -30.96) * mm, "end": v(15.55, -29.98) * mm});
            skLineSegment(sketch, "E1347", {"start": v(15.55, -29.98) * mm, "end": v(16.02, -29.02) * mm});
            skLineSegment(sketch, "E1348", {"start": v(16.02, -29.02) * mm, "end": v(16.06, -28.94) * mm});
            skLineSegment(sketch, "E1349", {"start": v(16.06, -28.94) * mm, "end": v(16.59, -28.03) * mm});
            skLineSegment(sketch, "E1350", {"start": v(16.59, -28.03) * mm, "end": v(16.63, -27.95) * mm});
            skLineSegment(sketch, "E1351", {"start": v(16.63, -27.95) * mm, "end": v(17.2, -27.1) * mm});
            skLineSegment(sketch, "E1352", {"start": v(17.2, -27.1) * mm, "end": v(17.23, -27.05) * mm});
            skLineSegment(sketch, "E1353", {"start": v(17.23, -27.05) * mm, "end": v(17.87, -26.23) * mm});
            skLineSegment(sketch, "E1354", {"start": v(17.87, -26.23) * mm, "end": v(17.9, -26.2) * mm});
            skLineSegment(sketch, "E1355", {"start": v(17.9, -26.2) * mm, "end": v(17.93, -26.17) * mm});
            skLineSegment(sketch, "E1356", {"start": v(17.93, -26.17) * mm, "end": v(18.7, -25.31) * mm});
            skLineSegment(sketch, "E1357", {"start": v(18.7, -25.31) * mm, "end": v(19.49, -24.5) * mm});
            skLineSegment(sketch, "E1358", {"start": v(19.49, -24.5) * mm, "end": v(19.55, -24.45) * mm});
            skLineSegment(sketch, "E1359", {"start": v(19.55, -24.45) * mm, "end": v(20.35, -23.7) * mm});
            skLineSegment(sketch, "E1360", {"start": v(20.35, -23.7) * mm, "end": v(20.41, -23.65) * mm});
            skLineSegment(sketch, "E1361", {"start": v(20.41, -23.65) * mm, "end": v(21.23, -22.95) * mm});
            skLineSegment(sketch, "E1362", {"start": v(21.23, -22.95) * mm, "end": v(21.3, -22.9) * mm});
            skLineSegment(sketch, "E1363", {"start": v(21.3, -22.9) * mm, "end": v(22.12, -22.27) * mm});
            skLineSegment(sketch, "E1364", {"start": v(22.12, -22.27) * mm, "end": v(22.18, -22.23) * mm});
            skLineSegment(sketch, "E1365", {"start": v(22.18, -22.23) * mm, "end": v(23.02, -21.67) * mm});
            skLineSegment(sketch, "E1366", {"start": v(23.02, -21.67) * mm, "end": v(23.85, -21.17) * mm});
            skLineSegment(sketch, "E1367", {"start": v(23.85, -21.17) * mm, "end": v(23.91, -21.14) * mm});
            skLineSegment(sketch, "E1368", {"start": v(23.91, -21.14) * mm, "end": v(24.74, -20.72) * mm});
            skLineSegment(sketch, "E1369", {"start": v(24.74, -20.72) * mm, "end": v(24.8, -20.69) * mm});
            skLineSegment(sketch, "E1370", {"start": v(24.8, -20.69) * mm, "end": v(25.63, -20.35) * mm});
            skLineSegment(sketch, "E1371", {"start": v(25.63, -20.35) * mm, "end": v(25.7, -20.33) * mm});
            skLineSegment(sketch, "E1372", {"start": v(25.7, -20.33) * mm, "end": v(26.5, -20.08) * mm});
            skLineSegment(sketch, "E1373", {"start": v(26.5, -20.08) * mm, "end": v(26.54, -20.06) * mm});
            skLineSegment(sketch, "E1374", {"start": v(26.54, -20.06) * mm, "end": v(27.34, -19.9) * mm});
            skLineSegment(sketch, "E1375", {"start": v(27.34, -19.9) * mm, "end": v(27.38, -19.9) * mm});
            skLineSegment(sketch, "E1376", {"start": v(27.38, -19.9) * mm, "end": v(28.15, -19.82) * mm});
            skLineSegment(sketch, "E1377", {"start": v(28.15, -19.82) * mm, "end": v(28.2, -19.82) * mm});
            skLineSegment(sketch, "E1378", {"start": v(28.2, -19.82) * mm, "end": v(28.23, -19.82) * mm});
            skLineSegment(sketch, "E1379", {"start": v(28.23, -19.82) * mm, "end": v(28.98, -19.84) * mm});
            skLineSegment(sketch, "E1380", {"start": v(28.98, -19.84) * mm, "end": v(29.02, -19.84) * mm});
            skLineSegment(sketch, "E1381", {"start": v(29.02, -19.84) * mm, "end": v(29.75, -19.97) * mm});
            skLineSegment(sketch, "E1382", {"start": v(29.75, -19.97) * mm, "end": v(29.78, -19.98) * mm});
            skLineSegment(sketch, "E1383", {"start": v(29.78, -19.98) * mm, "end": v(30.47, -20.2) * mm});
            skLineSegment(sketch, "E1384", {"start": v(30.47, -20.2) * mm, "end": v(30.5, -20.22) * mm});
            skLineSegment(sketch, "E1385", {"start": v(30.5, -20.22) * mm, "end": v(31.17, -20.56) * mm});
            skLineSegment(sketch, "E1386", {"start": v(31.17, -20.56) * mm, "end": v(31.2, -20.58) * mm});
            skLineSegment(sketch, "E1387", {"start": v(31.2, -20.58) * mm, "end": v(31.2, -20.59) * mm});
            skLineSegment(sketch, "E1388", {"start": v(31.2, -20.59) * mm, "end": v(31.22, -20.6) * mm});
            skLineSegment(sketch, "E1389", {"start": v(31.22, -20.6) * mm, "end": v(31.41, -20.77) * mm});
            skLineSegment(sketch, "E1390", {"start": v(31.41, -20.77) * mm, "end": v(31.6, -20.97) * mm});
            skLineSegment(sketch, "E1391", {"start": v(31.6, -20.97) * mm, "end": v(31.61, -20.98) * mm});
            skLineSegment(sketch, "E1392", {"start": v(31.61, -20.98) * mm, "end": v(31.95, -21.44) * mm});
            skLineSegment(sketch, "E1393", {"start": v(31.95, -21.44) * mm, "end": v(31.96, -21.46) * mm});
            skLineSegment(sketch, "E1394", {"start": v(31.96, -21.46) * mm, "end": v(32.25, -22) * mm});
            skLineSegment(sketch, "E1395", {"start": v(32.25, -22) * mm, "end": v(32.27, -22.03) * mm});
            skLineSegment(sketch, "E1396", {"start": v(32.27, -22.03) * mm, "end": v(32.5, -22.64) * mm});
            skLineSegment(sketch, "E1397", {"start": v(32.5, -22.64) * mm, "end": v(32.53, -22.7) * mm});
            skLineSegment(sketch, "E1398", {"start": v(32.53, -22.7) * mm, "end": v(32.72, -23.38) * mm});
            skLineSegment(sketch, "E1399", {"start": v(32.72, -23.38) * mm, "end": v(32.74, -23.45) * mm});
            skLineSegment(sketch, "E1400", {"start": v(32.74, -23.45) * mm, "end": v(32.87, -24.2) * mm});
            skLineSegment(sketch, "E1401", {"start": v(32.87, -24.2) * mm, "end": v(32.95, -25.01) * mm});
            skLineSegment(sketch, "E1402", {"start": v(32.95, -25.01) * mm, "end": v(32.96, -25.07) * mm});
            skLineSegment(sketch, "E1403", {"start": v(32.96, -25.07) * mm, "end": v(32.98, -25.94) * mm});
            skLineSegment(sketch, "E1404", {"start": v(32.98, -25.94) * mm, "end": v(32.98, -26) * mm});
            skLineSegment(sketch, "E1405", {"start": v(32.98, -26) * mm, "end": v(32.94, -26.92) * mm});
            skLineSegment(sketch, "E1406", {"start": v(32.94, -26.92) * mm, "end": v(32.93, -26.99) * mm});
            skLineSegment(sketch, "E1407", {"start": v(32.93, -26.99) * mm, "end": v(32.82, -27.94) * mm});
            skLineSegment(sketch, "E1408", {"start": v(32.82, -27.94) * mm, "end": v(32.81, -28.02) * mm});
            skLineSegment(sketch, "E1409", {"start": v(32.81, -28.02) * mm, "end": v(32.64, -29) * mm});
            skLineSegment(sketch, "E1410", {"start": v(32.64, -29) * mm, "end": v(32.4, -30.02) * mm});
            skLineSegment(sketch, "E1411", {"start": v(32.4, -30.02) * mm, "end": v(32.37, -30.1) * mm});
            skLineSegment(sketch, "E1412", {"start": v(32.37, -30.1) * mm, "end": v(32.05, -31.14) * mm});
            skLineSegment(sketch, "E1413", {"start": v(32.05, -31.14) * mm, "end": v(32.03, -31.22) * mm});
            skLineSegment(sketch, "E1414", {"start": v(32.03, -31.22) * mm, "end": v(31.63, -32.28) * mm});
            skLineSegment(sketch, "E1415", {"start": v(31.63, -32.28) * mm, "end": v(31.6, -32.36) * mm});
            skLineSegment(sketch, "E1416", {"start": v(31.6, -32.36) * mm, "end": v(31.12, -33.43) * mm});
            skLineSegment(sketch, "E1417", {"start": v(31.12, -33.43) * mm, "end": v(31.1, -33.48) * mm});
            skLineSegment(sketch, "E1418", {"start": v(31.1, -33.48) * mm, "end": v(30.52, -34.6) * mm});
            skLineSegment(sketch, "E1419", {"start": v(30.52, -34.6) * mm, "end": v(30.47, -34.66) * mm});
            skLineSegment(sketch, "E1420", {"start": v(30.47, -34.66) * mm, "end": v(29.57, -35.86) * mm});
            skLineSegment(sketch, "E1421", {"start": v(29.57, -35.86) * mm, "end": v(29.52, -35.92) * mm});
            skLineSegment(sketch, "E1422", {"start": v(29.52, -35.92) * mm, "end": v(28.59, -36.99) * mm});
            skLineSegment(sketch, "E1423", {"start": v(28.59, -36.99) * mm, "end": v(28.54, -37.04) * mm});
            skLineSegment(sketch, "E1424", {"start": v(28.54, -37.04) * mm, "end": v(27.57, -37.97) * mm});
            skLineSegment(sketch, "E1425", {"start": v(27.57, -37.97) * mm, "end": v(27.52, -38.02) * mm});
            skLineSegment(sketch, "E1426", {"start": v(27.52, -38.02) * mm, "end": v(26.54, -38.83) * mm});
            skLineSegment(sketch, "E1427", {"start": v(26.54, -38.83) * mm, "end": v(26.48, -38.87) * mm});
            skLineSegment(sketch, "E1428", {"start": v(26.48, -38.87) * mm, "end": v(25.49, -39.55) * mm});
            skLineSegment(sketch, "E1429", {"start": v(25.49, -39.55) * mm, "end": v(25.43, -39.58) * mm});
            skLineSegment(sketch, "E1430", {"start": v(25.43, -39.58) * mm, "end": v(24.44, -40.15) * mm});
            skLineSegment(sketch, "E1431", {"start": v(24.44, -40.15) * mm, "end": v(24.38, -40.18) * mm});
            skLineSegment(sketch, "E1432", {"start": v(24.38, -40.18) * mm, "end": v(23.4, -40.64) * mm});
            skLineSegment(sketch, "E1433", {"start": v(23.4, -40.64) * mm, "end": v(23.34, -40.66) * mm});
            skLineSegment(sketch, "E1434", {"start": v(23.34, -40.66) * mm, "end": v(22.36, -41) * mm});
            skLineSegment(sketch, "E1435", {"start": v(22.36, -41) * mm, "end": v(22.3, -41.03) * mm});
            skLineSegment(sketch, "E1436", {"start": v(22.3, -41.03) * mm, "end": v(21.34, -41.28) * mm});
            skLineSegment(sketch, "E1437", {"start": v(21.34, -41.28) * mm, "end": v(21.27, -41.3) * mm});
            skLineSegment(sketch, "E1438", {"start": v(21.27, -41.3) * mm, "end": v(20.35, -41.45) * mm});
            skLineSegment(sketch, "E1439", {"start": v(20.35, -41.45) * mm, "end": v(20.29, -41.46) * mm});
            skLineSegment(sketch, "E1440", {"start": v(20.29, -41.46) * mm, "end": v(19.4, -41.53) * mm});
            skLineSegment(sketch, "E1441", {"start": v(19.4, -41.53) * mm, "end": v(19.34, -41.53) * mm});
            skLineSegment(sketch, "E1442", {"start": v(19.34, -41.53) * mm, "end": v(18.5, -41.52) * mm});
            skLineSegment(sketch, "E1443", {"start": v(18.5, -41.52) * mm, "end": v(18.45, -41.51) * mm});
            skLineSegment(sketch, "E1444", {"start": v(18.45, -41.51) * mm, "end": v(17.67, -41.42) * mm});
            skLineSegment(sketch, "E1445", {"start": v(17.67, -41.42) * mm, "end": v(17.62, -41.41) * mm});
            skLineSegment(sketch, "E1446", {"start": v(17.62, -41.41) * mm, "end": v(16.9, -41.25) * mm});
            skLineSegment(sketch, "E1447", {"start": v(16.9, -41.25) * mm, "end": v(16.86, -41.23) * mm});
            skLineSegment(sketch, "E1448", {"start": v(16.86, -41.23) * mm, "end": v(16.21, -41) * mm});
            skLineSegment(sketch, "E1449", {"start": v(16.21, -41) * mm, "end": v(16.2, -41) * mm});
            skLineSegment(sketch, "E1450", {"start": v(16.2, -41) * mm, "end": v(15.61, -40.7) * mm});
            skLineSegment(sketch, "E1451", {"start": v(15.61, -40.7) * mm, "end": v(15.6, -40.69) * mm});
            skLineSegment(sketch, "E1452", {"start": v(15.6, -40.69) * mm, "end": v(15.59, -40.67) * mm});
            skLineSegment(sketch, "E1453", {"start": v(15.59, -40.67) * mm, "end": v(15.32, -40.46) * mm});
            skLineSegment(sketch, "E1454", {"start": v(15.32, -40.46) * mm, "end": v(15.08, -40.21) * mm});
            skLineSegment(sketch, "E1455", {"start": v(15.08, -40.21) * mm, "end": v(15.06, -40.2) * mm});
            skLineSegment(sketch, "E1456", {"start": v(15.06, -40.2) * mm, "end": v(14.85, -39.92) * mm});
            skLineSegment(sketch, "E1457", {"start": v(14.85, -39.92) * mm, "end": v(14.67, -39.62) * mm});
            skLineSegment(sketch, "E1458", {"start": v(14.67, -39.62) * mm, "end": v(14.65, -39.6) * mm});
            skLineSegment(sketch, "E1459", {"start": v(39.87, -8.63) * mm, "end": v(39.74, -7.13) * mm});
            skLineSegment(sketch, "E1460", {"start": v(39.74, -7.13) * mm, "end": v(39.73, -7.07) * mm});
            skLineSegment(sketch, "E1461", {"start": v(39.73, -7.07) * mm, "end": v(39.72, -7.02) * mm});
            skLineSegment(sketch, "E1462", {"start": v(39.72, -7.02) * mm, "end": v(39.41, -5.52) * mm});
            skLineSegment(sketch, "E1463", {"start": v(39.41, -5.52) * mm, "end": v(39.4, -5.45) * mm});
            skLineSegment(sketch, "E1464", {"start": v(39.4, -5.45) * mm, "end": v(38.9, -3.98) * mm});
            skLineSegment(sketch, "E1465", {"start": v(38.9, -3.98) * mm, "end": v(38.88, -3.91) * mm});
            skLineSegment(sketch, "E1466", {"start": v(38.88, -3.91) * mm, "end": v(38.2, -2.49) * mm});
            skLineSegment(sketch, "E1467", {"start": v(38.2, -2.49) * mm, "end": v(38.16, -2.42) * mm});
            skLineSegment(sketch, "E1468", {"start": v(38.16, -2.42) * mm, "end": v(37.75, -1.73) * mm});
            skLineSegment(sketch, "E1469", {"start": v(37.75, -1.73) * mm, "end": v(37.7, -1.67) * mm});
            skLineSegment(sketch, "E1470", {"start": v(37.7, -1.67) * mm, "end": v(37.24, -1) * mm});
            skLineSegment(sketch, "E1471", {"start": v(37.24, -1) * mm, "end": v(37.19, -0.94) * mm});
            skLineSegment(sketch, "E1472", {"start": v(37.19, -0.94) * mm, "end": v(36.66, -0.3) * mm});
            skLineSegment(sketch, "E1473", {"start": v(36.66, -0.3) * mm, "end": v(36.09, 0.33) * mm});
            skLineSegment(sketch, "E1474", {"start": v(36.09, 0.33) * mm, "end": v(36.03, 0.4) * mm});
            skLineSegment(sketch, "E1475", {"start": v(36.03, 0.4) * mm, "end": v(35.4, 0.98) * mm});
            skLineSegment(sketch, "E1476", {"start": v(35.4, 0.98) * mm, "end": v(34.7, 1.55) * mm});
            skLineSegment(sketch, "E1477", {"start": v(34.7, 1.55) * mm, "end": v(34.64, 1.6) * mm});
            skLineSegment(sketch, "E1478", {"start": v(34.64, 1.6) * mm, "end": v(33.9, 2.13) * mm});
            skLineSegment(sketch, "E1479", {"start": v(33.9, 2.13) * mm, "end": v(33.08, 2.63) * mm});
            skLineSegment(sketch, "E1480", {"start": v(33.08, 2.63) * mm, "end": v(33.03, 2.67) * mm});
            skLineSegment(sketch, "E1481", {"start": v(33.03, 2.67) * mm, "end": v(33, 2.68) * mm});
            skLineSegment(sketch, "E1482", {"start": v(33, 2.68) * mm, "end": v(32.75, 2.74) * mm});
            skLineSegment(sketch, "E1483", {"start": v(32.75, 2.74) * mm, "end": v(32.73, 2.74) * mm});
            skLineSegment(sketch, "E1484", {"start": v(32.73, 2.74) * mm, "end": v(32.5, 2.75) * mm});
            skLineSegment(sketch, "E1485", {"start": v(32.5, 2.75) * mm, "end": v(32.48, 2.75) * mm});
            skLineSegment(sketch, "E1486", {"start": v(32.48, 2.75) * mm, "end": v(32.47, 2.75) * mm});
            skLineSegment(sketch, "E1487", {"start": v(32.47, 2.75) * mm, "end": v(32.25, 2.73) * mm});
            skLineSegment(sketch, "E1488", {"start": v(32.25, 2.73) * mm, "end": v(32.24, 2.73) * mm});
            skLineSegment(sketch, "E1489", {"start": v(32.24, 2.73) * mm, "end": v(32.03, 2.68) * mm});
            skLineSegment(sketch, "E1490", {"start": v(32.03, 2.68) * mm, "end": v(32, 2.67) * mm});
            skLineSegment(sketch, "E1491", {"start": v(32, 2.67) * mm, "end": v(31.8, 2.59) * mm});
            skLineSegment(sketch, "E1492", {"start": v(31.8, 2.59) * mm, "end": v(31.8, 2.58) * mm});
            skLineSegment(sketch, "E1493", {"start": v(31.8, 2.58) * mm, "end": v(31.61, 2.47) * mm});
            skLineSegment(sketch, "E1494", {"start": v(31.61, 2.47) * mm, "end": v(31.6, 2.46) * mm});
            skLineSegment(sketch, "E1495", {"start": v(31.6, 2.46) * mm, "end": v(31.6, 2.46) * mm});
            skLineSegment(sketch, "E1496", {"start": v(31.6, 2.46) * mm, "end": v(31.42, 2.3) * mm});
            skLineSegment(sketch, "E1497", {"start": v(31.42, 2.3) * mm, "end": v(31.4, 2.3) * mm});
            skLineSegment(sketch, "E1498", {"start": v(31.4, 2.3) * mm, "end": v(31.24, 2.12) * mm});
            skLineSegment(sketch, "E1499", {"start": v(31.24, 2.12) * mm, "end": v(31.09, 1.92) * mm});
            skLineSegment(sketch, "E1500", {"start": v(31.09, 1.92) * mm, "end": v(31.08, 1.9) * mm});
            skLineSegment(sketch, "E1501", {"start": v(31.08, 1.9) * mm, "end": v(30.94, 1.67) * mm});
            skLineSegment(sketch, "E1502", {"start": v(30.94, 1.67) * mm, "end": v(30.93, 1.65) * mm});
            skLineSegment(sketch, "E1503", {"start": v(30.93, 1.65) * mm, "end": v(30.68, 1.12) * mm});
            skLineSegment(sketch, "E1504", {"start": v(30.68, 1.12) * mm, "end": v(30.66, 1.07) * mm});
            skLineSegment(sketch, "E1505", {"start": v(30.66, 1.07) * mm, "end": v(30.46, 0.44) * mm});
            skLineSegment(sketch, "E1506", {"start": v(30.46, 0.44) * mm, "end": v(30.44, 0.38) * mm});
            skLineSegment(sketch, "E1507", {"start": v(30.44, 0.38) * mm, "end": v(30.28, -0.32) * mm});
            skLineSegment(sketch, "E1508", {"start": v(30.28, -0.32) * mm, "end": v(30.17, -1.1) * mm});
            skLineSegment(sketch, "E1509", {"start": v(30.17, -1.1) * mm, "end": v(30.16, -1.17) * mm});
            skLineSegment(sketch, "E1510", {"start": v(30.16, -1.17) * mm, "end": v(30.08, -2.02) * mm});
            skLineSegment(sketch, "E1511", {"start": v(30.08, -2.02) * mm, "end": v(30.08, -2.1) * mm});
            skLineSegment(sketch, "E1512", {"start": v(30.08, -2.1) * mm, "end": v(30.04, -3) * mm});
            skLineSegment(sketch, "E1513", {"start": v(30.04, -3) * mm, "end": v(30.03, -3.07) * mm});
            skLineSegment(sketch, "E1514", {"start": v(30.03, -3.07) * mm, "end": v(30.03, -4.02) * mm});
            skLineSegment(sketch, "E1515", {"start": v(30.03, -4.02) * mm, "end": v(30.03, -4.1) * mm});
            skLineSegment(sketch, "E1516", {"start": v(30.03, -4.1) * mm, "end": v(30.13, -6.1) * mm});
            skLineSegment(sketch, "E1517", {"start": v(30.13, -6.1) * mm, "end": v(30.14, -6.18) * mm});
            skLineSegment(sketch, "E1518", {"start": v(30.14, -6.18) * mm, "end": v(30.37, -8.24) * mm});
            skLineSegment(sketch, "E1519", {"start": v(30.37, -8.24) * mm, "end": v(30.38, -8.33) * mm});
            skLineSegment(sketch, "E1520", {"start": v(30.38, -8.33) * mm, "end": v(30.4, -8.41) * mm});
            skLineSegment(sketch, "E1521", {"start": v(30.4, -8.41) * mm, "end": v(30.74, -10.47) * mm});
            skLineSegment(sketch, "E1522", {"start": v(30.74, -10.47) * mm, "end": v(30.75, -10.56) * mm});
            skLineSegment(sketch, "E1523", {"start": v(30.75, -10.56) * mm, "end": v(31.2, -12.53) * mm});
            skLineSegment(sketch, "E1524", {"start": v(31.2, -12.53) * mm, "end": v(31.22, -12.61) * mm});
            skLineSegment(sketch, "E1525", {"start": v(31.22, -12.61) * mm, "end": v(31.25, -12.7) * mm});
            skLineSegment(sketch, "E1526", {"start": v(31.25, -12.7) * mm, "end": v(31.79, -14.52) * mm});
            skLineSegment(sketch, "E1527", {"start": v(31.79, -14.52) * mm, "end": v(31.81, -14.59) * mm});
            skLineSegment(sketch, "E1528", {"start": v(31.81, -14.59) * mm, "end": v(32.12, -15.42) * mm});
            skLineSegment(sketch, "E1529", {"start": v(32.12, -15.42) * mm, "end": v(32.14, -15.48) * mm});
            skLineSegment(sketch, "E1530", {"start": v(32.14, -15.48) * mm, "end": v(32.46, -16.25) * mm});
            skLineSegment(sketch, "E1531", {"start": v(32.46, -16.25) * mm, "end": v(32.8, -16.94) * mm});
            skLineSegment(sketch, "E1532", {"start": v(32.8, -16.94) * mm, "end": v(32.83, -17) * mm});
            skLineSegment(sketch, "E1533", {"start": v(32.83, -17) * mm, "end": v(33.19, -17.6) * mm});
            skLineSegment(sketch, "E1534", {"start": v(33.19, -17.6) * mm, "end": v(33.22, -17.64) * mm});
            skLineSegment(sketch, "E1535", {"start": v(33.22, -17.64) * mm, "end": v(33.58, -18.15) * mm});
            skLineSegment(sketch, "E1536", {"start": v(33.58, -18.15) * mm, "end": v(33.6, -18.17) * mm});
            skLineSegment(sketch, "E1537", {"start": v(33.6, -18.17) * mm, "end": v(33.98, -18.57) * mm});
            skLineSegment(sketch, "E1538", {"start": v(33.98, -18.57) * mm, "end": v(34, -18.59) * mm});
            skLineSegment(sketch, "E1539", {"start": v(34, -18.59) * mm, "end": v(34.2, -18.75) * mm});
            skLineSegment(sketch, "E1540", {"start": v(34.2, -18.75) * mm, "end": v(34.2, -18.76) * mm});
            skLineSegment(sketch, "E1541", {"start": v(34.2, -18.76) * mm, "end": v(34.4, -18.9) * mm});
            skLineSegment(sketch, "E1542", {"start": v(34.4, -18.9) * mm, "end": v(34.42, -18.9) * mm});
            skLineSegment(sketch, "E1543", {"start": v(34.42, -18.9) * mm, "end": v(34.62, -19) * mm});
            skLineSegment(sketch, "E1544", {"start": v(34.62, -19) * mm, "end": v(34.63, -19) * mm});
            skLineSegment(sketch, "E1545", {"start": v(34.63, -19) * mm, "end": v(34.84, -19.08) * mm});
            skLineSegment(sketch, "E1546", {"start": v(34.84, -19.08) * mm, "end": v(34.85, -19.08) * mm});
            skLineSegment(sketch, "E1547", {"start": v(34.85, -19.08) * mm, "end": v(35.05, -19.11) * mm});
            skLineSegment(sketch, "E1548", {"start": v(35.05, -19.11) * mm, "end": v(35.06, -19.11) * mm});
            skLineSegment(sketch, "E1549", {"start": v(35.06, -19.11) * mm, "end": v(35.27, -19.12) * mm});
            skLineSegment(sketch, "E1550", {"start": v(35.27, -19.12) * mm, "end": v(35.28, -19.12) * mm});
            skLineSegment(sketch, "E1551", {"start": v(35.28, -19.12) * mm, "end": v(35.28, -19.11) * mm});
            skLineSegment(sketch, "E1552", {"start": v(35.28, -19.11) * mm, "end": v(35.5, -19.08) * mm});
            skLineSegment(sketch, "E1553", {"start": v(35.5, -19.08) * mm, "end": v(35.5, -19.08) * mm});
            skLineSegment(sketch, "E1554", {"start": v(35.5, -19.08) * mm, "end": v(35.7, -19) * mm});
            skLineSegment(sketch, "E1555", {"start": v(35.7, -19) * mm, "end": v(35.72, -19) * mm});
            skLineSegment(sketch, "E1556", {"start": v(35.72, -19) * mm, "end": v(35.75, -18.97) * mm});
            skLineSegment(sketch, "E1557", {"start": v(35.75, -18.97) * mm, "end": v(36.63, -18.17) * mm});
            skLineSegment(sketch, "E1558", {"start": v(36.63, -18.17) * mm, "end": v(36.66, -18.14) * mm});
            skLineSegment(sketch, "E1559", {"start": v(36.66, -18.14) * mm, "end": v(37.44, -17.17) * mm});
            skLineSegment(sketch, "E1560", {"start": v(37.44, -17.17) * mm, "end": v(37.47, -17.14) * mm});
            skLineSegment(sketch, "E1561", {"start": v(37.47, -17.14) * mm, "end": v(37.5, -17.1) * mm});
            skLineSegment(sketch, "E1562", {"start": v(37.5, -17.1) * mm, "end": v(38.19, -16) * mm});
            skLineSegment(sketch, "E1563", {"start": v(38.19, -16) * mm, "end": v(38.21, -15.96) * mm});
            skLineSegment(sketch, "E1564", {"start": v(38.21, -15.96) * mm, "end": v(38.23, -15.91) * mm});
            skLineSegment(sketch, "E1565", {"start": v(38.23, -15.91) * mm, "end": v(38.8, -14.7) * mm});
            skLineSegment(sketch, "E1566", {"start": v(38.8, -14.7) * mm, "end": v(38.83, -14.64) * mm});
            skLineSegment(sketch, "E1567", {"start": v(38.83, -14.64) * mm, "end": v(39.28, -13.33) * mm});
            skLineSegment(sketch, "E1568", {"start": v(39.28, -13.33) * mm, "end": v(39.3, -13.28) * mm});
            skLineSegment(sketch, "E1569", {"start": v(39.3, -13.28) * mm, "end": v(39.31, -13.23) * mm});
            skLineSegment(sketch, "E1570", {"start": v(39.31, -13.23) * mm, "end": v(39.63, -11.83) * mm});
            skLineSegment(sketch, "E1571", {"start": v(39.63, -11.83) * mm, "end": v(39.65, -11.78) * mm});
            skLineSegment(sketch, "E1572", {"start": v(39.65, -11.78) * mm, "end": v(39.65, -11.73) * mm});
            skLineSegment(sketch, "E1573", {"start": v(39.65, -11.73) * mm, "end": v(39.84, -10.28) * mm});
            skLineSegment(sketch, "E1574", {"start": v(39.84, -10.28) * mm, "end": v(39.84, -10.23) * mm});
            skLineSegment(sketch, "E1575", {"start": v(39.84, -10.23) * mm, "end": v(39.87, -8.74) * mm});
            skLineSegment(sketch, "E1576", {"start": v(39.87, -8.74) * mm, "end": v(39.87, -8.68) * mm});
            skLineSegment(sketch, "E1577", {"start": v(39.87, -8.68) * mm, "end": v(39.87, -8.63) * mm});
            skLineSegment(sketch, "E1578", {"start": v(-31, -36.18) * mm, "end": v(-31.04, -36.14) * mm});
            skLineSegment(sketch, "E1579", {"start": v(-31.04, -36.14) * mm, "end": v(-32.02, -34.87) * mm});
            skLineSegment(sketch, "E1580", {"start": v(-32.02, -34.87) * mm, "end": v(-32.06, -34.82) * mm});
            skLineSegment(sketch, "E1581", {"start": v(-32.06, -34.82) * mm, "end": v(-32.09, -34.78) * mm});
            skLineSegment(sketch, "E1582", {"start": v(-32.09, -34.78) * mm, "end": v(-32.7, -33.83) * mm});
            skLineSegment(sketch, "E1583", {"start": v(-32.7, -33.83) * mm, "end": v(-32.73, -33.78) * mm});
            skLineSegment(sketch, "E1584", {"start": v(-32.73, -33.78) * mm, "end": v(-33.25, -32.77) * mm});
            skLineSegment(sketch, "E1585", {"start": v(-33.25, -32.77) * mm, "end": v(-33.27, -32.73) * mm});
            skLineSegment(sketch, "E1586", {"start": v(-33.27, -32.73) * mm, "end": v(-33.68, -31.67) * mm});
            skLineSegment(sketch, "E1587", {"start": v(-33.68, -31.67) * mm, "end": v(-33.7, -31.63) * mm});
            skLineSegment(sketch, "E1588", {"start": v(-33.7, -31.63) * mm, "end": v(-34.01, -30.54) * mm});
            skLineSegment(sketch, "E1589", {"start": v(-34.01, -30.54) * mm, "end": v(-34.04, -30.45) * mm});
            skLineSegment(sketch, "E1590", {"start": v(-34.04, -30.45) * mm, "end": v(-34.26, -29.34) * mm});
            skLineSegment(sketch, "E1591", {"start": v(-34.26, -29.34) * mm, "end": v(-34.28, -29.24) * mm});
            skLineSegment(sketch, "E1592", {"start": v(-34.28, -29.24) * mm, "end": v(-34.42, -28.14) * mm});
            skLineSegment(sketch, "E1593", {"start": v(-34.42, -28.14) * mm, "end": v(-34.43, -28.05) * mm});
            skLineSegment(sketch, "E1594", {"start": v(-34.43, -28.05) * mm, "end": v(-34.5, -26.95) * mm});
            skLineSegment(sketch, "E1595", {"start": v(-34.5, -26.95) * mm, "end": v(-34.49, -25.87) * mm});
            skLineSegment(sketch, "E1596", {"start": v(-34.49, -25.87) * mm, "end": v(-34.48, -25.78) * mm});
            skLineSegment(sketch, "E1597", {"start": v(-34.48, -25.78) * mm, "end": v(-34.41, -24.73) * mm});
            skLineSegment(sketch, "E1598", {"start": v(-34.41, -24.73) * mm, "end": v(-34.4, -24.65) * mm});
            skLineSegment(sketch, "E1599", {"start": v(-34.4, -24.65) * mm, "end": v(-34.28, -23.65) * mm});
            skLineSegment(sketch, "E1600", {"start": v(-34.28, -23.65) * mm, "end": v(-34.26, -23.58) * mm});
            skLineSegment(sketch, "E1601", {"start": v(-34.26, -23.58) * mm, "end": v(-34.08, -22.63) * mm});
            skLineSegment(sketch, "E1602", {"start": v(-34.08, -22.63) * mm, "end": v(-33.85, -21.76) * mm});
            skLineSegment(sketch, "E1603", {"start": v(-33.85, -21.76) * mm, "end": v(-33.84, -21.69) * mm});
            skLineSegment(sketch, "E1604", {"start": v(-33.84, -21.69) * mm, "end": v(-33.57, -20.9) * mm});
            skLineSegment(sketch, "E1605", {"start": v(-33.57, -20.9) * mm, "end": v(-33.55, -20.84) * mm});
            skLineSegment(sketch, "E1606", {"start": v(-33.55, -20.84) * mm, "end": v(-33.25, -20.14) * mm});
            skLineSegment(sketch, "E1607", {"start": v(-33.25, -20.14) * mm, "end": v(-33.22, -20.1) * mm});
            skLineSegment(sketch, "E1608", {"start": v(-33.22, -20.1) * mm, "end": v(-32.9, -19.5) * mm});
            skLineSegment(sketch, "E1609", {"start": v(-32.9, -19.5) * mm, "end": v(-32.88, -19.49) * mm});
            skLineSegment(sketch, "E1610", {"start": v(-32.88, -19.49) * mm, "end": v(-32.53, -19.02) * mm});
            skLineSegment(sketch, "E1611", {"start": v(-32.53, -19.02) * mm, "end": v(-32.52, -19) * mm});
            skLineSegment(sketch, "E1612", {"start": v(-32.52, -19) * mm, "end": v(-32.49, -18.98) * mm});
            skLineSegment(sketch, "E1613", {"start": v(-32.49, -18.98) * mm, "end": v(-31.87, -18.57) * mm});
            skLineSegment(sketch, "E1614", {"start": v(-31.87, -18.57) * mm, "end": v(-31.84, -18.56) * mm});
            skLineSegment(sketch, "E1615", {"start": v(-31.84, -18.56) * mm, "end": v(-31.52, -18.4) * mm});
            skLineSegment(sketch, "E1616", {"start": v(-31.52, -18.4) * mm, "end": v(-31.2, -18.27) * mm});
            skLineSegment(sketch, "E1617", {"start": v(-31.2, -18.27) * mm, "end": v(-31.16, -18.26) * mm});
            skLineSegment(sketch, "E1618", {"start": v(-31.16, -18.26) * mm, "end": v(-30.83, -18.17) * mm});
            skLineSegment(sketch, "E1619", {"start": v(-30.83, -18.17) * mm, "end": v(-30.8, -18.16) * mm});
            skLineSegment(sketch, "E1620", {"start": v(-30.8, -18.16) * mm, "end": v(-30.46, -18.1) * mm});
            skLineSegment(sketch, "E1621", {"start": v(-30.46, -18.1) * mm, "end": v(-30.43, -18.1) * mm});
            skLineSegment(sketch, "E1622", {"start": v(-30.43, -18.1) * mm, "end": v(-29.72, -18.05) * mm});
            skLineSegment(sketch, "E1623", {"start": v(-29.72, -18.05) * mm, "end": v(-29.69, -18.05) * mm});
            skLineSegment(sketch, "E1624", {"start": v(-29.69, -18.05) * mm, "end": v(-28.96, -18.11) * mm});
            skLineSegment(sketch, "E1625", {"start": v(-28.96, -18.11) * mm, "end": v(-28.93, -18.12) * mm});
            skLineSegment(sketch, "E1626", {"start": v(-28.93, -18.12) * mm, "end": v(-28.18, -18.3) * mm});
            skLineSegment(sketch, "E1627", {"start": v(-28.18, -18.3) * mm, "end": v(-28.15, -18.3) * mm});
            skLineSegment(sketch, "E1628", {"start": v(-28.15, -18.3) * mm, "end": v(-28.09, -18.32) * mm});
            skLineSegment(sketch, "E1629", {"start": v(-28.09, -18.32) * mm, "end": v(-27.32, -18.6) * mm});
            skLineSegment(sketch, "E1630", {"start": v(-27.32, -18.6) * mm, "end": v(-26.54, -18.96) * mm});
            skLineSegment(sketch, "E1631", {"start": v(-26.54, -18.96) * mm, "end": v(-26.48, -18.99) * mm});
            skLineSegment(sketch, "E1632", {"start": v(-26.48, -18.99) * mm, "end": v(-25.68, -19.44) * mm});
            skLineSegment(sketch, "E1633", {"start": v(-25.68, -19.44) * mm, "end": v(-25.62, -19.48) * mm});
            skLineSegment(sketch, "E1634", {"start": v(-25.62, -19.48) * mm, "end": v(-24.82, -20) * mm});
            skLineSegment(sketch, "E1635", {"start": v(-24.82, -20) * mm, "end": v(-24.75, -20.06) * mm});
            skLineSegment(sketch, "E1636", {"start": v(-24.75, -20.06) * mm, "end": v(-23.94, -20.66) * mm});
            skLineSegment(sketch, "E1637", {"start": v(-23.94, -20.66) * mm, "end": v(-23.13, -21.34) * mm});
            skLineSegment(sketch, "E1638", {"start": v(-23.13, -21.34) * mm, "end": v(-23.07, -21.4) * mm});
            skLineSegment(sketch, "E1639", {"start": v(-23.07, -21.4) * mm, "end": v(-22.25, -22.14) * mm});
            skLineSegment(sketch, "E1640", {"start": v(-22.25, -22.14) * mm, "end": v(-22.19, -22.2) * mm});
            skLineSegment(sketch, "E1641", {"start": v(-22.19, -22.2) * mm, "end": v(-21.37, -23) * mm});
            skLineSegment(sketch, "E1642", {"start": v(-21.37, -23) * mm, "end": v(-21.3, -23.06) * mm});
            skLineSegment(sketch, "E1643", {"start": v(-21.3, -23.06) * mm, "end": v(-19.7, -24.8) * mm});
            skLineSegment(sketch, "E1644", {"start": v(-19.7, -24.8) * mm, "end": v(-19.63, -24.88) * mm});
            skLineSegment(sketch, "E1645", {"start": v(-19.63, -24.88) * mm, "end": v(-19.6, -24.92) * mm});
            skLineSegment(sketch, "E1646", {"start": v(-19.6, -24.92) * mm, "end": v(-18.9, -25.76) * mm});
            skLineSegment(sketch, "E1647", {"start": v(-18.9, -25.76) * mm, "end": v(-18.87, -25.8) * mm});
            skLineSegment(sketch, "E1648", {"start": v(-18.87, -25.8) * mm, "end": v(-18.21, -26.72) * mm});
            skLineSegment(sketch, "E1649", {"start": v(-18.21, -26.72) * mm, "end": v(-18.15, -26.82) * mm});
            skLineSegment(sketch, "E1650", {"start": v(-18.15, -26.82) * mm, "end": v(-17.55, -27.8) * mm});
            skLineSegment(sketch, "E1651", {"start": v(-17.55, -27.8) * mm, "end": v(-17, -28.83) * mm});
            skLineSegment(sketch, "E1652", {"start": v(-17, -28.83) * mm, "end": v(-16.95, -28.93) * mm});
            skLineSegment(sketch, "E1653", {"start": v(-16.95, -28.93) * mm, "end": v(-16.46, -30) * mm});
            skLineSegment(sketch, "E1654", {"start": v(-16.46, -30) * mm, "end": v(-16.03, -31.08) * mm});
            skLineSegment(sketch, "E1655", {"start": v(-16.03, -31.08) * mm, "end": v(-15.99, -31.19) * mm});
            skLineSegment(sketch, "E1656", {"start": v(-15.99, -31.19) * mm, "end": v(-15.63, -32.28) * mm});
            skLineSegment(sketch, "E1657", {"start": v(-15.63, -32.28) * mm, "end": v(-15.6, -32.36) * mm});
            skLineSegment(sketch, "E1658", {"start": v(-15.6, -32.36) * mm, "end": v(-15.32, -33.44) * mm});
            skLineSegment(sketch, "E1659", {"start": v(-15.32, -33.44) * mm, "end": v(-15.3, -33.52) * mm});
            skLineSegment(sketch, "E1660", {"start": v(-15.3, -33.52) * mm, "end": v(-15.1, -34.59) * mm});
            skLineSegment(sketch, "E1661", {"start": v(-15.1, -34.59) * mm, "end": v(-14.96, -35.62) * mm});
            skLineSegment(sketch, "E1662", {"start": v(-14.96, -35.62) * mm, "end": v(-14.95, -35.7) * mm});
            skLineSegment(sketch, "E1663", {"start": v(-14.95, -35.7) * mm, "end": v(-14.91, -36.68) * mm});
            skLineSegment(sketch, "E1664", {"start": v(-14.91, -36.68) * mm, "end": v(-14.91, -36.75) * mm});
            skLineSegment(sketch, "E1665", {"start": v(-14.91, -36.75) * mm, "end": v(-14.96, -37.67) * mm});
            skLineSegment(sketch, "E1666", {"start": v(-14.96, -37.67) * mm, "end": v(-14.97, -37.74) * mm});
            skLineSegment(sketch, "E1667", {"start": v(-14.97, -37.74) * mm, "end": v(-15.11, -38.58) * mm});
            skLineSegment(sketch, "E1668", {"start": v(-15.11, -38.58) * mm, "end": v(-15.13, -38.64) * mm});
            skLineSegment(sketch, "E1669", {"start": v(-15.13, -38.64) * mm, "end": v(-15.38, -39.4) * mm});
            skLineSegment(sketch, "E1670", {"start": v(-15.38, -39.4) * mm, "end": v(-15.38, -39.43) * mm});
            skLineSegment(sketch, "E1671", {"start": v(-15.38, -39.43) * mm, "end": v(-15.55, -39.77) * mm});
            skLineSegment(sketch, "E1672", {"start": v(-15.55, -39.77) * mm, "end": v(-15.56, -39.8) * mm});
            skLineSegment(sketch, "E1673", {"start": v(-15.56, -39.8) * mm, "end": v(-15.75, -40.1) * mm});
            skLineSegment(sketch, "E1674", {"start": v(-15.75, -40.1) * mm, "end": v(-15.77, -40.13) * mm});
            skLineSegment(sketch, "E1675", {"start": v(-15.77, -40.13) * mm, "end": v(-15.98, -40.41) * mm});
            skLineSegment(sketch, "E1676", {"start": v(-15.98, -40.41) * mm, "end": v(-16, -40.43) * mm});
            skLineSegment(sketch, "E1677", {"start": v(-16, -40.43) * mm, "end": v(-16.24, -40.69) * mm});
            skLineSegment(sketch, "E1678", {"start": v(-16.24, -40.69) * mm, "end": v(-16.27, -40.7) * mm});
            skLineSegment(sketch, "E1679", {"start": v(-16.27, -40.7) * mm, "end": v(-16.84, -41.04) * mm});
            skLineSegment(sketch, "E1680", {"start": v(-16.84, -41.04) * mm, "end": v(-16.87, -41.05) * mm});
            skLineSegment(sketch, "E1681", {"start": v(-16.87, -41.05) * mm, "end": v(-17.53, -41.33) * mm});
            skLineSegment(sketch, "E1682", {"start": v(-17.53, -41.33) * mm, "end": v(-17.57, -41.34) * mm});
            skLineSegment(sketch, "E1683", {"start": v(-17.57, -41.34) * mm, "end": v(-18.3, -41.55) * mm});
            skLineSegment(sketch, "E1684", {"start": v(-18.3, -41.55) * mm, "end": v(-18.34, -41.56) * mm});
            skLineSegment(sketch, "E1685", {"start": v(-18.34, -41.56) * mm, "end": v(-19.16, -41.7) * mm});
            skLineSegment(sketch, "E1686", {"start": v(-19.16, -41.7) * mm, "end": v(-19.2, -41.7) * mm});
            skLineSegment(sketch, "E1687", {"start": v(-19.2, -41.7) * mm, "end": v(-20.07, -41.77) * mm});
            skLineSegment(sketch, "E1688", {"start": v(-20.07, -41.77) * mm, "end": v(-20.12, -41.77) * mm});
            skLineSegment(sketch, "E1689", {"start": v(-20.12, -41.77) * mm, "end": v(-20.16, -41.77) * mm});
            skLineSegment(sketch, "E1690", {"start": v(-20.16, -41.77) * mm, "end": v(-21.1, -41.75) * mm});
            skLineSegment(sketch, "E1691", {"start": v(-21.1, -41.75) * mm, "end": v(-21.14, -41.75) * mm});
            skLineSegment(sketch, "E1692", {"start": v(-21.14, -41.75) * mm, "end": v(-22.12, -41.63) * mm});
            skLineSegment(sketch, "E1693", {"start": v(-22.12, -41.63) * mm, "end": v(-22.2, -41.62) * mm});
            skLineSegment(sketch, "E1694", {"start": v(-22.2, -41.62) * mm, "end": v(-23.2, -41.4) * mm});
            skLineSegment(sketch, "E1695", {"start": v(-23.2, -41.4) * mm, "end": v(-23.28, -41.38) * mm});
            skLineSegment(sketch, "E1696", {"start": v(-23.28, -41.38) * mm, "end": v(-24.32, -41.05) * mm});
            skLineSegment(sketch, "E1697", {"start": v(-24.32, -41.05) * mm, "end": v(-25.38, -40.61) * mm});
            skLineSegment(sketch, "E1698", {"start": v(-25.38, -40.61) * mm, "end": v(-25.45, -40.58) * mm});
            skLineSegment(sketch, "E1699", {"start": v(-25.45, -40.58) * mm, "end": v(-26.52, -40.02) * mm});
            skLineSegment(sketch, "E1700", {"start": v(-26.52, -40.02) * mm, "end": v(-26.6, -39.98) * mm});
            skLineSegment(sketch, "E1701", {"start": v(-26.6, -39.98) * mm, "end": v(-27.67, -39.3) * mm});
            skLineSegment(sketch, "E1702", {"start": v(-27.67, -39.3) * mm, "end": v(-27.74, -39.24) * mm});
            skLineSegment(sketch, "E1703", {"start": v(-27.74, -39.24) * mm, "end": v(-28.8, -38.41) * mm});
            skLineSegment(sketch, "E1704", {"start": v(-28.8, -38.41) * mm, "end": v(-28.88, -38.35) * mm});
            skLineSegment(sketch, "E1705", {"start": v(-28.88, -38.35) * mm, "end": v(-29.92, -37.38) * mm});
            skLineSegment(sketch, "E1706", {"start": v(-29.92, -37.38) * mm, "end": v(-29.96, -37.34) * mm});
            skLineSegment(sketch, "E1707", {"start": v(-29.96, -37.34) * mm, "end": v(-30.97, -36.23) * mm});
            skLineSegment(sketch, "E1708", {"start": v(-30.97, -36.23) * mm, "end": v(-31, -36.18) * mm});
            skLineSegment(sketch, "E1709", {"start": v(-23.02, -13.59) * mm, "end": v(-23.07, -13.55) * mm});
            skLineSegment(sketch, "E1710", {"start": v(-23.07, -13.55) * mm, "end": v(-23.94, -12.9) * mm});
            skLineSegment(sketch, "E1711", {"start": v(-23.94, -12.9) * mm, "end": v(-23.98, -12.87) * mm});
            skLineSegment(sketch, "E1712", {"start": v(-23.98, -12.87) * mm, "end": v(-24.76, -12.13) * mm});
            skLineSegment(sketch, "E1713", {"start": v(-24.76, -12.13) * mm, "end": v(-24.8, -12.09) * mm});
            skLineSegment(sketch, "E1714", {"start": v(-24.8, -12.09) * mm, "end": v(-25.47, -11.27) * mm});
            skLineSegment(sketch, "E1715", {"start": v(-25.47, -11.27) * mm, "end": v(-25.5, -11.22) * mm});
            skLineSegment(sketch, "E1716", {"start": v(-25.5, -11.22) * mm, "end": v(-26.08, -10.33) * mm});
            skLineSegment(sketch, "E1717", {"start": v(-26.08, -10.33) * mm, "end": v(-26.11, -10.28) * mm});
            skLineSegment(sketch, "E1718", {"start": v(-26.11, -10.28) * mm, "end": v(-26.6, -9.32) * mm});
            skLineSegment(sketch, "E1719", {"start": v(-26.6, -9.32) * mm, "end": v(-26.62, -9.26) * mm});
            skLineSegment(sketch, "E1720", {"start": v(-26.62, -9.26) * mm, "end": v(-27, -8.24) * mm});
            skLineSegment(sketch, "E1721", {"start": v(-27, -8.24) * mm, "end": v(-27.02, -8.2) * mm});
            skLineSegment(sketch, "E1722", {"start": v(-27.02, -8.2) * mm, "end": v(-27.04, -8.14) * mm});
            skLineSegment(sketch, "E1723", {"start": v(-27.04, -8.14) * mm, "end": v(-27.32, -7.07) * mm});
            skLineSegment(sketch, "E1724", {"start": v(-27.32, -7.07) * mm, "end": v(-27.33, -6.99) * mm});
            skLineSegment(sketch, "E1725", {"start": v(-27.33, -6.99) * mm, "end": v(-27.51, -5.88) * mm});
            skLineSegment(sketch, "E1726", {"start": v(-27.51, -5.88) * mm, "end": v(-27.6, -4.74) * mm});
            skLineSegment(sketch, "E1727", {"start": v(-27.6, -4.74) * mm, "end": v(-27.6, -4.66) * mm});
            skLineSegment(sketch, "E1728", {"start": v(-27.6, -4.66) * mm, "end": v(-27.57, -3.5) * mm});
            skLineSegment(sketch, "E1729", {"start": v(-27.57, -3.5) * mm, "end": v(-27.57, -3.4) * mm});
            skLineSegment(sketch, "E1730", {"start": v(-27.57, -3.4) * mm, "end": v(-27.44, -2.23) * mm});
            skLineSegment(sketch, "E1731", {"start": v(-27.44, -2.23) * mm, "end": v(-27.43, -2.14) * mm});
            skLineSegment(sketch, "E1732", {"start": v(-27.43, -2.14) * mm, "end": v(-27.2, -0.96) * mm});
            skLineSegment(sketch, "E1733", {"start": v(-27.2, -0.96) * mm, "end": v(-27.17, -0.87) * mm});
            skLineSegment(sketch, "E1734", {"start": v(-27.17, -0.87) * mm, "end": v(-26.83, 0.32) * mm});
            skLineSegment(sketch, "E1735", {"start": v(-26.83, 0.32) * mm, "end": v(-26.8, 0.4) * mm});
            skLineSegment(sketch, "E1736", {"start": v(-26.8, 0.4) * mm, "end": v(-26.36, 1.58) * mm});
            skLineSegment(sketch, "E1737", {"start": v(-26.36, 1.58) * mm, "end": v(-26.32, 1.66) * mm});
            skLineSegment(sketch, "E1738", {"start": v(-26.32, 1.66) * mm, "end": v(-25.77, 2.82) * mm});
            skLineSegment(sketch, "E1739", {"start": v(-25.77, 2.82) * mm, "end": v(-25.74, 2.87) * mm});
            skLineSegment(sketch, "E1740", {"start": v(-25.74, 2.87) * mm, "end": v(-25.05, 4.04) * mm});
            skLineSegment(sketch, "E1741", {"start": v(-25.05, 4.04) * mm, "end": v(-25.01, 4.1) * mm});
            skLineSegment(sketch, "E1742", {"start": v(-25.01, 4.1) * mm, "end": v(-24.26, 5.13) * mm});
            skLineSegment(sketch, "E1743", {"start": v(-24.26, 5.13) * mm, "end": v(-24.2, 5.18) * mm});
            skLineSegment(sketch, "E1744", {"start": v(-24.2, 5.18) * mm, "end": v(-23.38, 6.13) * mm});
            skLineSegment(sketch, "E1745", {"start": v(-23.38, 6.13) * mm, "end": v(-23.33, 6.18) * mm});
            skLineSegment(sketch, "E1746", {"start": v(-23.33, 6.18) * mm, "end": v(-22.43, 7.04) * mm});
            skLineSegment(sketch, "E1747", {"start": v(-22.43, 7.04) * mm, "end": v(-22.38, 7.09) * mm});
            skLineSegment(sketch, "E1748", {"start": v(-22.38, 7.09) * mm, "end": v(-21.43, 7.85) * mm});
            skLineSegment(sketch, "E1749", {"start": v(-21.43, 7.85) * mm, "end": v(-21.38, 7.9) * mm});
            skLineSegment(sketch, "E1750", {"start": v(-21.38, 7.9) * mm, "end": v(-20.38, 8.56) * mm});
            skLineSegment(sketch, "E1751", {"start": v(-20.38, 8.56) * mm, "end": v(-20.32, 8.6) * mm});
            skLineSegment(sketch, "E1752", {"start": v(-20.32, 8.6) * mm, "end": v(-19.29, 9.17) * mm});
            skLineSegment(sketch, "E1753", {"start": v(-19.29, 9.17) * mm, "end": v(-19.23, 9.2) * mm});
            skLineSegment(sketch, "E1754", {"start": v(-19.23, 9.2) * mm, "end": v(-18.16, 9.67) * mm});
            skLineSegment(sketch, "E1755", {"start": v(-18.16, 9.67) * mm, "end": v(-18.1, 9.7) * mm});
            skLineSegment(sketch, "E1756", {"start": v(-18.1, 9.7) * mm, "end": v(-17.01, 10.07) * mm});
            skLineSegment(sketch, "E1757", {"start": v(-17.01, 10.07) * mm, "end": v(-16.94, 10.09) * mm});
            skLineSegment(sketch, "E1758", {"start": v(-16.94, 10.09) * mm, "end": v(-15.84, 10.36) * mm});
            skLineSegment(sketch, "E1759", {"start": v(-15.84, 10.36) * mm, "end": v(-15.76, 10.37) * mm});
            skLineSegment(sketch, "E1760", {"start": v(-15.76, 10.37) * mm, "end": v(-14.65, 10.53) * mm});
            skLineSegment(sketch, "E1761", {"start": v(-14.65, 10.53) * mm, "end": v(-14.58, 10.53) * mm});
            skLineSegment(sketch, "E1762", {"start": v(-14.58, 10.53) * mm, "end": v(-13.47, 10.58) * mm});
            skLineSegment(sketch, "E1763", {"start": v(-13.47, 10.58) * mm, "end": v(-13.4, 10.58) * mm});
            skLineSegment(sketch, "E1764", {"start": v(-13.4, 10.58) * mm, "end": v(-12.3, 10.52) * mm});
            skLineSegment(sketch, "E1765", {"start": v(-12.3, 10.52) * mm, "end": v(-12.23, 10.5) * mm});
            skLineSegment(sketch, "E1766", {"start": v(-12.23, 10.5) * mm, "end": v(-11.15, 10.33) * mm});
            skLineSegment(sketch, "E1767", {"start": v(-11.15, 10.33) * mm, "end": v(-11.08, 10.31) * mm});
            skLineSegment(sketch, "E1768", {"start": v(-11.08, 10.31) * mm, "end": v(-10.02, 10.02) * mm});
            skLineSegment(sketch, "E1769", {"start": v(-10.02, 10.02) * mm, "end": v(-9.95, 10) * mm});
            skLineSegment(sketch, "E1770", {"start": v(-9.95, 10) * mm, "end": v(-8.93, 9.58) * mm});
            skLineSegment(sketch, "E1771", {"start": v(-8.93, 9.58) * mm, "end": v(-8.9, 9.56) * mm});
            skLineSegment(sketch, "E1772", {"start": v(-8.9, 9.56) * mm, "end": v(-7.89, 9) * mm});
            skLineSegment(sketch, "E1773", {"start": v(-7.89, 9) * mm, "end": v(-7.84, 8.97) * mm});
            skLineSegment(sketch, "E1774", {"start": v(-7.84, 8.97) * mm, "end": v(-6.97, 8.33) * mm});
            skLineSegment(sketch, "E1775", {"start": v(-6.97, 8.33) * mm, "end": v(-6.93, 8.29) * mm});
            skLineSegment(sketch, "E1776", {"start": v(-6.93, 8.29) * mm, "end": v(-6.15, 7.55) * mm});
            skLineSegment(sketch, "E1777", {"start": v(-6.15, 7.55) * mm, "end": v(-6.12, 7.5) * mm});
            skLineSegment(sketch, "E1778", {"start": v(-6.12, 7.5) * mm, "end": v(-5.44, 6.69) * mm});
            skLineSegment(sketch, "E1779", {"start": v(-5.44, 6.69) * mm, "end": v(-5.4, 6.64) * mm});
            skLineSegment(sketch, "E1780", {"start": v(-5.4, 6.64) * mm, "end": v(-4.82, 5.75) * mm});
            skLineSegment(sketch, "E1781", {"start": v(-4.82, 5.75) * mm, "end": v(-4.8, 5.7) * mm});
            skLineSegment(sketch, "E1782", {"start": v(-4.8, 5.7) * mm, "end": v(-4.32, 4.74) * mm});
            skLineSegment(sketch, "E1783", {"start": v(-4.32, 4.74) * mm, "end": v(-4.3, 4.69) * mm});
            skLineSegment(sketch, "E1784", {"start": v(-4.3, 4.69) * mm, "end": v(-3.9, 3.67) * mm});
            skLineSegment(sketch, "E1785", {"start": v(-3.9, 3.67) * mm, "end": v(-3.89, 3.61) * mm});
            skLineSegment(sketch, "E1786", {"start": v(-3.89, 3.61) * mm, "end": v(-3.87, 3.56) * mm});
            skLineSegment(sketch, "E1787", {"start": v(-3.87, 3.56) * mm, "end": v(-3.6, 2.49) * mm});
            skLineSegment(sketch, "E1788", {"start": v(-3.6, 2.49) * mm, "end": v(-3.58, 2.4) * mm});
            skLineSegment(sketch, "E1789", {"start": v(-3.58, 2.4) * mm, "end": v(-3.4, 1.3) * mm});
            skLineSegment(sketch, "E1790", {"start": v(-3.4, 1.3) * mm, "end": v(-3.32, 0.16) * mm});
            skLineSegment(sketch, "E1791", {"start": v(-3.32, 0.16) * mm, "end": v(-3.31, 0.08) * mm});
            skLineSegment(sketch, "E1792", {"start": v(-3.31, 0.08) * mm, "end": v(-3.34, -1.09) * mm});
            skLineSegment(sketch, "E1793", {"start": v(-3.34, -1.09) * mm, "end": v(-3.34, -1.17) * mm});
            skLineSegment(sketch, "E1794", {"start": v(-3.34, -1.17) * mm, "end": v(-3.47, -2.35) * mm});
            skLineSegment(sketch, "E1795", {"start": v(-3.47, -2.35) * mm, "end": v(-3.48, -2.44) * mm});
            skLineSegment(sketch, "E1796", {"start": v(-3.48, -2.44) * mm, "end": v(-3.71, -3.62) * mm});
            skLineSegment(sketch, "E1797", {"start": v(-3.71, -3.62) * mm, "end": v(-3.73, -3.7) * mm});
            skLineSegment(sketch, "E1798", {"start": v(-3.73, -3.7) * mm, "end": v(-4.07, -4.9) * mm});
            skLineSegment(sketch, "E1799", {"start": v(-4.07, -4.9) * mm, "end": v(-4.1, -4.98) * mm});
            skLineSegment(sketch, "E1800", {"start": v(-4.1, -4.98) * mm, "end": v(-4.55, -6.16) * mm});
            skLineSegment(sketch, "E1801", {"start": v(-4.55, -6.16) * mm, "end": v(-4.59, -6.24) * mm});
            skLineSegment(sketch, "E1802", {"start": v(-4.59, -6.24) * mm, "end": v(-5.14, -7.4) * mm});
            skLineSegment(sketch, "E1803", {"start": v(-5.14, -7.4) * mm, "end": v(-5.17, -7.45) * mm});
            skLineSegment(sketch, "E1804", {"start": v(-5.17, -7.45) * mm, "end": v(-5.85, -8.61) * mm});
            skLineSegment(sketch, "E1805", {"start": v(-5.85, -8.61) * mm, "end": v(-5.9, -8.68) * mm});
            skLineSegment(sketch, "E1806", {"start": v(-5.9, -8.68) * mm, "end": v(-6.7, -9.75) * mm});
            skLineSegment(sketch, "E1807", {"start": v(-6.7, -9.75) * mm, "end": v(-6.74, -9.8) * mm});
            skLineSegment(sketch, "E1808", {"start": v(-6.74, -9.8) * mm, "end": v(-7.6, -10.79) * mm});
            skLineSegment(sketch, "E1809", {"start": v(-7.6, -10.79) * mm, "end": v(-7.66, -10.84) * mm});
            skLineSegment(sketch, "E1810", {"start": v(-7.66, -10.84) * mm, "end": v(-8.58, -11.72) * mm});
            skLineSegment(sketch, "E1811", {"start": v(-8.58, -11.72) * mm, "end": v(-8.64, -11.77) * mm});
            skLineSegment(sketch, "E1812", {"start": v(-8.64, -11.77) * mm, "end": v(-9.6, -12.56) * mm});
            skLineSegment(sketch, "E1813", {"start": v(-9.6, -12.56) * mm, "end": v(-9.67, -12.6) * mm});
            skLineSegment(sketch, "E1814", {"start": v(-9.67, -12.6) * mm, "end": v(-10.68, -13.3) * mm});
            skLineSegment(sketch, "E1815", {"start": v(-10.68, -13.3) * mm, "end": v(-10.74, -13.33) * mm});
            skLineSegment(sketch, "E1816", {"start": v(-10.74, -13.33) * mm, "end": v(-11.79, -13.91) * mm});
            skLineSegment(sketch, "E1817", {"start": v(-11.79, -13.91) * mm, "end": v(-11.85, -13.94) * mm});
            skLineSegment(sketch, "E1818", {"start": v(-11.85, -13.94) * mm, "end": v(-12.92, -14.42) * mm});
            skLineSegment(sketch, "E1819", {"start": v(-12.92, -14.42) * mm, "end": v(-12.99, -14.45) * mm});
            skLineSegment(sketch, "E1820", {"start": v(-12.99, -14.45) * mm, "end": v(-14.08, -14.82) * mm});
            skLineSegment(sketch, "E1821", {"start": v(-14.08, -14.82) * mm, "end": v(-14.15, -14.84) * mm});
            skLineSegment(sketch, "E1822", {"start": v(-14.15, -14.84) * mm, "end": v(-15.25, -15.1) * mm});
            skLineSegment(sketch, "E1823", {"start": v(-15.25, -15.1) * mm, "end": v(-15.32, -15.11) * mm});
            skLineSegment(sketch, "E1824", {"start": v(-15.32, -15.11) * mm, "end": v(-16.42, -15.27) * mm});
            skLineSegment(sketch, "E1825", {"start": v(-16.42, -15.27) * mm, "end": v(-16.5, -15.27) * mm});
            skLineSegment(sketch, "E1826", {"start": v(-16.5, -15.27) * mm, "end": v(-17.6, -15.3) * mm});
            skLineSegment(sketch, "E1827", {"start": v(-17.6, -15.3) * mm, "end": v(-17.66, -15.3) * mm});
            skLineSegment(sketch, "E1828", {"start": v(-17.66, -15.3) * mm, "end": v(-18.74, -15.22) * mm});
            skLineSegment(sketch, "E1829", {"start": v(-18.74, -15.22) * mm, "end": v(-18.81, -15.21) * mm});
            skLineSegment(sketch, "E1830", {"start": v(-18.81, -15.21) * mm, "end": v(-19.87, -15.01) * mm});
            skLineSegment(sketch, "E1831", {"start": v(-19.87, -15.01) * mm, "end": v(-19.94, -15) * mm});
            skLineSegment(sketch, "E1832", {"start": v(-19.94, -15) * mm, "end": v(-20.97, -14.67) * mm});
            skLineSegment(sketch, "E1833", {"start": v(-20.97, -14.67) * mm, "end": v(-21.03, -14.64) * mm});
            skLineSegment(sketch, "E1834", {"start": v(-21.03, -14.64) * mm, "end": v(-22.02, -14.2) * mm});
            skLineSegment(sketch, "E1835", {"start": v(-22.02, -14.2) * mm, "end": v(-22.05, -14.18) * mm});
            skLineSegment(sketch, "E1836", {"start": v(-22.05, -14.18) * mm, "end": v(-23.02, -13.59) * mm});
            skLineSegment(sketch, "E1837", {"start": v(-19.78, 14.22) * mm, "end": v(-21.47, 12.73) * mm});
            skLineSegment(sketch, "E1838", {"start": v(-21.47, 12.73) * mm, "end": v(-23.2, 11.3) * mm});
            skLineSegment(sketch, "E1839", {"start": v(-23.2, 11.3) * mm, "end": v(-23.31, 11.2) * mm});
            skLineSegment(sketch, "E1840", {"start": v(-23.31, 11.2) * mm, "end": v(-23.35, 11.17) * mm});
            skLineSegment(sketch, "E1841", {"start": v(-23.35, 11.17) * mm, "end": v(-25.06, 9.84) * mm});
            skLineSegment(sketch, "E1842", {"start": v(-25.06, 9.84) * mm, "end": v(-25.14, 9.78) * mm});
            skLineSegment(sketch, "E1843", {"start": v(-25.14, 9.78) * mm, "end": v(-25.97, 9.17) * mm});
            skLineSegment(sketch, "E1844", {"start": v(-25.97, 9.17) * mm, "end": v(-26.03, 9.12) * mm});
            skLineSegment(sketch, "E1845", {"start": v(-26.03, 9.12) * mm, "end": v(-26.83, 8.56) * mm});
            skLineSegment(sketch, "E1846", {"start": v(-26.83, 8.56) * mm, "end": v(-26.9, 8.52) * mm});
            skLineSegment(sketch, "E1847", {"start": v(-26.9, 8.52) * mm, "end": v(-27.66, 8) * mm});
            skLineSegment(sketch, "E1848", {"start": v(-27.66, 8) * mm, "end": v(-27.72, 7.97) * mm});
            skLineSegment(sketch, "E1849", {"start": v(-27.72, 7.97) * mm, "end": v(-28.44, 7.52) * mm});
            skLineSegment(sketch, "E1850", {"start": v(-28.44, 7.52) * mm, "end": v(-29.1, 7.15) * mm});
            skLineSegment(sketch, "E1851", {"start": v(-29.1, 7.15) * mm, "end": v(-29.16, 7.12) * mm});
            skLineSegment(sketch, "E1852", {"start": v(-29.16, 7.12) * mm, "end": v(-29.77, 6.81) * mm});
            skLineSegment(sketch, "E1853", {"start": v(-29.77, 6.81) * mm, "end": v(-29.82, 6.8) * mm});
            skLineSegment(sketch, "E1854", {"start": v(-29.82, 6.8) * mm, "end": v(-30.35, 6.57) * mm});
            skLineSegment(sketch, "E1855", {"start": v(-30.35, 6.57) * mm, "end": v(-30.38, 6.56) * mm});
            skLineSegment(sketch, "E1856", {"start": v(-30.38, 6.56) * mm, "end": v(-30.84, 6.43) * mm});
            skLineSegment(sketch, "E1857", {"start": v(-30.84, 6.43) * mm, "end": v(-30.85, 6.43) * mm});
            skLineSegment(sketch, "E1858", {"start": v(-30.85, 6.43) * mm, "end": v(-31.05, 6.4) * mm});
            skLineSegment(sketch, "E1859", {"start": v(-31.05, 6.4) * mm, "end": v(-31.07, 6.4) * mm});
            skLineSegment(sketch, "E1860", {"start": v(-31.07, 6.4) * mm, "end": v(-31.25, 6.4) * mm});
            skLineSegment(sketch, "E1861", {"start": v(-31.25, 6.4) * mm, "end": v(-31.25, 6.4) * mm});
            skLineSegment(sketch, "E1862", {"start": v(-31.25, 6.4) * mm, "end": v(-31.33, 6.4) * mm});
            skLineSegment(sketch, "E1863", {"start": v(-31.33, 6.4) * mm, "end": v(-31.34, 6.4) * mm});
            skLineSegment(sketch, "E1864", {"start": v(-31.34, 6.4) * mm, "end": v(-31.42, 6.41) * mm});
            skLineSegment(sketch, "E1865", {"start": v(-31.42, 6.41) * mm, "end": v(-31.42, 6.42) * mm});
            skLineSegment(sketch, "E1866", {"start": v(-31.42, 6.42) * mm, "end": v(-31.5, 6.44) * mm});
            skLineSegment(sketch, "E1867", {"start": v(-31.5, 6.44) * mm, "end": v(-31.5, 6.44) * mm});
            skLineSegment(sketch, "E1868", {"start": v(-31.5, 6.44) * mm, "end": v(-31.56, 6.47) * mm});
            skLineSegment(sketch, "E1869", {"start": v(-31.56, 6.47) * mm, "end": v(-31.61, 6.5) * mm});
            skLineSegment(sketch, "E1870", {"start": v(-31.61, 6.5) * mm, "end": v(-31.62, 6.5) * mm});
            skLineSegment(sketch, "E1871", {"start": v(-31.62, 6.5) * mm, "end": v(-31.67, 6.54) * mm});
            skLineSegment(sketch, "E1872", {"start": v(-31.67, 6.54) * mm, "end": v(-31.67, 6.55) * mm});
            skLineSegment(sketch, "E1873", {"start": v(-31.67, 6.55) * mm, "end": v(-31.71, 6.6) * mm});
            skLineSegment(sketch, "E1874", {"start": v(-31.71, 6.6) * mm, "end": v(-31.72, 6.6) * mm});
            skLineSegment(sketch, "E1875", {"start": v(-31.72, 6.6) * mm, "end": v(-31.75, 6.66) * mm});
            skLineSegment(sketch, "E1876", {"start": v(-31.75, 6.66) * mm, "end": v(-31.78, 6.72) * mm});
            skLineSegment(sketch, "E1877", {"start": v(-31.78, 6.72) * mm, "end": v(-31.78, 6.73) * mm});
            skLineSegment(sketch, "E1878", {"start": v(-31.78, 6.73) * mm, "end": v(-31.8, 6.8) * mm});
            skLineSegment(sketch, "E1879", {"start": v(-31.8, 6.8) * mm, "end": v(-31.8, 6.8) * mm});
            skLineSegment(sketch, "E1880", {"start": v(-31.8, 6.8) * mm, "end": v(-31.82, 6.88) * mm});
            skLineSegment(sketch, "E1881", {"start": v(-31.82, 6.88) * mm, "end": v(-31.82, 6.88) * mm});
            skLineSegment(sketch, "E1882", {"start": v(-31.82, 6.88) * mm, "end": v(-31.83, 6.97) * mm});
            skLineSegment(sketch, "E1883", {"start": v(-31.83, 6.97) * mm, "end": v(-31.83, 7.09) * mm});
            skLineSegment(sketch, "E1884", {"start": v(-31.83, 7.09) * mm, "end": v(-31.78, 8.9) * mm});
            skLineSegment(sketch, "E1885", {"start": v(-31.78, 8.9) * mm, "end": v(-31.77, 9.01) * mm});
            skLineSegment(sketch, "E1886", {"start": v(-31.77, 9.01) * mm, "end": v(-31.54, 10.73) * mm});
            skLineSegment(sketch, "E1887", {"start": v(-31.54, 10.73) * mm, "end": v(-31.51, 10.82) * mm});
            skLineSegment(sketch, "E1888", {"start": v(-31.51, 10.82) * mm, "end": v(-31.12, 12.42) * mm});
            skLineSegment(sketch, "E1889", {"start": v(-31.12, 12.42) * mm, "end": v(-31.09, 12.52) * mm});
            skLineSegment(sketch, "E1890", {"start": v(-31.09, 12.52) * mm, "end": v(-30.54, 14) * mm});
            skLineSegment(sketch, "E1891", {"start": v(-30.54, 14) * mm, "end": v(-30.5, 14.08) * mm});
            skLineSegment(sketch, "E1892", {"start": v(-30.5, 14.08) * mm, "end": v(-29.8, 15.45) * mm});
            skLineSegment(sketch, "E1893", {"start": v(-29.8, 15.45) * mm, "end": v(-29.75, 15.53) * mm});
            skLineSegment(sketch, "E1894", {"start": v(-29.75, 15.53) * mm, "end": v(-28.9, 16.77) * mm});
            skLineSegment(sketch, "E1895", {"start": v(-28.9, 16.77) * mm, "end": v(-28.85, 16.84) * mm});
            skLineSegment(sketch, "E1896", {"start": v(-28.85, 16.84) * mm, "end": v(-27.88, 17.95) * mm});
            skLineSegment(sketch, "E1897", {"start": v(-27.88, 17.95) * mm, "end": v(-27.82, 18.01) * mm});
            skLineSegment(sketch, "E1898", {"start": v(-27.82, 18.01) * mm, "end": v(-26.73, 19) * mm});
            skLineSegment(sketch, "E1899", {"start": v(-26.73, 19) * mm, "end": v(-26.65, 19.05) * mm});
            skLineSegment(sketch, "E1900", {"start": v(-26.65, 19.05) * mm, "end": v(-25.45, 19.9) * mm});
            skLineSegment(sketch, "E1901", {"start": v(-25.45, 19.9) * mm, "end": v(-25.37, 19.95) * mm});
            skLineSegment(sketch, "E1902", {"start": v(-25.37, 19.95) * mm, "end": v(-24.07, 20.66) * mm});
            skLineSegment(sketch, "E1903", {"start": v(-24.07, 20.66) * mm, "end": v(-23.98, 20.7) * mm});
            skLineSegment(sketch, "E1904", {"start": v(-23.98, 20.7) * mm, "end": v(-22.58, 21.26) * mm});
            skLineSegment(sketch, "E1905", {"start": v(-22.58, 21.26) * mm, "end": v(-22.49, 21.29) * mm});
            skLineSegment(sketch, "E1906", {"start": v(-22.49, 21.29) * mm, "end": v(-21, 21.71) * mm});
            skLineSegment(sketch, "E1907", {"start": v(-21, 21.71) * mm, "end": v(-20.9, 21.73) * mm});
            skLineSegment(sketch, "E1908", {"start": v(-20.9, 21.73) * mm, "end": v(-19.35, 22) * mm});
            skLineSegment(sketch, "E1909", {"start": v(-19.35, 22) * mm, "end": v(-19.24, 22.01) * mm});
            skLineSegment(sketch, "E1910", {"start": v(-19.24, 22.01) * mm, "end": v(-17.62, 22.13) * mm});
            skLineSegment(sketch, "E1911", {"start": v(-17.62, 22.13) * mm, "end": v(-17.51, 22.13) * mm});
            skLineSegment(sketch, "E1912", {"start": v(-17.51, 22.13) * mm, "end": v(-15.83, 22.1) * mm});
            skLineSegment(sketch, "E1913", {"start": v(-15.83, 22.1) * mm, "end": v(-14.1, 21.9) * mm});
            skLineSegment(sketch, "E1914", {"start": v(-14.1, 21.9) * mm, "end": v(-13.99, 21.88) * mm});
            skLineSegment(sketch, "E1915", {"start": v(-13.99, 21.88) * mm, "end": v(-13.98, 21.88) * mm});
            skLineSegment(sketch, "E1916", {"start": v(-13.98, 21.88) * mm, "end": v(-13.98, 21.88) * mm});
            skLineSegment(sketch, "E1917", {"start": v(-13.98, 21.88) * mm, "end": v(-13.9, 21.87) * mm});
            skLineSegment(sketch, "E1918", {"start": v(-13.9, 21.87) * mm, "end": v(-13.84, 21.85) * mm});
            skLineSegment(sketch, "E1919", {"start": v(-13.84, 21.85) * mm, "end": v(-13.83, 21.85) * mm});
            skLineSegment(sketch, "E1920", {"start": v(-13.83, 21.85) * mm, "end": v(-13.77, 21.82) * mm});
            skLineSegment(sketch, "E1921", {"start": v(-13.77, 21.82) * mm, "end": v(-13.77, 21.82) * mm});
            skLineSegment(sketch, "E1922", {"start": v(-13.77, 21.82) * mm, "end": v(-13.72, 21.79) * mm});
            skLineSegment(sketch, "E1923", {"start": v(-13.72, 21.79) * mm, "end": v(-13.68, 21.75) * mm});
            skLineSegment(sketch, "E1924", {"start": v(-13.68, 21.75) * mm, "end": v(-13.67, 21.75) * mm});
            skLineSegment(sketch, "E1925", {"start": v(-13.67, 21.75) * mm, "end": v(-13.66, 21.73) * mm});
            skLineSegment(sketch, "E1926", {"start": v(-13.66, 21.73) * mm, "end": v(-13.64, 21.7) * mm});
            skLineSegment(sketch, "E1927", {"start": v(-13.64, 21.7) * mm, "end": v(-13.64, 21.7) * mm});
            skLineSegment(sketch, "E1928", {"start": v(-13.64, 21.7) * mm, "end": v(-13.61, 21.65) * mm});
            skLineSegment(sketch, "E1929", {"start": v(-13.61, 21.65) * mm, "end": v(-13.6, 21.65) * mm});
            skLineSegment(sketch, "E1930", {"start": v(-13.6, 21.65) * mm, "end": v(-13.59, 21.6) * mm});
            skLineSegment(sketch, "E1931", {"start": v(-13.59, 21.6) * mm, "end": v(-13.58, 21.54) * mm});
            skLineSegment(sketch, "E1932", {"start": v(-13.58, 21.54) * mm, "end": v(-13.58, 21.53) * mm});
            skLineSegment(sketch, "E1933", {"start": v(-13.58, 21.53) * mm, "end": v(-13.57, 21.47) * mm});
            skLineSegment(sketch, "E1934", {"start": v(-13.57, 21.47) * mm, "end": v(-13.57, 21.46) * mm});
            skLineSegment(sketch, "E1935", {"start": v(-13.57, 21.46) * mm, "end": v(-13.58, 21.4) * mm});
            skLineSegment(sketch, "E1936", {"start": v(-13.58, 21.4) * mm, "end": v(-13.58, 21.39) * mm});
            skLineSegment(sketch, "E1937", {"start": v(-13.58, 21.39) * mm, "end": v(-13.59, 21.31) * mm});
            skLineSegment(sketch, "E1938", {"start": v(-13.59, 21.31) * mm, "end": v(-13.59, 21.3) * mm});
            skLineSegment(sketch, "E1939", {"start": v(-13.59, 21.3) * mm, "end": v(-13.63, 21.14) * mm});
            skLineSegment(sketch, "E1940", {"start": v(-13.63, 21.14) * mm, "end": v(-13.64, 21.13) * mm});
            skLineSegment(sketch, "E1941", {"start": v(-13.64, 21.13) * mm, "end": v(-13.7, 20.94) * mm});
            skLineSegment(sketch, "E1942", {"start": v(-13.7, 20.94) * mm, "end": v(-13.71, 20.93) * mm});
            skLineSegment(sketch, "E1943", {"start": v(-13.71, 20.93) * mm, "end": v(-13.93, 20.51) * mm});
            skLineSegment(sketch, "E1944", {"start": v(-13.93, 20.51) * mm, "end": v(-13.94, 20.5) * mm});
            skLineSegment(sketch, "E1945", {"start": v(-13.94, 20.5) * mm, "end": v(-14.26, 20.01) * mm});
            skLineSegment(sketch, "E1946", {"start": v(-14.26, 20.01) * mm, "end": v(-14.29, 19.97) * mm});
            skLineSegment(sketch, "E1947", {"start": v(-14.29, 19.97) * mm, "end": v(-14.7, 19.43) * mm});
            skLineSegment(sketch, "E1948", {"start": v(-14.7, 19.43) * mm, "end": v(-14.73, 19.38) * mm});
            skLineSegment(sketch, "E1949", {"start": v(-14.73, 19.38) * mm, "end": v(-15.22, 18.79) * mm});
            skLineSegment(sketch, "E1950", {"start": v(-15.22, 18.79) * mm, "end": v(-15.78, 18.16) * mm});
            skLineSegment(sketch, "E1951", {"start": v(-15.78, 18.16) * mm, "end": v(-15.83, 18.1) * mm});
            skLineSegment(sketch, "E1952", {"start": v(-15.83, 18.1) * mm, "end": v(-16.45, 17.43) * mm});
            skLineSegment(sketch, "E1953", {"start": v(-16.45, 17.43) * mm, "end": v(-16.5, 17.38) * mm});
            skLineSegment(sketch, "E1954", {"start": v(-16.5, 17.38) * mm, "end": v(-17.2, 16.68) * mm});
            skLineSegment(sketch, "E1955", {"start": v(-17.2, 16.68) * mm, "end": v(-17.25, 16.62) * mm});
            skLineSegment(sketch, "E1956", {"start": v(-17.25, 16.62) * mm, "end": v(-17.99, 15.9) * mm});
            skLineSegment(sketch, "E1957", {"start": v(-17.99, 15.9) * mm, "end": v(-18.05, 15.83) * mm});
            skLineSegment(sketch, "E1958", {"start": v(-18.05, 15.83) * mm, "end": v(-19.64, 14.35) * mm});
            skLineSegment(sketch, "E1959", {"start": v(-19.64, 14.35) * mm, "end": v(-19.67, 14.32) * mm});
            skLineSegment(sketch, "E1960", {"start": v(-19.67, 14.32) * mm, "end": v(-19.78, 14.22) * mm});
            skLineSegment(sketch, "E1961", {"start": v(17.41, 15.9) * mm, "end": v(19, 14.4) * mm});
            skLineSegment(sketch, "E1962", {"start": v(19, 14.4) * mm, "end": v(19.04, 14.38) * mm});
            skLineSegment(sketch, "E1963", {"start": v(19.04, 14.38) * mm, "end": v(19.14, 14.28) * mm});
            skLineSegment(sketch, "E1964", {"start": v(19.14, 14.28) * mm, "end": v(20.83, 12.79) * mm});
            skLineSegment(sketch, "E1965", {"start": v(20.83, 12.79) * mm, "end": v(22.57, 11.35) * mm});
            skLineSegment(sketch, "E1966", {"start": v(22.57, 11.35) * mm, "end": v(22.68, 11.26) * mm});
            skLineSegment(sketch, "E1967", {"start": v(22.68, 11.26) * mm, "end": v(22.71, 11.23) * mm});
            skLineSegment(sketch, "E1968", {"start": v(22.71, 11.23) * mm, "end": v(24.43, 9.9) * mm});
            skLineSegment(sketch, "E1969", {"start": v(24.43, 9.9) * mm, "end": v(24.5, 9.85) * mm});
            skLineSegment(sketch, "E1970", {"start": v(24.5, 9.85) * mm, "end": v(25.33, 9.25) * mm});
            skLineSegment(sketch, "E1971", {"start": v(25.33, 9.25) * mm, "end": v(25.4, 9.2) * mm});
            skLineSegment(sketch, "E1972", {"start": v(25.4, 9.2) * mm, "end": v(26.2, 8.64) * mm});
            skLineSegment(sketch, "E1973", {"start": v(26.2, 8.64) * mm, "end": v(26.26, 8.6) * mm});
            skLineSegment(sketch, "E1974", {"start": v(26.26, 8.6) * mm, "end": v(27.03, 8.1) * mm});
            skLineSegment(sketch, "E1975", {"start": v(27.03, 8.1) * mm, "end": v(27.08, 8.06) * mm});
            skLineSegment(sketch, "E1976", {"start": v(27.08, 8.06) * mm, "end": v(27.8, 7.62) * mm});
            skLineSegment(sketch, "E1977", {"start": v(27.8, 7.62) * mm, "end": v(28.47, 7.25) * mm});
            skLineSegment(sketch, "E1978", {"start": v(28.47, 7.25) * mm, "end": v(28.53, 7.23) * mm});
            skLineSegment(sketch, "E1979", {"start": v(28.53, 7.23) * mm, "end": v(29.13, 6.93) * mm});
            skLineSegment(sketch, "E1980", {"start": v(29.13, 6.93) * mm, "end": v(29.18, 6.91) * mm});
            skLineSegment(sketch, "E1981", {"start": v(29.18, 6.91) * mm, "end": v(29.72, 6.7) * mm});
            skLineSegment(sketch, "E1982", {"start": v(29.72, 6.7) * mm, "end": v(29.74, 6.7) * mm});
            skLineSegment(sketch, "E1983", {"start": v(29.74, 6.7) * mm, "end": v(30.2, 6.58) * mm});
            skLineSegment(sketch, "E1984", {"start": v(30.2, 6.58) * mm, "end": v(30.22, 6.58) * mm});
            skLineSegment(sketch, "E1985", {"start": v(30.22, 6.58) * mm, "end": v(30.42, 6.56) * mm});
            skLineSegment(sketch, "E1986", {"start": v(30.42, 6.56) * mm, "end": v(30.43, 6.56) * mm});
            skLineSegment(sketch, "E1987", {"start": v(30.43, 6.56) * mm, "end": v(30.61, 6.56) * mm});
            skLineSegment(sketch, "E1988", {"start": v(30.61, 6.56) * mm, "end": v(30.62, 6.56) * mm});
            skLineSegment(sketch, "E1989", {"start": v(30.62, 6.56) * mm, "end": v(30.7, 6.57) * mm});
            skLineSegment(sketch, "E1990", {"start": v(30.7, 6.57) * mm, "end": v(30.7, 6.57) * mm});
            skLineSegment(sketch, "E1991", {"start": v(30.7, 6.57) * mm, "end": v(30.78, 6.59) * mm});
            skLineSegment(sketch, "E1992", {"start": v(30.78, 6.59) * mm, "end": v(30.78, 6.6) * mm});
            skLineSegment(sketch, "E1993", {"start": v(30.78, 6.6) * mm, "end": v(30.85, 6.62) * mm});
            skLineSegment(sketch, "E1994", {"start": v(30.85, 6.62) * mm, "end": v(30.86, 6.62) * mm});
            skLineSegment(sketch, "E1995", {"start": v(30.86, 6.62) * mm, "end": v(30.92, 6.65) * mm});
            skLineSegment(sketch, "E1996", {"start": v(30.92, 6.65) * mm, "end": v(30.98, 6.69) * mm});
            skLineSegment(sketch, "E1997", {"start": v(30.98, 6.69) * mm, "end": v(30.98, 6.7) * mm});
            skLineSegment(sketch, "E1998", {"start": v(30.98, 6.7) * mm, "end": v(31.03, 6.74) * mm});
            skLineSegment(sketch, "E1999", {"start": v(31.03, 6.74) * mm, "end": v(31.03, 6.74) * mm});
            skLineSegment(sketch, "E2000", {"start": v(31.03, 6.74) * mm, "end": v(31.08, 6.8) * mm});
            skLineSegment(sketch, "E2001", {"start": v(31.08, 6.8) * mm, "end": v(31.08, 6.8) * mm});
            skLineSegment(sketch, "E2002", {"start": v(31.08, 6.8) * mm, "end": v(31.12, 6.86) * mm});
            skLineSegment(sketch, "E2003", {"start": v(31.12, 6.86) * mm, "end": v(31.15, 6.93) * mm});
            skLineSegment(sketch, "E2004", {"start": v(31.15, 6.93) * mm, "end": v(31.15, 6.93) * mm});
            skLineSegment(sketch, "E2005", {"start": v(31.15, 6.93) * mm, "end": v(31.17, 7) * mm});
            skLineSegment(sketch, "E2006", {"start": v(31.17, 7) * mm, "end": v(31.19, 7.1) * mm});
            skLineSegment(sketch, "E2007", {"start": v(31.19, 7.1) * mm, "end": v(31.2, 7.2) * mm});
            skLineSegment(sketch, "E2008", {"start": v(31.2, 7.2) * mm, "end": v(31.2, 7.2) * mm});
            skLineSegment(sketch, "E2009", {"start": v(31.2, 7.2) * mm, "end": v(31.21, 8.17) * mm});
            skLineSegment(sketch, "E2010", {"start": v(31.21, 8.17) * mm, "end": v(31.21, 8.25) * mm});
            skLineSegment(sketch, "E2011", {"start": v(31.21, 8.25) * mm, "end": v(31.18, 9.17) * mm});
            skLineSegment(sketch, "E2012", {"start": v(31.18, 9.17) * mm, "end": v(31.1, 10.05) * mm});
            skLineSegment(sketch, "E2013", {"start": v(31.1, 10.05) * mm, "end": v(31.1, 10.16) * mm});
            skLineSegment(sketch, "E2014", {"start": v(31.1, 10.16) * mm, "end": v(30.97, 11.01) * mm});
            skLineSegment(sketch, "E2015", {"start": v(30.97, 11.01) * mm, "end": v(30.95, 11.11) * mm});
            skLineSegment(sketch, "E2016", {"start": v(30.95, 11.11) * mm, "end": v(30.58, 12.74) * mm});
            skLineSegment(sketch, "E2017", {"start": v(30.58, 12.74) * mm, "end": v(30.55, 12.83) * mm});
            skLineSegment(sketch, "E2018", {"start": v(30.55, 12.83) * mm, "end": v(30, 14.34) * mm});
            skLineSegment(sketch, "E2019", {"start": v(30, 14.34) * mm, "end": v(29.97, 14.42) * mm});
            skLineSegment(sketch, "E2020", {"start": v(29.97, 14.42) * mm, "end": v(29.27, 15.8) * mm});
            skLineSegment(sketch, "E2021", {"start": v(29.27, 15.8) * mm, "end": v(29.23, 15.88) * mm});
            skLineSegment(sketch, "E2022", {"start": v(29.23, 15.88) * mm, "end": v(28.39, 17.13) * mm});
            skLineSegment(sketch, "E2023", {"start": v(28.39, 17.13) * mm, "end": v(28.33, 17.2) * mm});
            skLineSegment(sketch, "E2024", {"start": v(28.33, 17.2) * mm, "end": v(27.36, 18.32) * mm});
            skLineSegment(sketch, "E2025", {"start": v(27.36, 18.32) * mm, "end": v(27.3, 18.38) * mm});
            skLineSegment(sketch, "E2026", {"start": v(27.3, 18.38) * mm, "end": v(26.2, 19.37) * mm});
            skLineSegment(sketch, "E2027", {"start": v(26.2, 19.37) * mm, "end": v(26.13, 19.43) * mm});
            skLineSegment(sketch, "E2028", {"start": v(26.13, 19.43) * mm, "end": v(24.91, 20.28) * mm});
            skLineSegment(sketch, "E2029", {"start": v(24.91, 20.28) * mm, "end": v(24.83, 20.32) * mm});
            skLineSegment(sketch, "E2030", {"start": v(24.83, 20.32) * mm, "end": v(23.51, 21.03) * mm});
            skLineSegment(sketch, "E2031", {"start": v(23.51, 21.03) * mm, "end": v(23.42, 21.07) * mm});
            skLineSegment(sketch, "E2032", {"start": v(23.42, 21.07) * mm, "end": v(22.01, 21.62) * mm});
            skLineSegment(sketch, "E2033", {"start": v(22.01, 21.62) * mm, "end": v(21.91, 21.65) * mm});
            skLineSegment(sketch, "E2034", {"start": v(21.91, 21.65) * mm, "end": v(20.42, 22.06) * mm});
            skLineSegment(sketch, "E2035", {"start": v(20.42, 22.06) * mm, "end": v(20.32, 22.08) * mm});
            skLineSegment(sketch, "E2036", {"start": v(20.32, 22.08) * mm, "end": v(18.74, 22.33) * mm});
            skLineSegment(sketch, "E2037", {"start": v(18.74, 22.33) * mm, "end": v(18.64, 22.34) * mm});
            skLineSegment(sketch, "E2038", {"start": v(18.64, 22.34) * mm, "end": v(17, 22.43) * mm});
            skLineSegment(sketch, "E2039", {"start": v(17, 22.43) * mm, "end": v(16.9, 22.42) * mm});
            skLineSegment(sketch, "E2040", {"start": v(16.9, 22.42) * mm, "end": v(15.2, 22.36) * mm});
            skLineSegment(sketch, "E2041", {"start": v(15.2, 22.36) * mm, "end": v(13.46, 22.12) * mm});
            skLineSegment(sketch, "E2042", {"start": v(13.46, 22.12) * mm, "end": v(13.4, 22.11) * mm});
            skLineSegment(sketch, "E2043", {"start": v(13.4, 22.11) * mm, "end": v(13.35, 22.1) * mm});
            skLineSegment(sketch, "E2044", {"start": v(13.35, 22.1) * mm, "end": v(13.27, 22.09) * mm});
            skLineSegment(sketch, "E2045", {"start": v(13.27, 22.09) * mm, "end": v(13.27, 22.09) * mm});
            skLineSegment(sketch, "E2046", {"start": v(13.27, 22.09) * mm, "end": v(13.2, 22.06) * mm});
            skLineSegment(sketch, "E2047", {"start": v(13.2, 22.06) * mm, "end": v(13.2, 22.06) * mm});
            skLineSegment(sketch, "E2048", {"start": v(13.2, 22.06) * mm, "end": v(13.14, 22.03) * mm});
            skLineSegment(sketch, "E2049", {"start": v(13.14, 22.03) * mm, "end": v(13.13, 22.03) * mm});
            skLineSegment(sketch, "E2050", {"start": v(13.13, 22.03) * mm, "end": v(13.08, 22) * mm});
            skLineSegment(sketch, "E2051", {"start": v(13.08, 22) * mm, "end": v(13.04, 21.95) * mm});
            skLineSegment(sketch, "E2052", {"start": v(13.04, 21.95) * mm, "end": v(13.04, 21.95) * mm});
            skLineSegment(sketch, "E2053", {"start": v(13.04, 21.95) * mm, "end": v(13, 21.9) * mm});
            skLineSegment(sketch, "E2054", {"start": v(13, 21.9) * mm, "end": v(13, 21.9) * mm});
            skLineSegment(sketch, "E2055", {"start": v(13, 21.9) * mm, "end": v(12.97, 21.84) * mm});
            skLineSegment(sketch, "E2056", {"start": v(12.97, 21.84) * mm, "end": v(12.97, 21.84) * mm});
            skLineSegment(sketch, "E2057", {"start": v(12.97, 21.84) * mm, "end": v(12.95, 21.78) * mm});
            skLineSegment(sketch, "E2058", {"start": v(12.95, 21.78) * mm, "end": v(12.94, 21.72) * mm});
            skLineSegment(sketch, "E2059", {"start": v(12.94, 21.72) * mm, "end": v(12.94, 21.71) * mm});
            skLineSegment(sketch, "E2060", {"start": v(12.94, 21.71) * mm, "end": v(12.94, 21.64) * mm});
            skLineSegment(sketch, "E2061", {"start": v(12.94, 21.64) * mm, "end": v(12.94, 21.64) * mm});
            skLineSegment(sketch, "E2062", {"start": v(12.94, 21.64) * mm, "end": v(12.94, 21.56) * mm});
            skLineSegment(sketch, "E2063", {"start": v(12.94, 21.56) * mm, "end": v(12.94, 21.56) * mm});
            skLineSegment(sketch, "E2064", {"start": v(12.94, 21.56) * mm, "end": v(12.95, 21.48) * mm});
            skLineSegment(sketch, "E2065", {"start": v(12.95, 21.48) * mm, "end": v(12.95, 21.47) * mm});
            skLineSegment(sketch, "E2066", {"start": v(12.95, 21.47) * mm, "end": v(13, 21.3) * mm});
            skLineSegment(sketch, "E2067", {"start": v(13, 21.3) * mm, "end": v(13, 21.28) * mm});
            skLineSegment(sketch, "E2068", {"start": v(13, 21.28) * mm, "end": v(13.07, 21.1) * mm});
            skLineSegment(sketch, "E2069", {"start": v(13.07, 21.1) * mm, "end": v(13.29, 20.66) * mm});
            skLineSegment(sketch, "E2070", {"start": v(13.29, 20.66) * mm, "end": v(13.3, 20.63) * mm});
            skLineSegment(sketch, "E2071", {"start": v(13.3, 20.63) * mm, "end": v(13.62, 20.13) * mm});
            skLineSegment(sketch, "E2072", {"start": v(13.62, 20.13) * mm, "end": v(13.65, 20.09) * mm});
            skLineSegment(sketch, "E2073", {"start": v(13.65, 20.09) * mm, "end": v(14.06, 19.54) * mm});
            skLineSegment(sketch, "E2074", {"start": v(14.06, 19.54) * mm, "end": v(14.1, 19.49) * mm});
            skLineSegment(sketch, "E2075", {"start": v(14.1, 19.49) * mm, "end": v(14.58, 18.89) * mm});
            skLineSegment(sketch, "E2076", {"start": v(14.58, 18.89) * mm, "end": v(15.14, 18.25) * mm});
            skLineSegment(sketch, "E2077", {"start": v(15.14, 18.25) * mm, "end": v(15.19, 18.2) * mm});
            skLineSegment(sketch, "E2078", {"start": v(15.19, 18.2) * mm, "end": v(15.82, 17.51) * mm});
            skLineSegment(sketch, "E2079", {"start": v(15.82, 17.51) * mm, "end": v(15.87, 17.46) * mm});
            skLineSegment(sketch, "E2080", {"start": v(15.87, 17.46) * mm, "end": v(16.55, 16.75) * mm});
            skLineSegment(sketch, "E2081", {"start": v(16.55, 16.75) * mm, "end": v(16.61, 16.69) * mm});
            skLineSegment(sketch, "E2082", {"start": v(16.61, 16.69) * mm, "end": v(17.35, 15.96) * mm});
            skLineSegment(sketch, "E2083", {"start": v(17.35, 15.96) * mm, "end": v(17.41, 15.9) * mm});
            skLineSegment(sketch, "E2084", {"start": v(-13.3, -44.97) * mm, "end": v(-13.27, -44.76) * mm});
            skLineSegment(sketch, "E2085", {"start": v(-13.27, -44.76) * mm, "end": v(-13.2, -44.53) * mm});
            skLineSegment(sketch, "E2086", {"start": v(-13.2, -44.53) * mm, "end": v(-13.2, -44.52) * mm});
            skLineSegment(sketch, "E2087", {"start": v(-13.2, -44.52) * mm, "end": v(-13.19, -44.51) * mm});
            skLineSegment(sketch, "E2088", {"start": v(-13.19, -44.51) * mm, "end": v(-13.08, -44.3) * mm});
            skLineSegment(sketch, "E2089", {"start": v(-13.08, -44.3) * mm, "end": v(-13.07, -44.29) * mm});
            skLineSegment(sketch, "E2090", {"start": v(-13.07, -44.29) * mm, "end": v(-12.93, -44.08) * mm});
            skLineSegment(sketch, "E2091", {"start": v(-12.93, -44.08) * mm, "end": v(-12.77, -43.88) * mm});
            skLineSegment(sketch, "E2092", {"start": v(-12.77, -43.88) * mm, "end": v(-12.75, -43.87) * mm});
            skLineSegment(sketch, "E2093", {"start": v(-12.75, -43.87) * mm, "end": v(-12.55, -43.67) * mm});
            skLineSegment(sketch, "E2094", {"start": v(-12.55, -43.67) * mm, "end": v(-12.54, -43.65) * mm});
            skLineSegment(sketch, "E2095", {"start": v(-12.54, -43.65) * mm, "end": v(-12.06, -43.28) * mm});
            skLineSegment(sketch, "E2096", {"start": v(-12.06, -43.28) * mm, "end": v(-12.04, -43.26) * mm});
            skLineSegment(sketch, "E2097", {"start": v(-12.04, -43.26) * mm, "end": v(-11.46, -42.91) * mm});
            skLineSegment(sketch, "E2098", {"start": v(-11.46, -42.91) * mm, "end": v(-11.41, -42.88) * mm});
            skLineSegment(sketch, "E2099", {"start": v(-11.41, -42.88) * mm, "end": v(-10.74, -42.55) * mm});
            skLineSegment(sketch, "E2100", {"start": v(-10.74, -42.55) * mm, "end": v(-10.69, -42.53) * mm});
            skLineSegment(sketch, "E2101", {"start": v(-10.69, -42.53) * mm, "end": v(-9.94, -42.23) * mm});
            skLineSegment(sketch, "E2102", {"start": v(-9.94, -42.23) * mm, "end": v(-9.88, -42.2) * mm});
            skLineSegment(sketch, "E2103", {"start": v(-9.88, -42.2) * mm, "end": v(-9.07, -41.93) * mm});
            skLineSegment(sketch, "E2104", {"start": v(-9.07, -41.93) * mm, "end": v(-8.2, -41.69) * mm});
            skLineSegment(sketch, "E2105", {"start": v(-8.2, -41.69) * mm, "end": v(-8.14, -41.67) * mm});
            skLineSegment(sketch, "E2106", {"start": v(-8.14, -41.67) * mm, "end": v(-7.23, -41.45) * mm});
            skLineSegment(sketch, "E2107", {"start": v(-7.23, -41.45) * mm, "end": v(-7.15, -41.44) * mm});
            skLineSegment(sketch, "E2108", {"start": v(-7.15, -41.44) * mm, "end": v(-5.25, -41.12) * mm});
            skLineSegment(sketch, "E2109", {"start": v(-5.25, -41.12) * mm, "end": v(-5.17, -41.1) * mm});
            skLineSegment(sketch, "E2110", {"start": v(-5.17, -41.1) * mm, "end": v(-5.1, -41.1) * mm});
            skLineSegment(sketch, "E2111", {"start": v(-5.1, -41.1) * mm, "end": v(-3.15, -40.93) * mm});
            skLineSegment(sketch, "E2112", {"start": v(-3.15, -40.93) * mm, "end": v(-3.08, -40.92) * mm});
            skLineSegment(sketch, "E2113", {"start": v(-3.08, -40.92) * mm, "end": v(-1.19, -40.91) * mm});
            skLineSegment(sketch, "E2114", {"start": v(-1.19, -40.91) * mm, "end": v(-1.08, -40.91) * mm});
            skLineSegment(sketch, "E2115", {"start": v(-1.08, -40.91) * mm, "end": v(-0.1, -40.9) * mm});
            skLineSegment(sketch, "E2116", {"start": v(-0.1, -40.9) * mm, "end": v(-0.07, -40.9) * mm});
            skLineSegment(sketch, "E2117", {"start": v(-0.07, -40.9) * mm, "end": v(0.91, -40.94) * mm});
            skLineSegment(sketch, "E2118", {"start": v(0.91, -40.94) * mm, "end": v(1.02, -40.95) * mm});
            skLineSegment(sketch, "E2119", {"start": v(1.02, -40.95) * mm, "end": v(3.05, -41.17) * mm});
            skLineSegment(sketch, "E2120", {"start": v(3.05, -41.17) * mm, "end": v(3.16, -41.19) * mm});
            skLineSegment(sketch, "E2121", {"start": v(3.16, -41.19) * mm, "end": v(5.19, -41.59) * mm});
            skLineSegment(sketch, "E2122", {"start": v(5.19, -41.59) * mm, "end": v(5.29, -41.61) * mm});
            skLineSegment(sketch, "E2123", {"start": v(5.29, -41.61) * mm, "end": v(6.27, -41.87) * mm});
            skLineSegment(sketch, "E2124", {"start": v(6.27, -41.87) * mm, "end": v(6.33, -41.89) * mm});
            skLineSegment(sketch, "E2125", {"start": v(6.33, -41.89) * mm, "end": v(7.27, -42.18) * mm});
            skLineSegment(sketch, "E2126", {"start": v(7.27, -42.18) * mm, "end": v(7.33, -42.2) * mm});
            skLineSegment(sketch, "E2127", {"start": v(7.33, -42.2) * mm, "end": v(8.2, -42.53) * mm});
            skLineSegment(sketch, "E2128", {"start": v(8.2, -42.53) * mm, "end": v(9.01, -42.89) * mm});
            skLineSegment(sketch, "E2129", {"start": v(9.01, -42.89) * mm, "end": v(9.07, -42.91) * mm});
            skLineSegment(sketch, "E2130", {"start": v(9.07, -42.91) * mm, "end": v(9.8, -43.3) * mm});
            skLineSegment(sketch, "E2131", {"start": v(9.8, -43.3) * mm, "end": v(9.84, -43.32) * mm});
            skLineSegment(sketch, "E2132", {"start": v(9.84, -43.32) * mm, "end": v(10.46, -43.73) * mm});
            skLineSegment(sketch, "E2133", {"start": v(10.46, -43.73) * mm, "end": v(10.5, -43.76) * mm});
            skLineSegment(sketch, "E2134", {"start": v(10.5, -43.76) * mm, "end": v(11.01, -44.18) * mm});
            skLineSegment(sketch, "E2135", {"start": v(11.01, -44.18) * mm, "end": v(11.03, -44.2) * mm});
            skLineSegment(sketch, "E2136", {"start": v(11.03, -44.2) * mm, "end": v(11.23, -44.42) * mm});
            skLineSegment(sketch, "E2137", {"start": v(11.23, -44.42) * mm, "end": v(11.25, -44.44) * mm});
            skLineSegment(sketch, "E2138", {"start": v(11.25, -44.44) * mm, "end": v(11.42, -44.66) * mm});
            skLineSegment(sketch, "E2139", {"start": v(11.42, -44.66) * mm, "end": v(11.43, -44.68) * mm});
            skLineSegment(sketch, "E2140", {"start": v(11.43, -44.68) * mm, "end": v(11.57, -44.9) * mm});
            skLineSegment(sketch, "E2141", {"start": v(11.57, -44.9) * mm, "end": v(11.58, -44.92) * mm});
            skLineSegment(sketch, "E2142", {"start": v(11.58, -44.92) * mm, "end": v(11.68, -45.15) * mm});
            skLineSegment(sketch, "E2143", {"start": v(11.68, -45.15) * mm, "end": v(11.68, -45.16) * mm});
            skLineSegment(sketch, "E2144", {"start": v(11.68, -45.16) * mm, "end": v(11.74, -45.4) * mm});
            skLineSegment(sketch, "E2145", {"start": v(11.74, -45.4) * mm, "end": v(11.75, -45.4) * mm});
            skLineSegment(sketch, "E2146", {"start": v(11.75, -45.4) * mm, "end": v(11.75, -45.41) * mm});
            skLineSegment(sketch, "E2147", {"start": v(11.75, -45.41) * mm, "end": v(11.77, -45.65) * mm});
            skLineSegment(sketch, "E2148", {"start": v(11.77, -45.65) * mm, "end": v(11.77, -45.67) * mm});
            skLineSegment(sketch, "E2149", {"start": v(11.77, -45.67) * mm, "end": v(11.75, -45.86) * mm});
            skLineSegment(sketch, "E2150", {"start": v(11.75, -45.86) * mm, "end": v(11.75, -45.86) * mm});
            skLineSegment(sketch, "E2151", {"start": v(11.75, -45.86) * mm, "end": v(11.7, -46.07) * mm});
            skLineSegment(sketch, "E2152", {"start": v(11.7, -46.07) * mm, "end": v(11.7, -46.09) * mm});
            skLineSegment(sketch, "E2153", {"start": v(11.7, -46.09) * mm, "end": v(11.6, -46.3) * mm});
            skLineSegment(sketch, "E2154", {"start": v(11.6, -46.3) * mm, "end": v(11.6, -46.33) * mm});
            skLineSegment(sketch, "E2155", {"start": v(11.6, -46.33) * mm, "end": v(11.48, -46.56) * mm});
            skLineSegment(sketch, "E2156", {"start": v(11.48, -46.56) * mm, "end": v(11.47, -46.58) * mm});
            skLineSegment(sketch, "E2157", {"start": v(11.47, -46.58) * mm, "end": v(11.15, -47.1) * mm});
            skLineSegment(sketch, "E2158", {"start": v(11.15, -47.1) * mm, "end": v(11.13, -47.11) * mm});
            skLineSegment(sketch, "E2159", {"start": v(11.13, -47.11) * mm, "end": v(10.7, -47.66) * mm});
            skLineSegment(sketch, "E2160", {"start": v(10.7, -47.66) * mm, "end": v(10.68, -47.68) * mm});
            skLineSegment(sketch, "E2161", {"start": v(10.68, -47.68) * mm, "end": v(10.14, -48.25) * mm});
            skLineSegment(sketch, "E2162", {"start": v(10.14, -48.25) * mm, "end": v(10.1, -48.3) * mm});
            skLineSegment(sketch, "E2163", {"start": v(10.1, -48.3) * mm, "end": v(9.46, -48.88) * mm});
            skLineSegment(sketch, "E2164", {"start": v(9.46, -48.88) * mm, "end": v(9.4, -48.93) * mm});
            skLineSegment(sketch, "E2165", {"start": v(9.4, -48.93) * mm, "end": v(8.68, -49.5) * mm});
            skLineSegment(sketch, "E2166", {"start": v(8.68, -49.5) * mm, "end": v(8.61, -49.55) * mm});
            skLineSegment(sketch, "E2167", {"start": v(8.61, -49.55) * mm, "end": v(7.81, -50.12) * mm});
            skLineSegment(sketch, "E2168", {"start": v(7.81, -50.12) * mm, "end": v(6.94, -50.67) * mm});
            skLineSegment(sketch, "E2169", {"start": v(6.94, -50.67) * mm, "end": v(6.87, -50.71) * mm});
            skLineSegment(sketch, "E2170", {"start": v(6.87, -50.71) * mm, "end": v(5.93, -51.22) * mm});
            skLineSegment(sketch, "E2171", {"start": v(5.93, -51.22) * mm, "end": v(5.85, -51.26) * mm});
            skLineSegment(sketch, "E2172", {"start": v(5.85, -51.26) * mm, "end": v(4.87, -51.71) * mm});
            skLineSegment(sketch, "E2173", {"start": v(4.87, -51.71) * mm, "end": v(4.79, -51.75) * mm});
            skLineSegment(sketch, "E2174", {"start": v(4.79, -51.75) * mm, "end": v(3.76, -52.14) * mm});
            skLineSegment(sketch, "E2175", {"start": v(3.76, -52.14) * mm, "end": v(2.7, -52.46) * mm});
            skLineSegment(sketch, "E2176", {"start": v(2.7, -52.46) * mm, "end": v(2.6, -52.48) * mm});
            skLineSegment(sketch, "E2177", {"start": v(2.6, -52.48) * mm, "end": v(1.52, -52.72) * mm});
            skLineSegment(sketch, "E2178", {"start": v(1.52, -52.72) * mm, "end": v(1.43, -52.73) * mm});
            skLineSegment(sketch, "E2179", {"start": v(1.43, -52.73) * mm, "end": v(0.32, -52.86) * mm});
            skLineSegment(sketch, "E2180", {"start": v(0.32, -52.86) * mm, "end": v(0.27, -52.87) * mm});
            skLineSegment(sketch, "E2181", {"start": v(0.27, -52.87) * mm, "end": v(-0.88, -52.89) * mm});
            skLineSegment(sketch, "E2182", {"start": v(-0.88, -52.89) * mm, "end": v(-0.93, -52.89) * mm});
            skLineSegment(sketch, "E2183", {"start": v(-0.93, -52.89) * mm, "end": v(-2, -52.87) * mm});
            skLineSegment(sketch, "E2184", {"start": v(-2, -52.87) * mm, "end": v(-2.06, -52.86) * mm});
            skLineSegment(sketch, "E2185", {"start": v(-2.06, -52.86) * mm, "end": v(-3.13, -52.73) * mm});
            skLineSegment(sketch, "E2186", {"start": v(-3.13, -52.73) * mm, "end": v(-3.18, -52.72) * mm});
            skLineSegment(sketch, "E2187", {"start": v(-3.18, -52.72) * mm, "end": v(-4.24, -52.49) * mm});
            skLineSegment(sketch, "E2188", {"start": v(-4.24, -52.49) * mm, "end": v(-4.3, -52.47) * mm});
            skLineSegment(sketch, "E2189", {"start": v(-4.3, -52.47) * mm, "end": v(-5.33, -52.15) * mm});
            skLineSegment(sketch, "E2190", {"start": v(-5.33, -52.15) * mm, "end": v(-5.43, -52.12) * mm});
            skLineSegment(sketch, "E2191", {"start": v(-5.43, -52.12) * mm, "end": v(-6.43, -51.71) * mm});
            skLineSegment(sketch, "E2192", {"start": v(-6.43, -51.71) * mm, "end": v(-6.53, -51.67) * mm});
            skLineSegment(sketch, "E2193", {"start": v(-6.53, -51.67) * mm, "end": v(-7.5, -51.2) * mm});
            skLineSegment(sketch, "E2194", {"start": v(-7.5, -51.2) * mm, "end": v(-8.41, -50.67) * mm});
            skLineSegment(sketch, "E2195", {"start": v(-8.41, -50.67) * mm, "end": v(-8.48, -50.63) * mm});
            skLineSegment(sketch, "E2196", {"start": v(-8.48, -50.63) * mm, "end": v(-9.34, -50.06) * mm});
            skLineSegment(sketch, "E2197", {"start": v(-9.34, -50.06) * mm, "end": v(-9.4, -50.02) * mm});
            skLineSegment(sketch, "E2198", {"start": v(-9.4, -50.02) * mm, "end": v(-10.2, -49.42) * mm});
            skLineSegment(sketch, "E2199", {"start": v(-10.2, -49.42) * mm, "end": v(-10.26, -49.37) * mm});
            skLineSegment(sketch, "E2200", {"start": v(-10.26, -49.37) * mm, "end": v(-10.97, -48.74) * mm});
            skLineSegment(sketch, "E2201", {"start": v(-10.97, -48.74) * mm, "end": v(-11.02, -48.7) * mm});
            skLineSegment(sketch, "E2202", {"start": v(-11.02, -48.7) * mm, "end": v(-11.65, -48.06) * mm});
            skLineSegment(sketch, "E2203", {"start": v(-11.65, -48.06) * mm, "end": v(-12.2, -47.43) * mm});
            skLineSegment(sketch, "E2204", {"start": v(-12.2, -47.43) * mm, "end": v(-12.23, -47.38) * mm});
            skLineSegment(sketch, "E2205", {"start": v(-12.23, -47.38) * mm, "end": v(-12.66, -46.77) * mm});
            skLineSegment(sketch, "E2206", {"start": v(-12.66, -46.77) * mm, "end": v(-12.7, -46.72) * mm});
            skLineSegment(sketch, "E2207", {"start": v(-12.7, -46.72) * mm, "end": v(-13.02, -46.13) * mm});
            skLineSegment(sketch, "E2208", {"start": v(-13.02, -46.13) * mm, "end": v(-13.03, -46.1) * mm});
            skLineSegment(sketch, "E2209", {"start": v(-13.03, -46.1) * mm, "end": v(-13.14, -45.82) * mm});
            skLineSegment(sketch, "E2210", {"start": v(-13.14, -45.82) * mm, "end": v(-13.15, -45.8) * mm});
            skLineSegment(sketch, "E2211", {"start": v(-13.15, -45.8) * mm, "end": v(-13.24, -45.53) * mm});
            skLineSegment(sketch, "E2212", {"start": v(-13.24, -45.53) * mm, "end": v(-13.24, -45.5) * mm});
            skLineSegment(sketch, "E2213", {"start": v(-13.24, -45.5) * mm, "end": v(-13.3, -45.25) * mm});
            skLineSegment(sketch, "E2214", {"start": v(-13.3, -45.25) * mm, "end": v(-13.3, -45.24) * mm});
            skLineSegment(sketch, "E2215", {"start": v(-13.3, -45.24) * mm, "end": v(-13.3, -44.98) * mm});
            skLineSegment(sketch, "E2216", {"start": v(-13.3, -44.98) * mm, "end": v(-13.3, -44.97) * mm});
            skLineSegment(sketch, "E2217", {"start": v(-33.63, 3.14) * mm, "end": v(-33.38, 3.19) * mm});
            skLineSegment(sketch, "E2218", {"start": v(-33.38, 3.19) * mm, "end": v(-33.37, 3.19) * mm});
            skLineSegment(sketch, "E2219", {"start": v(-33.37, 3.19) * mm, "end": v(-33.13, 3.2) * mm});
            skLineSegment(sketch, "E2220", {"start": v(-33.13, 3.2) * mm, "end": v(-33.12, 3.2) * mm});
            skLineSegment(sketch, "E2221", {"start": v(-33.12, 3.2) * mm, "end": v(-33.1, 3.2) * mm});
            skLineSegment(sketch, "E2222", {"start": v(-33.1, 3.2) * mm, "end": v(-32.88, 3.19) * mm});
            skLineSegment(sketch, "E2223", {"start": v(-32.88, 3.19) * mm, "end": v(-32.87, 3.18) * mm});
            skLineSegment(sketch, "E2224", {"start": v(-32.87, 3.18) * mm, "end": v(-32.66, 3.13) * mm});
            skLineSegment(sketch, "E2225", {"start": v(-32.66, 3.13) * mm, "end": v(-32.65, 3.13) * mm});
            skLineSegment(sketch, "E2226", {"start": v(-32.65, 3.13) * mm, "end": v(-32.64, 3.13) * mm});
            skLineSegment(sketch, "E2227", {"start": v(-32.64, 3.13) * mm, "end": v(-32.44, 3.04) * mm});
            skLineSegment(sketch, "E2228", {"start": v(-32.44, 3.04) * mm, "end": v(-32.43, 3.04) * mm});
            skLineSegment(sketch, "E2229", {"start": v(-32.43, 3.04) * mm, "end": v(-32.25, 2.92) * mm});
            skLineSegment(sketch, "E2230", {"start": v(-32.25, 2.92) * mm, "end": v(-32.24, 2.91) * mm});
            skLineSegment(sketch, "E2231", {"start": v(-32.24, 2.91) * mm, "end": v(-32.23, 2.9) * mm});
            skLineSegment(sketch, "E2232", {"start": v(-32.23, 2.9) * mm, "end": v(-32.05, 2.76) * mm});
            skLineSegment(sketch, "E2233", {"start": v(-32.05, 2.76) * mm, "end": v(-32.04, 2.75) * mm});
            skLineSegment(sketch, "E2234", {"start": v(-32.04, 2.75) * mm, "end": v(-31.88, 2.57) * mm});
            skLineSegment(sketch, "E2235", {"start": v(-31.88, 2.57) * mm, "end": v(-31.72, 2.37) * mm});
            skLineSegment(sketch, "E2236", {"start": v(-31.72, 2.37) * mm, "end": v(-31.71, 2.35) * mm});
            skLineSegment(sketch, "E2237", {"start": v(-31.71, 2.35) * mm, "end": v(-31.57, 2.12) * mm});
            skLineSegment(sketch, "E2238", {"start": v(-31.57, 2.12) * mm, "end": v(-31.56, 2.1) * mm});
            skLineSegment(sketch, "E2239", {"start": v(-31.56, 2.1) * mm, "end": v(-31.31, 1.57) * mm});
            skLineSegment(sketch, "E2240", {"start": v(-31.31, 1.57) * mm, "end": v(-31.3, 1.52) * mm});
            skLineSegment(sketch, "E2241", {"start": v(-31.3, 1.52) * mm, "end": v(-31.1, 0.9) * mm});
            skLineSegment(sketch, "E2242", {"start": v(-31.1, 0.9) * mm, "end": v(-31.08, 0.83) * mm});
            skLineSegment(sketch, "E2243", {"start": v(-31.08, 0.83) * mm, "end": v(-30.92, 0.12) * mm});
            skLineSegment(sketch, "E2244", {"start": v(-30.92, 0.12) * mm, "end": v(-30.8, -0.66) * mm});
            skLineSegment(sketch, "E2245", {"start": v(-30.8, -0.66) * mm, "end": v(-30.8, -0.73) * mm});
            skLineSegment(sketch, "E2246", {"start": v(-30.8, -0.73) * mm, "end": v(-30.71, -1.57) * mm});
            skLineSegment(sketch, "E2247", {"start": v(-30.71, -1.57) * mm, "end": v(-30.7, -1.65) * mm});
            skLineSegment(sketch, "E2248", {"start": v(-30.7, -1.65) * mm, "end": v(-30.67, -2.55) * mm});
            skLineSegment(sketch, "E2249", {"start": v(-30.67, -2.55) * mm, "end": v(-30.67, -2.63) * mm});
            skLineSegment(sketch, "E2250", {"start": v(-30.67, -2.63) * mm, "end": v(-30.67, -3.57) * mm});
            skLineSegment(sketch, "E2251", {"start": v(-30.67, -3.57) * mm, "end": v(-30.67, -3.65) * mm});
            skLineSegment(sketch, "E2252", {"start": v(-30.67, -3.65) * mm, "end": v(-30.77, -5.65) * mm});
            skLineSegment(sketch, "E2253", {"start": v(-30.77, -5.65) * mm, "end": v(-30.78, -5.73) * mm});
            skLineSegment(sketch, "E2254", {"start": v(-30.78, -5.73) * mm, "end": v(-31, -7.8) * mm});
            skLineSegment(sketch, "E2255", {"start": v(-31, -7.8) * mm, "end": v(-31.01, -7.88) * mm});
            skLineSegment(sketch, "E2256", {"start": v(-31.01, -7.88) * mm, "end": v(-31.03, -7.97) * mm});
            skLineSegment(sketch, "E2257", {"start": v(-31.03, -7.97) * mm, "end": v(-31.37, -10.03) * mm});
            skLineSegment(sketch, "E2258", {"start": v(-31.37, -10.03) * mm, "end": v(-31.39, -10.1) * mm});
            skLineSegment(sketch, "E2259", {"start": v(-31.39, -10.1) * mm, "end": v(-31.84, -12.09) * mm});
            skLineSegment(sketch, "E2260", {"start": v(-31.84, -12.09) * mm, "end": v(-31.86, -12.17) * mm});
            skLineSegment(sketch, "E2261", {"start": v(-31.86, -12.17) * mm, "end": v(-31.88, -12.25) * mm});
            skLineSegment(sketch, "E2262", {"start": v(-31.88, -12.25) * mm, "end": v(-32.43, -14.07) * mm});
            skLineSegment(sketch, "E2263", {"start": v(-32.43, -14.07) * mm, "end": v(-32.45, -14.14) * mm});
            skLineSegment(sketch, "E2264", {"start": v(-32.45, -14.14) * mm, "end": v(-32.75, -14.97) * mm});
            skLineSegment(sketch, "E2265", {"start": v(-32.75, -14.97) * mm, "end": v(-32.78, -15.04) * mm});
            skLineSegment(sketch, "E2266", {"start": v(-32.78, -15.04) * mm, "end": v(-33.1, -15.8) * mm});
            skLineSegment(sketch, "E2267", {"start": v(-33.1, -15.8) * mm, "end": v(-33.44, -16.49) * mm});
            skLineSegment(sketch, "E2268", {"start": v(-33.44, -16.49) * mm, "end": v(-33.47, -16.54) * mm});
            skLineSegment(sketch, "E2269", {"start": v(-33.47, -16.54) * mm, "end": v(-33.82, -17.15) * mm});
            skLineSegment(sketch, "E2270", {"start": v(-33.82, -17.15) * mm, "end": v(-33.85, -17.2) * mm});
            skLineSegment(sketch, "E2271", {"start": v(-33.85, -17.2) * mm, "end": v(-34.22, -17.7) * mm});
            skLineSegment(sketch, "E2272", {"start": v(-34.22, -17.7) * mm, "end": v(-34.23, -17.72) * mm});
            skLineSegment(sketch, "E2273", {"start": v(-34.23, -17.72) * mm, "end": v(-34.62, -18.13) * mm});
            skLineSegment(sketch, "E2274", {"start": v(-34.62, -18.13) * mm, "end": v(-34.63, -18.14) * mm});
            skLineSegment(sketch, "E2275", {"start": v(-34.63, -18.14) * mm, "end": v(-34.83, -18.3) * mm});
            skLineSegment(sketch, "E2276", {"start": v(-34.83, -18.3) * mm, "end": v(-34.84, -18.31) * mm});
            skLineSegment(sketch, "E2277", {"start": v(-34.84, -18.31) * mm, "end": v(-35.04, -18.45) * mm});
            skLineSegment(sketch, "E2278", {"start": v(-35.04, -18.45) * mm, "end": v(-35.06, -18.45) * mm});
            skLineSegment(sketch, "E2279", {"start": v(-35.06, -18.45) * mm, "end": v(-35.25, -18.55) * mm});
            skLineSegment(sketch, "E2280", {"start": v(-35.25, -18.55) * mm, "end": v(-35.26, -18.56) * mm});
            skLineSegment(sketch, "E2281", {"start": v(-35.26, -18.56) * mm, "end": v(-35.47, -18.63) * mm});
            skLineSegment(sketch, "E2282", {"start": v(-35.47, -18.63) * mm, "end": v(-35.48, -18.63) * mm});
            skLineSegment(sketch, "E2283", {"start": v(-35.48, -18.63) * mm, "end": v(-35.69, -18.67) * mm});
            skLineSegment(sketch, "E2284", {"start": v(-35.69, -18.67) * mm, "end": v(-35.7, -18.67) * mm});
            skLineSegment(sketch, "E2285", {"start": v(-35.7, -18.67) * mm, "end": v(-35.9, -18.67) * mm});
            skLineSegment(sketch, "E2286", {"start": v(-35.9, -18.67) * mm, "end": v(-35.92, -18.67) * mm});
            skLineSegment(sketch, "E2287", {"start": v(-35.92, -18.67) * mm, "end": v(-36.12, -18.63) * mm});
            skLineSegment(sketch, "E2288", {"start": v(-36.12, -18.63) * mm, "end": v(-36.13, -18.63) * mm});
            skLineSegment(sketch, "E2289", {"start": v(-36.13, -18.63) * mm, "end": v(-36.34, -18.56) * mm});
            skLineSegment(sketch, "E2290", {"start": v(-36.34, -18.56) * mm, "end": v(-36.35, -18.56) * mm});
            skLineSegment(sketch, "E2291", {"start": v(-36.35, -18.56) * mm, "end": v(-36.4, -18.52) * mm});
            skLineSegment(sketch, "E2292", {"start": v(-36.4, -18.52) * mm, "end": v(-37.23, -17.71) * mm});
            skLineSegment(sketch, "E2293", {"start": v(-37.23, -17.71) * mm, "end": v(-37.27, -17.67) * mm});
            skLineSegment(sketch, "E2294", {"start": v(-37.27, -17.67) * mm, "end": v(-38.03, -16.71) * mm});
            skLineSegment(sketch, "E2295", {"start": v(-38.03, -16.71) * mm, "end": v(-38.07, -16.66) * mm});
            skLineSegment(sketch, "E2296", {"start": v(-38.07, -16.66) * mm, "end": v(-38.74, -15.57) * mm});
            skLineSegment(sketch, "E2297", {"start": v(-38.74, -15.57) * mm, "end": v(-38.77, -15.51) * mm});
            skLineSegment(sketch, "E2298", {"start": v(-38.77, -15.51) * mm, "end": v(-39.33, -14.3) * mm});
            skLineSegment(sketch, "E2299", {"start": v(-39.33, -14.3) * mm, "end": v(-39.36, -14.24) * mm});
            skLineSegment(sketch, "E2300", {"start": v(-39.36, -14.24) * mm, "end": v(-39.38, -14.18) * mm});
            skLineSegment(sketch, "E2301", {"start": v(-39.38, -14.18) * mm, "end": v(-39.83, -12.87) * mm});
            skLineSegment(sketch, "E2302", {"start": v(-39.83, -12.87) * mm, "end": v(-39.85, -12.8) * mm});
            skLineSegment(sketch, "E2303", {"start": v(-39.85, -12.8) * mm, "end": v(-40.17, -11.42) * mm});
            skLineSegment(sketch, "E2304", {"start": v(-40.17, -11.42) * mm, "end": v(-40.19, -11.35) * mm});
            skLineSegment(sketch, "E2305", {"start": v(-40.19, -11.35) * mm, "end": v(-40.37, -9.92) * mm});
            skLineSegment(sketch, "E2306", {"start": v(-40.37, -9.92) * mm, "end": v(-40.38, -9.86) * mm});
            skLineSegment(sketch, "E2307", {"start": v(-40.38, -9.86) * mm, "end": v(-40.38, -9.8) * mm});
            skLineSegment(sketch, "E2308", {"start": v(-40.38, -9.8) * mm, "end": v(-40.42, -8.33) * mm});
            skLineSegment(sketch, "E2309", {"start": v(-40.42, -8.33) * mm, "end": v(-40.42, -8.28) * mm});
            skLineSegment(sketch, "E2310", {"start": v(-40.42, -8.28) * mm, "end": v(-40.3, -6.79) * mm});
            skLineSegment(sketch, "E2311", {"start": v(-40.3, -6.79) * mm, "end": v(-40.3, -6.73) * mm});
            skLineSegment(sketch, "E2312", {"start": v(-40.3, -6.73) * mm, "end": v(-40.28, -6.68) * mm});
            skLineSegment(sketch, "E2313", {"start": v(-40.28, -6.68) * mm, "end": v(-39.99, -5.19) * mm});
            skLineSegment(sketch, "E2314", {"start": v(-39.99, -5.19) * mm, "end": v(-39.98, -5.13) * mm});
            skLineSegment(sketch, "E2315", {"start": v(-39.98, -5.13) * mm, "end": v(-39.96, -5.08) * mm});
            skLineSegment(sketch, "E2316", {"start": v(-39.96, -5.08) * mm, "end": v(-39.49, -3.61) * mm});
            skLineSegment(sketch, "E2317", {"start": v(-39.49, -3.61) * mm, "end": v(-39.47, -3.56) * mm});
            skLineSegment(sketch, "E2318", {"start": v(-39.47, -3.56) * mm, "end": v(-38.8, -2.13) * mm});
            skLineSegment(sketch, "E2319", {"start": v(-38.8, -2.13) * mm, "end": v(-38.77, -2.08) * mm});
            skLineSegment(sketch, "E2320", {"start": v(-38.77, -2.08) * mm, "end": v(-38.75, -2.03) * mm});
            skLineSegment(sketch, "E2321", {"start": v(-38.75, -2.03) * mm, "end": v(-38.34, -1.34) * mm});
            skLineSegment(sketch, "E2322", {"start": v(-38.34, -1.34) * mm, "end": v(-38.3, -1.29) * mm});
            skLineSegment(sketch, "E2323", {"start": v(-38.3, -1.29) * mm, "end": v(-37.84, -0.61) * mm});
            skLineSegment(sketch, "E2324", {"start": v(-37.84, -0.61) * mm, "end": v(-37.32, 0.04) * mm});
            skLineSegment(sketch, "E2325", {"start": v(-37.32, 0.04) * mm, "end": v(-37.28, 0.09) * mm});
            skLineSegment(sketch, "E2326", {"start": v(-37.28, 0.09) * mm, "end": v(-36.71, 0.72) * mm});
            skLineSegment(sketch, "E2327", {"start": v(-36.71, 0.72) * mm, "end": v(-36.67, 0.76) * mm});
            skLineSegment(sketch, "E2328", {"start": v(-36.67, 0.76) * mm, "end": v(-36.04, 1.37) * mm});
            skLineSegment(sketch, "E2329", {"start": v(-36.04, 1.37) * mm, "end": v(-36, 1.41) * mm});
            skLineSegment(sketch, "E2330", {"start": v(-36, 1.41) * mm, "end": v(-35.3, 2) * mm});
            skLineSegment(sketch, "E2331", {"start": v(-35.3, 2) * mm, "end": v(-35.25, 2.03) * mm});
            skLineSegment(sketch, "E2332", {"start": v(-35.25, 2.03) * mm, "end": v(-34.5, 2.58) * mm});
            skLineSegment(sketch, "E2333", {"start": v(-34.5, 2.58) * mm, "end": v(-34.47, 2.6) * mm});
            skLineSegment(sketch, "E2334", {"start": v(-34.47, 2.6) * mm, "end": v(-33.64, 3.13) * mm});
            skLineSegment(sketch, "E2335", {"start": v(-33.64, 3.13) * mm, "end": v(-33.63, 3.14) * mm});
            skLineSegment(sketch, "E2336", {"start": v(10.02, 15.46) * mm, "end": v(10.37, 16) * mm});
            skLineSegment(sketch, "E2337", {"start": v(10.37, 16) * mm, "end": v(10.38, 16.03) * mm});
            skLineSegment(sketch, "E2338", {"start": v(10.38, 16.03) * mm, "end": v(10.4, 16.06) * mm});
            skLineSegment(sketch, "E2339", {"start": v(10.4, 16.06) * mm, "end": v(10.64, 16.61) * mm});
            skLineSegment(sketch, "E2340", {"start": v(10.64, 16.61) * mm, "end": v(10.65, 16.64) * mm});
            skLineSegment(sketch, "E2341", {"start": v(10.65, 16.64) * mm, "end": v(10.8, 17.2) * mm});
            skLineSegment(sketch, "E2342", {"start": v(10.8, 17.2) * mm, "end": v(10.81, 17.23) * mm});
            skLineSegment(sketch, "E2343", {"start": v(10.81, 17.23) * mm, "end": v(10.85, 17.5) * mm});
            skLineSegment(sketch, "E2344", {"start": v(10.85, 17.5) * mm, "end": v(10.87, 17.79) * mm});
            skLineSegment(sketch, "E2345", {"start": v(10.87, 17.79) * mm, "end": v(10.87, 17.8) * mm});
            skLineSegment(sketch, "E2346", {"start": v(10.87, 17.8) * mm, "end": v(10.87, 17.81) * mm});
            skLineSegment(sketch, "E2347", {"start": v(10.87, 17.81) * mm, "end": v(10.85, 18.05) * mm});
            skLineSegment(sketch, "E2348", {"start": v(10.85, 18.05) * mm, "end": v(10.85, 18.06) * mm});
            skLineSegment(sketch, "E2349", {"start": v(10.85, 18.06) * mm, "end": v(10.8, 18.3) * mm});
            skLineSegment(sketch, "E2350", {"start": v(10.8, 18.3) * mm, "end": v(10.8, 18.3) * mm});
            skLineSegment(sketch, "E2351", {"start": v(10.8, 18.3) * mm, "end": v(10.72, 18.55) * mm});
            skLineSegment(sketch, "E2352", {"start": v(10.72, 18.55) * mm, "end": v(10.71, 18.57) * mm});
            skLineSegment(sketch, "E2353", {"start": v(10.71, 18.57) * mm, "end": v(10.6, 18.82) * mm});
            skLineSegment(sketch, "E2354", {"start": v(10.6, 18.82) * mm, "end": v(10.6, 18.84) * mm});
            skLineSegment(sketch, "E2355", {"start": v(10.6, 18.84) * mm, "end": v(10.3, 19.37) * mm});
            skLineSegment(sketch, "E2356", {"start": v(10.3, 19.37) * mm, "end": v(10.27, 19.4) * mm});
            skLineSegment(sketch, "E2357", {"start": v(10.27, 19.4) * mm, "end": v(9.87, 19.95) * mm});
            skLineSegment(sketch, "E2358", {"start": v(9.87, 19.95) * mm, "end": v(9.83, 19.99) * mm});
            skLineSegment(sketch, "E2359", {"start": v(9.83, 19.99) * mm, "end": v(9.33, 20.54) * mm});
            skLineSegment(sketch, "E2360", {"start": v(9.33, 20.54) * mm, "end": v(9.28, 20.58) * mm});
            skLineSegment(sketch, "E2361", {"start": v(9.28, 20.58) * mm, "end": v(8.7, 21.13) * mm});
            skLineSegment(sketch, "E2362", {"start": v(8.7, 21.13) * mm, "end": v(8.02, 21.67) * mm});
            skLineSegment(sketch, "E2363", {"start": v(8.02, 21.67) * mm, "end": v(7.97, 21.7) * mm});
            skLineSegment(sketch, "E2364", {"start": v(7.97, 21.7) * mm, "end": v(7.23, 22.23) * mm});
            skLineSegment(sketch, "E2365", {"start": v(7.23, 22.23) * mm, "end": v(7.17, 22.26) * mm});
            skLineSegment(sketch, "E2366", {"start": v(7.17, 22.26) * mm, "end": v(6.36, 22.76) * mm});
            skLineSegment(sketch, "E2367", {"start": v(6.36, 22.76) * mm, "end": v(6.3, 22.8) * mm});
            skLineSegment(sketch, "E2368", {"start": v(6.3, 22.8) * mm, "end": v(5.43, 23.25) * mm});
            skLineSegment(sketch, "E2369", {"start": v(5.43, 23.25) * mm, "end": v(4.52, 23.66) * mm});
            skLineSegment(sketch, "E2370", {"start": v(4.52, 23.66) * mm, "end": v(4.43, 23.7) * mm});
            skLineSegment(sketch, "E2371", {"start": v(4.43, 23.7) * mm, "end": v(3.47, 24.06) * mm});
            skLineSegment(sketch, "E2372", {"start": v(3.47, 24.06) * mm, "end": v(3.38, 24.09) * mm});
            skLineSegment(sketch, "E2373", {"start": v(3.38, 24.09) * mm, "end": v(2.4, 24.38) * mm});
            skLineSegment(sketch, "E2374", {"start": v(2.4, 24.38) * mm, "end": v(1.38, 24.6) * mm});
            skLineSegment(sketch, "E2375", {"start": v(1.38, 24.6) * mm, "end": v(1.28, 24.62) * mm});
            skLineSegment(sketch, "E2376", {"start": v(1.28, 24.62) * mm, "end": v(0.25, 24.76) * mm});
            skLineSegment(sketch, "E2377", {"start": v(0.25, 24.76) * mm, "end": v(0.2, 24.77) * mm});
            skLineSegment(sketch, "E2378", {"start": v(0.2, 24.77) * mm, "end": v(-0.83, 24.82) * mm});
            skLineSegment(sketch, "E2379", {"start": v(-0.83, 24.82) * mm, "end": v(-0.88, 24.82) * mm});
            skLineSegment(sketch, "E2380", {"start": v(-0.88, 24.82) * mm, "end": v(-1.84, 24.77) * mm});
            skLineSegment(sketch, "E2381", {"start": v(-1.84, 24.77) * mm, "end": v(-1.89, 24.77) * mm});
            skLineSegment(sketch, "E2382", {"start": v(-1.89, 24.77) * mm, "end": v(-2.84, 24.65) * mm});
            skLineSegment(sketch, "E2383", {"start": v(-2.84, 24.65) * mm, "end": v(-2.91, 24.64) * mm});
            skLineSegment(sketch, "E2384", {"start": v(-2.91, 24.64) * mm, "end": v(-3.87, 24.44) * mm});
            skLineSegment(sketch, "E2385", {"start": v(-3.87, 24.44) * mm, "end": v(-3.95, 24.42) * mm});
            skLineSegment(sketch, "E2386", {"start": v(-3.95, 24.42) * mm, "end": v(-4.9, 24.16) * mm});
            skLineSegment(sketch, "E2387", {"start": v(-4.9, 24.16) * mm, "end": v(-5.84, 23.83) * mm});
            skLineSegment(sketch, "E2388", {"start": v(-5.84, 23.83) * mm, "end": v(-5.92, 23.8) * mm});
            skLineSegment(sketch, "E2389", {"start": v(-5.92, 23.8) * mm, "end": v(-6.83, 23.42) * mm});
            skLineSegment(sketch, "E2390", {"start": v(-6.83, 23.42) * mm, "end": v(-6.9, 23.39) * mm});
            skLineSegment(sketch, "E2391", {"start": v(-6.9, 23.39) * mm, "end": v(-7.79, 22.95) * mm});
            skLineSegment(sketch, "E2392", {"start": v(-7.79, 22.95) * mm, "end": v(-7.86, 22.91) * mm});
            skLineSegment(sketch, "E2393", {"start": v(-7.86, 22.91) * mm, "end": v(-8.7, 22.43) * mm});
            skLineSegment(sketch, "E2394", {"start": v(-8.7, 22.43) * mm, "end": v(-8.75, 22.38) * mm});
            skLineSegment(sketch, "E2395", {"start": v(-8.75, 22.38) * mm, "end": v(-9.53, 21.86) * mm});
            skLineSegment(sketch, "E2396", {"start": v(-9.53, 21.86) * mm, "end": v(-10.24, 21.29) * mm});
            skLineSegment(sketch, "E2397", {"start": v(-10.24, 21.29) * mm, "end": v(-10.3, 21.24) * mm});
            skLineSegment(sketch, "E2398", {"start": v(-10.3, 21.24) * mm, "end": v(-10.93, 20.65) * mm});
            skLineSegment(sketch, "E2399", {"start": v(-10.93, 20.65) * mm, "end": v(-10.98, 20.6) * mm});
            skLineSegment(sketch, "E2400", {"start": v(-10.98, 20.6) * mm, "end": v(-11.52, 19.97) * mm});
            skLineSegment(sketch, "E2401", {"start": v(-11.52, 19.97) * mm, "end": v(-11.54, 19.94) * mm});
            skLineSegment(sketch, "E2402", {"start": v(-11.54, 19.94) * mm, "end": v(-11.98, 19.3) * mm});
            skLineSegment(sketch, "E2403", {"start": v(-11.98, 19.3) * mm, "end": v(-12, 19.27) * mm});
            skLineSegment(sketch, "E2404", {"start": v(-12, 19.27) * mm, "end": v(-12.32, 18.6) * mm});
            skLineSegment(sketch, "E2405", {"start": v(-12.32, 18.6) * mm, "end": v(-12.34, 18.58) * mm});
            skLineSegment(sketch, "E2406", {"start": v(-12.34, 18.58) * mm, "end": v(-12.35, 18.55) * mm});
            skLineSegment(sketch, "E2407", {"start": v(-12.35, 18.55) * mm, "end": v(-12.46, 18.21) * mm});
            skLineSegment(sketch, "E2408", {"start": v(-12.46, 18.21) * mm, "end": v(-12.55, 17.87) * mm});
            skLineSegment(sketch, "E2409", {"start": v(-12.55, 17.87) * mm, "end": v(-12.56, 17.85) * mm});
            skLineSegment(sketch, "E2410", {"start": v(-12.56, 17.85) * mm, "end": v(-12.6, 17.5) * mm});
            skLineSegment(sketch, "E2411", {"start": v(-12.6, 17.5) * mm, "end": v(-12.63, 17.17) * mm});
            skLineSegment(sketch, "E2412", {"start": v(-12.63, 17.17) * mm, "end": v(-12.63, 17.15) * mm});
            skLineSegment(sketch, "E2413", {"start": v(-12.63, 17.15) * mm, "end": v(-12.63, 17.14) * mm});
            skLineSegment(sketch, "E2414", {"start": v(-12.63, 17.14) * mm, "end": v(-12.63, 17.11) * mm});
            skLineSegment(sketch, "E2415", {"start": v(-12.63, 17.11) * mm, "end": v(-12.58, 16.52) * mm});
            skLineSegment(sketch, "E2416", {"start": v(-12.58, 16.52) * mm, "end": v(-12.57, 16.5) * mm});
            skLineSegment(sketch, "E2417", {"start": v(-12.57, 16.5) * mm, "end": v(-12.43, 15.93) * mm});
            skLineSegment(sketch, "E2418", {"start": v(-12.43, 15.93) * mm, "end": v(-12.42, 15.9) * mm});
            skLineSegment(sketch, "E2419", {"start": v(-12.42, 15.9) * mm, "end": v(-12.18, 15.36) * mm});
            skLineSegment(sketch, "E2420", {"start": v(-12.18, 15.36) * mm, "end": v(-12.17, 15.34) * mm});
            skLineSegment(sketch, "E2421", {"start": v(-12.17, 15.34) * mm, "end": v(-11.82, 14.8) * mm});
            skLineSegment(sketch, "E2422", {"start": v(-11.82, 14.8) * mm, "end": v(-11.8, 14.78) * mm});
            skLineSegment(sketch, "E2423", {"start": v(-11.8, 14.78) * mm, "end": v(-11.38, 14.29) * mm});
            skLineSegment(sketch, "E2424", {"start": v(-11.38, 14.29) * mm, "end": v(-11.35, 14.27) * mm});
            skLineSegment(sketch, "E2425", {"start": v(-11.35, 14.27) * mm, "end": v(-10.84, 13.81) * mm});
            skLineSegment(sketch, "E2426", {"start": v(-10.84, 13.81) * mm, "end": v(-10.82, 13.79) * mm});
            skLineSegment(sketch, "E2427", {"start": v(-10.82, 13.79) * mm, "end": v(-10.22, 13.37) * mm});
            skLineSegment(sketch, "E2428", {"start": v(-10.22, 13.37) * mm, "end": v(-10.18, 13.34) * mm});
            skLineSegment(sketch, "E2429", {"start": v(-10.18, 13.34) * mm, "end": v(-9.5, 12.95) * mm});
            skLineSegment(sketch, "E2430", {"start": v(-9.5, 12.95) * mm, "end": v(-9.44, 12.92) * mm});
            skLineSegment(sketch, "E2431", {"start": v(-9.44, 12.92) * mm, "end": v(-8.69, 12.57) * mm});
            skLineSegment(sketch, "E2432", {"start": v(-8.69, 12.57) * mm, "end": v(-8.62, 12.54) * mm});
            skLineSegment(sketch, "E2433", {"start": v(-8.62, 12.54) * mm, "end": v(-7.8, 12.23) * mm});
            skLineSegment(sketch, "E2434", {"start": v(-7.8, 12.23) * mm, "end": v(-7.72, 12.21) * mm});
            skLineSegment(sketch, "E2435", {"start": v(-7.72, 12.21) * mm, "end": v(-6.81, 11.94) * mm});
            skLineSegment(sketch, "E2436", {"start": v(-6.81, 11.94) * mm, "end": v(-5.83, 11.72) * mm});
            skLineSegment(sketch, "E2437", {"start": v(-5.83, 11.72) * mm, "end": v(-5.75, 11.7) * mm});
            skLineSegment(sketch, "E2438", {"start": v(-5.75, 11.7) * mm, "end": v(-4.7, 11.52) * mm});
            skLineSegment(sketch, "E2439", {"start": v(-4.7, 11.52) * mm, "end": v(-4.62, 11.51) * mm});
            skLineSegment(sketch, "E2440", {"start": v(-4.62, 11.51) * mm, "end": v(-3.5, 11.38) * mm});
            skLineSegment(sketch, "E2441", {"start": v(-3.5, 11.38) * mm, "end": v(-3.4, 11.37) * mm});
            skLineSegment(sketch, "E2442", {"start": v(-3.4, 11.37) * mm, "end": v(-2.22, 11.3) * mm});
            skLineSegment(sketch, "E2443", {"start": v(-2.22, 11.3) * mm, "end": v(-0.98, 11.27) * mm});
            skLineSegment(sketch, "E2444", {"start": v(-0.98, 11.27) * mm, "end": v(-0.92, 11.26) * mm});
            skLineSegment(sketch, "E2445", {"start": v(-0.92, 11.26) * mm, "end": v(-0.88, 11.26) * mm});
            skLineSegment(sketch, "E2446", {"start": v(-0.88, 11.26) * mm, "end": v(0.37, 11.3) * mm});
            skLineSegment(sketch, "E2447", {"start": v(0.37, 11.3) * mm, "end": v(0.42, 11.3) * mm});
            skLineSegment(sketch, "E2448", {"start": v(0.42, 11.3) * mm, "end": v(1.58, 11.41) * mm});
            skLineSegment(sketch, "E2449", {"start": v(1.58, 11.41) * mm, "end": v(1.67, 11.42) * mm});
            skLineSegment(sketch, "E2450", {"start": v(1.67, 11.42) * mm, "end": v(2.77, 11.6) * mm});
            skLineSegment(sketch, "E2451", {"start": v(2.77, 11.6) * mm, "end": v(2.85, 11.6) * mm});
            skLineSegment(sketch, "E2452", {"start": v(2.85, 11.6) * mm, "end": v(3.89, 11.84) * mm});
            skLineSegment(sketch, "E2453", {"start": v(3.89, 11.84) * mm, "end": v(3.96, 11.86) * mm});
            skLineSegment(sketch, "E2454", {"start": v(3.96, 11.86) * mm, "end": v(4.94, 12.14) * mm});
            skLineSegment(sketch, "E2455", {"start": v(4.94, 12.14) * mm, "end": v(5.85, 12.48) * mm});
            skLineSegment(sketch, "E2456", {"start": v(5.85, 12.48) * mm, "end": v(5.92, 12.5) * mm});
            skLineSegment(sketch, "E2457", {"start": v(5.92, 12.5) * mm, "end": v(6.76, 12.89) * mm});
            skLineSegment(sketch, "E2458", {"start": v(6.76, 12.89) * mm, "end": v(6.82, 12.92) * mm});
            skLineSegment(sketch, "E2459", {"start": v(6.82, 12.92) * mm, "end": v(7.59, 13.34) * mm});
            skLineSegment(sketch, "E2460", {"start": v(7.59, 13.34) * mm, "end": v(7.64, 13.37) * mm});
            skLineSegment(sketch, "E2461", {"start": v(7.64, 13.37) * mm, "end": v(8.33, 13.83) * mm});
            skLineSegment(sketch, "E2462", {"start": v(8.33, 13.83) * mm, "end": v(8.38, 13.86) * mm});
            skLineSegment(sketch, "E2463", {"start": v(8.38, 13.86) * mm, "end": v(8.99, 14.35) * mm});
            skLineSegment(sketch, "E2464", {"start": v(8.99, 14.35) * mm, "end": v(9.51, 14.86) * mm});
            skLineSegment(sketch, "E2465", {"start": v(9.51, 14.86) * mm, "end": v(9.56, 14.9) * mm});
            skLineSegment(sketch, "E2466", {"start": v(9.56, 14.9) * mm, "end": v(10, 15.44) * mm});
            skLineSegment(sketch, "E2467", {"start": v(10, 15.44) * mm, "end": v(10.02, 15.46) * mm});
            skSolve(sketch);
        }
        {
            var Q0;
            Q0=qSketchRegion(id+"F0",true);
            extrude(context, id + "F1", {"entities" : qUnion([Q0]), "depth" : 3 * mm});
        }
    });
